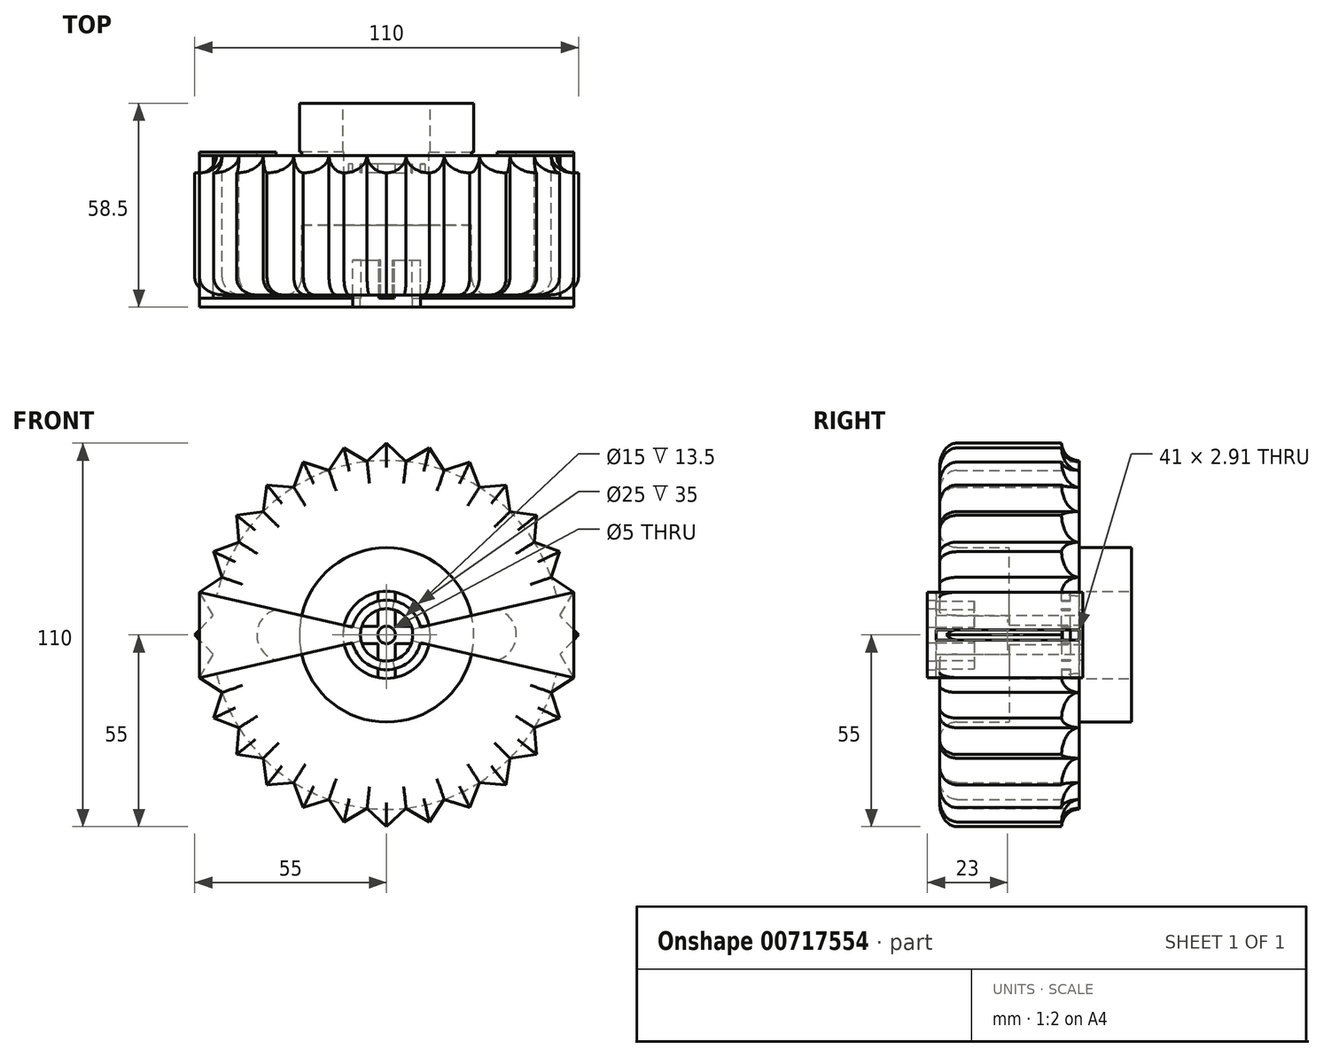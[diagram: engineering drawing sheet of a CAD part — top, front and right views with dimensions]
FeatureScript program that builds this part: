
annotation { "Feature Type Name" : "Feature", "Feature Type Description" : "" }
export const myFeature = defineFeature(function(context is Context, id is Id, definition is map)
    precondition{}
    {
        {
            var Q0;
            Q0=qCreatedBy(makeId("Front.planeOp"),FACE);
            var sketch = newSketch(context, id + "F0", { "sketchPlane" : qUnion([Q0])});
            skCircle(sketch, "E0", {"center": v(0, 0) * mm, "radius": 50 * mm});
            skLineSegment(sketch, "E1", {"start": v(-50, 0) * mm, "end": v(50, 0) * mm});
            skLineSegment(sketch, "E2", {"start": v(0, 50) * mm, "end": v(0, -50) * mm});
            skLineSegment(sketch, "E3", {"start": v(0, -50) * mm, "end": v(0, -55) * mm});
            skLineSegment(sketch, "E4.MirrorCS", {"start": v(50, 0) * mm, "end": v(-50, 0) * mm});
            skLineSegment(sketch, "E5.MirrorCS", {"start": v(0, 50) * mm, "end": v(0, 55) * mm});
            skLineSegment(sketch, "E6", {"start": v(50, 0) * mm, "end": v(55, 0) * mm});
            skLineSegment(sketch, "E7.MirrorCS", {"start": v(-50, 0) * mm, "end": v(-55, 0) * mm});
            skLineSegment(sketch, "E8", {"start": v(0, 0) * mm, "end": v(-53.62, -12.24) * mm});
            skLineSegment(sketch, "E9", {"start": v(0, 0) * mm, "end": v(-49.55, -23.86) * mm});
            skLineSegment(sketch, "E10", {"start": v(0, 0) * mm, "end": v(-43, -34.3) * mm});
            skLineSegment(sketch, "E11", {"start": v(0, 0) * mm, "end": v(-34.3, -43) * mm});
            skLineSegment(sketch, "E12", {"start": v(0, 0) * mm, "end": v(-23.86, -49.55) * mm});
            skLineSegment(sketch, "E13", {"start": v(0, 0) * mm, "end": v(-12.24, -53.62) * mm});
            skPoint(sketch, "E14", {"position": v(-48.75, -11.13) * mm});
            skPoint(sketch, "E15", {"position": v(-45.05, -21.7) * mm});
            skPoint(sketch, "E16", {"position": v(-39.1, -31.17) * mm});
            skPoint(sketch, "E17", {"position": v(-31.17, -39.1) * mm});
            skPoint(sketch, "E18", {"position": v(-21.7, -45.05) * mm});
            skPoint(sketch, "E19", {"position": v(-11.13, -48.75) * mm});
            skLineSegment(sketch, "E20", {"start": v(0, 0) * mm, "end": v(-49.69, -5.6) * mm});
            skLineSegment(sketch, "E21", {"start": v(0, 0) * mm, "end": v(-47.2, -16.51) * mm});
            skLineSegment(sketch, "E22", {"start": v(0, 0) * mm, "end": v(-42.34, -26.6) * mm});
            skLineSegment(sketch, "E23", {"start": v(0, 0) * mm, "end": v(-35.36, -35.36) * mm});
            skLineSegment(sketch, "E24", {"start": v(0, 0) * mm, "end": v(-26.6, -42.34) * mm});
            skLineSegment(sketch, "E25", {"start": v(0, 0) * mm, "end": v(-16.51, -47.2) * mm});
            skLineSegment(sketch, "E26", {"start": v(0, 0) * mm, "end": v(-5.6, -49.69) * mm});
            skLineSegment(sketch, "E27.MirrorCS", {"start": v(0, 0) * mm, "end": v(5.6, -49.69) * mm});
            skLineSegment(sketch, "E28.MirrorCS", {"start": v(0, 0) * mm, "end": v(12.24, -53.62) * mm});
            skLineSegment(sketch, "E29.MirrorCS", {"start": v(0, 0) * mm, "end": v(16.51, -47.2) * mm});
            skLineSegment(sketch, "E30.MirrorCS", {"start": v(0, 0) * mm, "end": v(23.86, -49.55) * mm});
            skLineSegment(sketch, "E31.MirrorCS", {"start": v(0, 0) * mm, "end": v(26.6, -42.34) * mm});
            skLineSegment(sketch, "E32.MirrorCS", {"start": v(0, 0) * mm, "end": v(34.3, -43) * mm});
            skLineSegment(sketch, "E33.MirrorCS", {"start": v(0, 0) * mm, "end": v(35.36, -35.36) * mm});
            skLineSegment(sketch, "E34.MirrorCS", {"start": v(0, 0) * mm, "end": v(43, -34.3) * mm});
            skLineSegment(sketch, "E35.MirrorCS", {"start": v(0, 0) * mm, "end": v(42.34, -26.6) * mm});
            skLineSegment(sketch, "E36.MirrorCS", {"start": v(0, 0) * mm, "end": v(49.69, -5.6) * mm});
            skLineSegment(sketch, "E37.MirrorCS", {"start": v(0, 0) * mm, "end": v(53.62, -12.24) * mm});
            skLineSegment(sketch, "E38.MirrorCS", {"start": v(0, 0) * mm, "end": v(47.2, -16.51) * mm});
            skLineSegment(sketch, "E39.MirrorCS", {"start": v(0, 0) * mm, "end": v(49.55, -23.86) * mm});
            skPoint(sketch, "E40.MirrorP", {"position": v(-31.17, 39.1) * mm});
            skPoint(sketch, "E41.MirrorP", {"position": v(-48.75, 11.13) * mm});
            skPoint(sketch, "E42.MirrorP", {"position": v(-45.05, 21.7) * mm});
            skPoint(sketch, "E43.MirrorP", {"position": v(-39.1, 31.17) * mm});
            skLineSegment(sketch, "E44.MirrorCS", {"start": v(0, 0) * mm, "end": v(42.34, 26.6) * mm});
            skLineSegment(sketch, "E45.MirrorCS", {"start": v(0, 0) * mm, "end": v(43, 34.3) * mm});
            skLineSegment(sketch, "E46.MirrorCS", {"start": v(0, 0) * mm, "end": v(49.55, 23.86) * mm});
            skLineSegment(sketch, "E47.MirrorCS", {"start": v(0, 0) * mm, "end": v(34.3, 43) * mm});
            skLineSegment(sketch, "E48.MirrorCS", {"start": v(0, 0) * mm, "end": v(-49.69, 5.6) * mm});
            skLineSegment(sketch, "E49.MirrorCS", {"start": v(0, 0) * mm, "end": v(-26.6, 42.34) * mm});
            skLineSegment(sketch, "E50.MirrorCS", {"start": v(0, 0) * mm, "end": v(5.6, 49.69) * mm});
            skLineSegment(sketch, "E51.MirrorCS", {"start": v(0, -50) * mm, "end": v(0, 50) * mm});
            skLineSegment(sketch, "E52.MirrorCS", {"start": v(0, 0) * mm, "end": v(23.86, 49.55) * mm});
            skLineSegment(sketch, "E53.MirrorCS", {"start": v(0, 0) * mm, "end": v(-43, 34.3) * mm});
            skLineSegment(sketch, "E54.MirrorCS", {"start": v(0, 0) * mm, "end": v(26.6, 42.34) * mm});
            skLineSegment(sketch, "E55.MirrorCS", {"start": v(0, 0) * mm, "end": v(-49.55, 23.86) * mm});
            skLineSegment(sketch, "E56.MirrorCS", {"start": v(0, 0) * mm, "end": v(-53.62, 12.24) * mm});
            skLineSegment(sketch, "E57.MirrorCS", {"start": v(0, 0) * mm, "end": v(-16.51, 47.2) * mm});
            skLineSegment(sketch, "E58.MirrorCS", {"start": v(0, 0) * mm, "end": v(35.36, 35.36) * mm});
            skLineSegment(sketch, "E59.MirrorCS", {"start": v(0, 0) * mm, "end": v(-47.2, 16.51) * mm});
            skLineSegment(sketch, "E60.MirrorCS", {"start": v(0, 0) * mm, "end": v(49.69, 5.6) * mm});
            skLineSegment(sketch, "E61.MirrorCS", {"start": v(0, 0) * mm, "end": v(-12.24, 53.62) * mm});
            skLineSegment(sketch, "E62.MirrorCS", {"start": v(0, 0) * mm, "end": v(-23.86, 49.55) * mm});
            skLineSegment(sketch, "E63.MirrorCS", {"start": v(0, 0) * mm, "end": v(-34.3, 43) * mm});
            skLineSegment(sketch, "E64.MirrorCS", {"start": v(0, 0) * mm, "end": v(47.2, 16.51) * mm});
            skLineSegment(sketch, "E65.MirrorCS", {"start": v(0, 0) * mm, "end": v(53.62, 12.24) * mm});
            skLineSegment(sketch, "E66.MirrorCS", {"start": v(0, 0) * mm, "end": v(-35.36, 35.36) * mm});
            skLineSegment(sketch, "E67.MirrorCS", {"start": v(0, 0) * mm, "end": v(12.24, 53.62) * mm});
            skLineSegment(sketch, "E68.MirrorCS", {"start": v(0, 0) * mm, "end": v(-5.6, 49.69) * mm});
            skLineSegment(sketch, "E69.MirrorCS", {"start": v(0, 0) * mm, "end": v(16.51, 47.2) * mm});
            skLineSegment(sketch, "E70.MirrorCS", {"start": v(0, 0) * mm, "end": v(-42.34, 26.6) * mm});
            skSolve(sketch);
        }
        {
            var Q0;
            Q0=qCreatedBy(makeId("Front.planeOp"),FACE);
            var sketch = newSketch(context, id + "F1", { "sketchPlane" : qUnion([Q0])});
            skPoint(sketch, "E71.0", {"position": v(12.24, 53.62) * mm});
            skPoint(sketch, "E72.0", {"position": v(16.51, 47.2) * mm});
            skPoint(sketch, "E73.0", {"position": v(23.86, 49.55) * mm});
            skPoint(sketch, "E74.0", {"position": v(5.6, 49.69) * mm});
            skPoint(sketch, "E75.0", {"position": v(0, 55) * mm});
            skPoint(sketch, "E76.0", {"position": v(26.6, 42.34) * mm});
            skPoint(sketch, "E77.0", {"position": v(34.3, 43) * mm});
            skPoint(sketch, "E78.0", {"position": v(35.36, 35.36) * mm});
            skPoint(sketch, "E79.0", {"position": v(43, 34.3) * mm});
            skPoint(sketch, "E80.0", {"position": v(42.34, 26.6) * mm});
            skPoint(sketch, "E81.0", {"position": v(49.55, 23.86) * mm});
            skPoint(sketch, "E82.0", {"position": v(47.2, 16.51) * mm});
            skPoint(sketch, "E83.0", {"position": v(53.62, 12.24) * mm});
            skPoint(sketch, "E84.0", {"position": v(49.69, 5.6) * mm});
            skPoint(sketch, "E85.0", {"position": v(55, 0) * mm});
            skLineSegment(sketch, "E86", {"start": v(0, 55) * mm, "end": v(5.6, 49.69) * mm});
            skLineSegment(sketch, "E87", {"start": v(5.6, 49.69) * mm, "end": v(12.24, 53.62) * mm});
            skLineSegment(sketch, "E88", {"start": v(12.24, 53.62) * mm, "end": v(16.51, 47.2) * mm});
            skLineSegment(sketch, "E89", {"start": v(16.51, 47.2) * mm, "end": v(23.86, 49.55) * mm});
            skLineSegment(sketch, "E90", {"start": v(23.86, 49.55) * mm, "end": v(26.6, 42.34) * mm});
            skLineSegment(sketch, "E91", {"start": v(26.6, 42.34) * mm, "end": v(34.3, 43) * mm});
            skLineSegment(sketch, "E92", {"start": v(34.3, 43) * mm, "end": v(35.36, 35.36) * mm});
            skLineSegment(sketch, "E93", {"start": v(35.36, 35.36) * mm, "end": v(43, 34.3) * mm});
            skLineSegment(sketch, "E94", {"start": v(43, 34.3) * mm, "end": v(42.34, 26.6) * mm});
            skLineSegment(sketch, "E95", {"start": v(42.34, 26.6) * mm, "end": v(49.55, 23.86) * mm});
            skLineSegment(sketch, "E96", {"start": v(49.55, 23.86) * mm, "end": v(47.2, 16.51) * mm});
            skLineSegment(sketch, "E97", {"start": v(47.2, 16.51) * mm, "end": v(53.62, 12.24) * mm});
            skLineSegment(sketch, "E98", {"start": v(53.62, 12.24) * mm, "end": v(49.69, 5.6) * mm});
            skLineSegment(sketch, "E99", {"start": v(49.69, 5.6) * mm, "end": v(55, 0) * mm});
            skLineSegment(sketch, "E100.MirrorCS", {"start": v(-5.6, 49.69) * mm, "end": v(-12.24, 53.62) * mm});
            skLineSegment(sketch, "E101.MirrorCS", {"start": v(-34.3, 43) * mm, "end": v(-35.36, 35.36) * mm});
            skLineSegment(sketch, "E102.MirrorCS", {"start": v(-12.24, 53.62) * mm, "end": v(-16.51, 47.2) * mm});
            skLineSegment(sketch, "E103.MirrorCS", {"start": v(-53.62, 12.24) * mm, "end": v(-49.69, 5.6) * mm});
            skLineSegment(sketch, "E104.MirrorCS", {"start": v(-42.34, 26.6) * mm, "end": v(-49.55, 23.86) * mm});
            skLineSegment(sketch, "E105.MirrorCS", {"start": v(-16.51, 47.2) * mm, "end": v(-23.86, 49.55) * mm});
            skLineSegment(sketch, "E106.MirrorCS", {"start": v(-23.86, 49.55) * mm, "end": v(-26.6, 42.34) * mm});
            skLineSegment(sketch, "E107.MirrorCS", {"start": v(-47.2, 16.51) * mm, "end": v(-53.62, 12.24) * mm});
            skLineSegment(sketch, "E108.MirrorCS", {"start": v(0, 55) * mm, "end": v(-5.6, 49.69) * mm});
            skLineSegment(sketch, "E109.MirrorCS", {"start": v(-49.69, 5.6) * mm, "end": v(-55, 0) * mm});
            skLineSegment(sketch, "E110.MirrorCS", {"start": v(-43, 34.3) * mm, "end": v(-42.34, 26.6) * mm});
            skLineSegment(sketch, "E111.MirrorCS", {"start": v(-35.36, 35.36) * mm, "end": v(-43, 34.3) * mm});
            skLineSegment(sketch, "E112.MirrorCS", {"start": v(-26.6, 42.34) * mm, "end": v(-34.3, 43) * mm});
            skLineSegment(sketch, "E113.MirrorCS", {"start": v(-49.55, 23.86) * mm, "end": v(-47.2, 16.51) * mm});
            skPoint(sketch, "E114.MirrorP", {"position": v(-49.55, 23.86) * mm});
            skPoint(sketch, "E115.MirrorP", {"position": v(-5.6, 49.69) * mm});
            skPoint(sketch, "E116.MirrorP", {"position": v(-47.2, 16.51) * mm});
            skPoint(sketch, "E117.MirrorP", {"position": v(-23.86, 49.55) * mm});
            skPoint(sketch, "E118.MirrorP", {"position": v(-42.34, 26.6) * mm});
            skPoint(sketch, "E119.MirrorP", {"position": v(-12.24, 53.62) * mm});
            skPoint(sketch, "E120.MirrorP", {"position": v(-49.69, 5.6) * mm});
            skPoint(sketch, "E121.MirrorP", {"position": v(-35.36, 35.36) * mm});
            skPoint(sketch, "E122.MirrorP", {"position": v(-55, 0) * mm});
            skPoint(sketch, "E123.MirrorP", {"position": v(-43, 34.3) * mm});
            skPoint(sketch, "E124.MirrorP", {"position": v(-34.3, 43) * mm});
            skPoint(sketch, "E125.MirrorP", {"position": v(-53.62, 12.24) * mm});
            skPoint(sketch, "E126.MirrorP", {"position": v(-16.51, 47.2) * mm});
            skPoint(sketch, "E127.MirrorP", {"position": v(-26.6, 42.34) * mm});
            skLineSegment(sketch, "E128.MirrorCS", {"start": v(53.62, -12.24) * mm, "end": v(49.69, -5.6) * mm});
            skLineSegment(sketch, "E129.MirrorCS", {"start": v(-53.62, -12.24) * mm, "end": v(-49.69, -5.6) * mm});
            skLineSegment(sketch, "E130.MirrorCS", {"start": v(47.2, -16.51) * mm, "end": v(53.62, -12.24) * mm});
            skLineSegment(sketch, "E131.MirrorCS", {"start": v(49.55, -23.86) * mm, "end": v(47.2, -16.51) * mm});
            skLineSegment(sketch, "E132.MirrorCS", {"start": v(-16.51, -47.2) * mm, "end": v(-23.86, -49.55) * mm});
            skLineSegment(sketch, "E133.MirrorCS", {"start": v(42.34, -26.6) * mm, "end": v(49.55, -23.86) * mm});
            skLineSegment(sketch, "E134.MirrorCS", {"start": v(43, -34.3) * mm, "end": v(42.34, -26.6) * mm});
            skLineSegment(sketch, "E135.MirrorCS", {"start": v(-47.2, -16.51) * mm, "end": v(-53.62, -12.24) * mm});
            skLineSegment(sketch, "E136.MirrorCS", {"start": v(26.6, -42.34) * mm, "end": v(34.3, -43) * mm});
            skLineSegment(sketch, "E137.MirrorCS", {"start": v(-43, -34.3) * mm, "end": v(-42.34, -26.6) * mm});
            skLineSegment(sketch, "E138.MirrorCS", {"start": v(16.51, -47.2) * mm, "end": v(23.86, -49.55) * mm});
            skLineSegment(sketch, "E139.MirrorCS", {"start": v(12.24, -53.62) * mm, "end": v(16.51, -47.2) * mm});
            skLineSegment(sketch, "E140.MirrorCS", {"start": v(5.6, -49.69) * mm, "end": v(12.24, -53.62) * mm});
            skLineSegment(sketch, "E141.MirrorCS", {"start": v(0, -55) * mm, "end": v(5.6, -49.69) * mm});
            skLineSegment(sketch, "E142.MirrorCS", {"start": v(-5.6, -49.69) * mm, "end": v(-12.24, -53.62) * mm});
            skLineSegment(sketch, "E143.MirrorCS", {"start": v(-35.36, -35.36) * mm, "end": v(-43, -34.3) * mm});
            skLineSegment(sketch, "E144.MirrorCS", {"start": v(-49.55, -23.86) * mm, "end": v(-47.2, -16.51) * mm});
            skLineSegment(sketch, "E145.MirrorCS", {"start": v(-42.34, -26.6) * mm, "end": v(-49.55, -23.86) * mm});
            skLineSegment(sketch, "E146.MirrorCS", {"start": v(0, -55) * mm, "end": v(-5.6, -49.69) * mm});
            skLineSegment(sketch, "E147.MirrorCS", {"start": v(-12.24, -53.62) * mm, "end": v(-16.51, -47.2) * mm});
            skLineSegment(sketch, "E148.MirrorCS", {"start": v(49.69, -5.6) * mm, "end": v(55, 0) * mm});
            skLineSegment(sketch, "E149.MirrorCS", {"start": v(-49.69, -5.6) * mm, "end": v(-55, 0) * mm});
            skLineSegment(sketch, "E150.MirrorCS", {"start": v(35.36, -35.36) * mm, "end": v(43, -34.3) * mm});
            skLineSegment(sketch, "E151.MirrorCS", {"start": v(34.3, -43) * mm, "end": v(35.36, -35.36) * mm});
            skLineSegment(sketch, "E152.MirrorCS", {"start": v(23.86, -49.55) * mm, "end": v(26.6, -42.34) * mm});
            skLineSegment(sketch, "E153.MirrorCS", {"start": v(-26.6, -42.34) * mm, "end": v(-34.3, -43) * mm});
            skLineSegment(sketch, "E154.MirrorCS", {"start": v(-34.3, -43) * mm, "end": v(-35.36, -35.36) * mm});
            skPoint(sketch, "E155.MirrorP", {"position": v(0, -55) * mm});
            skLineSegment(sketch, "E156.MirrorCS", {"start": v(-23.86, -49.55) * mm, "end": v(-26.6, -42.34) * mm});
            skPoint(sketch, "E157.MirrorP", {"position": v(12.24, -53.62) * mm});
            skPoint(sketch, "E158.MirrorP", {"position": v(-5.6, -49.69) * mm});
            skPoint(sketch, "E159.MirrorP", {"position": v(23.86, -49.55) * mm});
            skPoint(sketch, "E160.MirrorP", {"position": v(-23.86, -49.55) * mm});
            skPoint(sketch, "E161.MirrorP", {"position": v(-12.24, -53.62) * mm});
            skPoint(sketch, "E162.MirrorP", {"position": v(42.34, -26.6) * mm});
            skPoint(sketch, "E163.MirrorP", {"position": v(-43, -34.3) * mm});
            skPoint(sketch, "E164.MirrorP", {"position": v(47.2, -16.51) * mm});
            skPoint(sketch, "E165.MirrorP", {"position": v(53.62, -12.24) * mm});
            skPoint(sketch, "E166.MirrorP", {"position": v(43, -34.3) * mm});
            skPoint(sketch, "E167.MirrorP", {"position": v(-49.55, -23.86) * mm});
            skPoint(sketch, "E168.MirrorP", {"position": v(-16.51, -47.2) * mm});
            skPoint(sketch, "E169.MirrorP", {"position": v(-35.36, -35.36) * mm});
            skPoint(sketch, "E170.MirrorP", {"position": v(26.6, -42.34) * mm});
            skPoint(sketch, "E171.MirrorP", {"position": v(-42.34, -26.6) * mm});
            skPoint(sketch, "E172.MirrorP", {"position": v(5.6, -49.69) * mm});
            skPoint(sketch, "E173.MirrorP", {"position": v(-34.3, -43) * mm});
            skPoint(sketch, "E174.MirrorP", {"position": v(-53.62, -12.24) * mm});
            skPoint(sketch, "E175.MirrorP", {"position": v(49.55, -23.86) * mm});
            skPoint(sketch, "E176.MirrorP", {"position": v(-47.2, -16.51) * mm});
            skPoint(sketch, "E177.MirrorP", {"position": v(35.36, -35.36) * mm});
            skPoint(sketch, "E178.MirrorP", {"position": v(-26.6, -42.34) * mm});
            skPoint(sketch, "E179.MirrorP", {"position": v(34.3, -43) * mm});
            skPoint(sketch, "E180.MirrorP", {"position": v(16.51, -47.2) * mm});
            skPoint(sketch, "E181.MirrorP", {"position": v(-49.69, -5.6) * mm});
            skPoint(sketch, "E182.MirrorP", {"position": v(49.69, -5.6) * mm});
            skSolve(sketch);
        }
        {
            var Q0;
            Q0=qSketchRegion(id+"F1",true);
            extrude(context, id + "F2", {"entities" : qUnion([Q0]), "depth" : 10 * mm, "offsetDistance" : 25 * mm});
        }
        {
            var Q0;
            {var subQ0=sQuery(id+"F0.wireOp",EDGE,"E24");Q0=makeQuery(id+"F0.imprint","IMPRINT",FACE,{"disambiguationData":[TD([[makeQuery(id+"F0.imprint","IMPRINT",EDGE,{"derivedFrom":subQ0}),-1.0]])]});}
            var Q1;
            {var subQ0=sQuery(id+"F0.wireOp",EDGE,"E23");Q1=makeQuery(id+"F0.imprint","IMPRINT",FACE,{"disambiguationData":[TD([[makeQuery(id+"F0.imprint","IMPRINT",EDGE,{"derivedFrom":subQ0}),1.0]])]});}
            var Q2;
            {var subQ0=sQuery(id+"F0.wireOp",EDGE,"E23");Q2=makeQuery(id+"F0.imprint","IMPRINT",FACE,{"disambiguationData":[TD([[makeQuery(id+"F0.imprint","IMPRINT",EDGE,{"derivedFrom":subQ0}),-1.0]])]});}
            var Q3;
            {var subQ0=sQuery(id+"F0.wireOp",EDGE,"E22");Q3=makeQuery(id+"F0.imprint","IMPRINT",FACE,{"disambiguationData":[TD([[makeQuery(id+"F0.imprint","IMPRINT",EDGE,{"derivedFrom":subQ0}),1.0]])]});}
            var Q4;
            {var subQ0=sQuery(id+"F0.wireOp",EDGE,"E22");Q4=makeQuery(id+"F0.imprint","IMPRINT",FACE,{"disambiguationData":[TD([[makeQuery(id+"F0.imprint","IMPRINT",EDGE,{"derivedFrom":subQ0}),-1.0]])]});}
            var Q5;
            {var subQ0=sQuery(id+"F0.wireOp",EDGE,"E21");Q5=makeQuery(id+"F0.imprint","IMPRINT",FACE,{"disambiguationData":[TD([[makeQuery(id+"F0.imprint","IMPRINT",EDGE,{"derivedFrom":subQ0}),1.0]])]});}
            var Q6;
            {var subQ0=sQuery(id+"F0.wireOp",EDGE,"E21");Q6=makeQuery(id+"F0.imprint","IMPRINT",FACE,{"disambiguationData":[TD([[makeQuery(id+"F0.imprint","IMPRINT",EDGE,{"derivedFrom":subQ0}),-1.0]])]});}
            var Q7;
            {var subQ0=sQuery(id+"F0.wireOp",EDGE,"E20");Q7=makeQuery(id+"F0.imprint","IMPRINT",FACE,{"disambiguationData":[TD([[makeQuery(id+"F0.imprint","IMPRINT",EDGE,{"derivedFrom":subQ0}),1.0]])]});}
            var Q8;
            {var subQ3=sQuery(id+"F0.wireOp",EDGE,"E20");Q8=makeQuery(id+"F0.imprint","IMPRINT",FACE,{"disambiguationData":[TD([[makeQuery(id+"F0.imprint","IMPRINT",EDGE,{"derivedFrom":subQ3}),-1.0]])]});}
            var Q9;
            {var subQ3=sQuery(id+"F0.wireOp",EDGE,"E48.MirrorCS");Q9=makeQuery(id+"F0.imprint","IMPRINT",FACE,{"disambiguationData":[TD([[makeQuery(id+"F0.imprint","IMPRINT",EDGE,{"derivedFrom":subQ3}),1.0]])]});}
            var Q10;
            {var subQ0=sQuery(id+"F0.wireOp",EDGE,"E48.MirrorCS");Q10=makeQuery(id+"F0.imprint","IMPRINT",FACE,{"disambiguationData":[TD([[makeQuery(id+"F0.imprint","IMPRINT",EDGE,{"derivedFrom":subQ0}),-1.0]])]});}
            var Q11;
            {var subQ0=sQuery(id+"F0.wireOp",EDGE,"E59.MirrorCS");Q11=makeQuery(id+"F0.imprint","IMPRINT",FACE,{"disambiguationData":[TD([[makeQuery(id+"F0.imprint","IMPRINT",EDGE,{"derivedFrom":subQ0}),1.0]])]});}
            var Q12;
            {var subQ0=sQuery(id+"F0.wireOp",EDGE,"E59.MirrorCS");Q12=makeQuery(id+"F0.imprint","IMPRINT",FACE,{"disambiguationData":[TD([[makeQuery(id+"F0.imprint","IMPRINT",EDGE,{"derivedFrom":subQ0}),-1.0]])]});}
            var Q13;
            {var subQ0=sQuery(id+"F0.wireOp",EDGE,"E70.MirrorCS");Q13=makeQuery(id+"F0.imprint","IMPRINT",FACE,{"disambiguationData":[TD([[makeQuery(id+"F0.imprint","IMPRINT",EDGE,{"derivedFrom":subQ0}),1.0]])]});}
            var Q14;
            {var subQ0=sQuery(id+"F0.wireOp",EDGE,"E70.MirrorCS");Q14=makeQuery(id+"F0.imprint","IMPRINT",FACE,{"disambiguationData":[TD([[makeQuery(id+"F0.imprint","IMPRINT",EDGE,{"derivedFrom":subQ0}),-1.0]])]});}
            var Q15;
            {var subQ0=sQuery(id+"F0.wireOp",EDGE,"E66.MirrorCS");Q15=makeQuery(id+"F0.imprint","IMPRINT",FACE,{"disambiguationData":[TD([[makeQuery(id+"F0.imprint","IMPRINT",EDGE,{"derivedFrom":subQ0}),1.0]])]});}
            var Q16;
            {var subQ0=sQuery(id+"F0.wireOp",EDGE,"E66.MirrorCS");Q16=makeQuery(id+"F0.imprint","IMPRINT",FACE,{"disambiguationData":[TD([[makeQuery(id+"F0.imprint","IMPRINT",EDGE,{"derivedFrom":subQ0}),-1.0]])]});}
            var Q17;
            {var subQ0=sQuery(id+"F0.wireOp",EDGE,"E49.MirrorCS");Q17=makeQuery(id+"F0.imprint","IMPRINT",FACE,{"disambiguationData":[TD([[makeQuery(id+"F0.imprint","IMPRINT",EDGE,{"derivedFrom":subQ0}),1.0]])]});}
            var Q18;
            {var subQ0=sQuery(id+"F0.wireOp",EDGE,"E49.MirrorCS");Q18=makeQuery(id+"F0.imprint","IMPRINT",FACE,{"disambiguationData":[TD([[makeQuery(id+"F0.imprint","IMPRINT",EDGE,{"derivedFrom":subQ0}),-1.0]])]});}
            var Q19;
            {var subQ0=sQuery(id+"F0.wireOp",EDGE,"E57.MirrorCS");Q19=makeQuery(id+"F0.imprint","IMPRINT",FACE,{"disambiguationData":[TD([[makeQuery(id+"F0.imprint","IMPRINT",EDGE,{"derivedFrom":subQ0}),1.0]])]});}
            var Q20;
            {var subQ0=sQuery(id+"F0.wireOp",EDGE,"E57.MirrorCS");Q20=makeQuery(id+"F0.imprint","IMPRINT",FACE,{"disambiguationData":[TD([[makeQuery(id+"F0.imprint","IMPRINT",EDGE,{"derivedFrom":subQ0}),-1.0]])]});}
            var Q21;
            {var subQ0=sQuery(id+"F0.wireOp",EDGE,"E68.MirrorCS");Q21=makeQuery(id+"F0.imprint","IMPRINT",FACE,{"disambiguationData":[TD([[makeQuery(id+"F0.imprint","IMPRINT",EDGE,{"derivedFrom":subQ0}),1.0]])]});}
            var Q22;
            {var subQ3=sQuery(id+"F0.wireOp",EDGE,"E68.MirrorCS");Q22=makeQuery(id+"F0.imprint","IMPRINT",FACE,{"disambiguationData":[TD([[makeQuery(id+"F0.imprint","IMPRINT",EDGE,{"derivedFrom":subQ3}),-1.0]])]});}
            var Q23;
            {var subQ0=sQuery(id+"F0.wireOp",EDGE,"E50.MirrorCS");Q23=makeQuery(id+"F0.imprint","IMPRINT",FACE,{"disambiguationData":[TD([[makeQuery(id+"F0.imprint","IMPRINT",EDGE,{"derivedFrom":subQ0}),1.0]])]});}
            var Q24;
            {var subQ0=sQuery(id+"F0.wireOp",EDGE,"E50.MirrorCS");Q24=makeQuery(id+"F0.imprint","IMPRINT",FACE,{"disambiguationData":[TD([[makeQuery(id+"F0.imprint","IMPRINT",EDGE,{"derivedFrom":subQ0}),-1.0]])]});}
            var Q25;
            {var subQ0=sQuery(id+"F0.wireOp",EDGE,"E69.MirrorCS");Q25=makeQuery(id+"F0.imprint","IMPRINT",FACE,{"disambiguationData":[TD([[makeQuery(id+"F0.imprint","IMPRINT",EDGE,{"derivedFrom":subQ0}),1.0]])]});}
            var Q26;
            {var subQ0=sQuery(id+"F0.wireOp",EDGE,"E69.MirrorCS");Q26=makeQuery(id+"F0.imprint","IMPRINT",FACE,{"disambiguationData":[TD([[makeQuery(id+"F0.imprint","IMPRINT",EDGE,{"derivedFrom":subQ0}),-1.0]])]});}
            var Q27;
            {var subQ0=sQuery(id+"F0.wireOp",EDGE,"E54.MirrorCS");Q27=makeQuery(id+"F0.imprint","IMPRINT",FACE,{"disambiguationData":[TD([[makeQuery(id+"F0.imprint","IMPRINT",EDGE,{"derivedFrom":subQ0}),1.0]])]});}
            var Q28;
            {var subQ0=sQuery(id+"F0.wireOp",EDGE,"E54.MirrorCS");Q28=makeQuery(id+"F0.imprint","IMPRINT",FACE,{"disambiguationData":[TD([[makeQuery(id+"F0.imprint","IMPRINT",EDGE,{"derivedFrom":subQ0}),-1.0]])]});}
            var Q29;
            {var subQ0=sQuery(id+"F0.wireOp",EDGE,"E58.MirrorCS");Q29=makeQuery(id+"F0.imprint","IMPRINT",FACE,{"disambiguationData":[TD([[makeQuery(id+"F0.imprint","IMPRINT",EDGE,{"derivedFrom":subQ0}),1.0]])]});}
            var Q30;
            {var subQ0=sQuery(id+"F0.wireOp",EDGE,"E58.MirrorCS");Q30=makeQuery(id+"F0.imprint","IMPRINT",FACE,{"disambiguationData":[TD([[makeQuery(id+"F0.imprint","IMPRINT",EDGE,{"derivedFrom":subQ0}),-1.0]])]});}
            var Q31;
            {var subQ0=sQuery(id+"F0.wireOp",EDGE,"E44.MirrorCS");Q31=makeQuery(id+"F0.imprint","IMPRINT",FACE,{"disambiguationData":[TD([[makeQuery(id+"F0.imprint","IMPRINT",EDGE,{"derivedFrom":subQ0}),1.0]])]});}
            var Q32;
            {var subQ0=sQuery(id+"F0.wireOp",EDGE,"E44.MirrorCS");Q32=makeQuery(id+"F0.imprint","IMPRINT",FACE,{"disambiguationData":[TD([[makeQuery(id+"F0.imprint","IMPRINT",EDGE,{"derivedFrom":subQ0}),-1.0]])]});}
            var Q33;
            {var subQ0=sQuery(id+"F0.wireOp",EDGE,"E64.MirrorCS");Q33=makeQuery(id+"F0.imprint","IMPRINT",FACE,{"disambiguationData":[TD([[makeQuery(id+"F0.imprint","IMPRINT",EDGE,{"derivedFrom":subQ0}),1.0]])]});}
            var Q34;
            {var subQ0=sQuery(id+"F0.wireOp",EDGE,"E64.MirrorCS");Q34=makeQuery(id+"F0.imprint","IMPRINT",FACE,{"disambiguationData":[TD([[makeQuery(id+"F0.imprint","IMPRINT",EDGE,{"derivedFrom":subQ0}),-1.0]])]});}
            var Q35;
            {var subQ0=sQuery(id+"F0.wireOp",EDGE,"E60.MirrorCS");Q35=makeQuery(id+"F0.imprint","IMPRINT",FACE,{"disambiguationData":[TD([[makeQuery(id+"F0.imprint","IMPRINT",EDGE,{"derivedFrom":subQ0}),1.0]])]});}
            var Q36;
            {var subQ3=sQuery(id+"F0.wireOp",EDGE,"E60.MirrorCS");Q36=makeQuery(id+"F0.imprint","IMPRINT",FACE,{"disambiguationData":[TD([[makeQuery(id+"F0.imprint","IMPRINT",EDGE,{"derivedFrom":subQ3}),-1.0]])]});}
            var Q37;
            {var subQ3=sQuery(id+"F0.wireOp",EDGE,"E36.MirrorCS");Q37=makeQuery(id+"F0.imprint","IMPRINT",FACE,{"disambiguationData":[TD([[makeQuery(id+"F0.imprint","IMPRINT",EDGE,{"derivedFrom":subQ3}),1.0]])]});}
            var Q38;
            {var subQ0=sQuery(id+"F0.wireOp",EDGE,"E36.MirrorCS");Q38=makeQuery(id+"F0.imprint","IMPRINT",FACE,{"disambiguationData":[TD([[makeQuery(id+"F0.imprint","IMPRINT",EDGE,{"derivedFrom":subQ0}),-1.0]])]});}
            var Q39;
            {var subQ0=sQuery(id+"F0.wireOp",EDGE,"E38.MirrorCS");Q39=makeQuery(id+"F0.imprint","IMPRINT",FACE,{"disambiguationData":[TD([[makeQuery(id+"F0.imprint","IMPRINT",EDGE,{"derivedFrom":subQ0}),1.0]])]});}
            var Q40;
            {var subQ0=sQuery(id+"F0.wireOp",EDGE,"E38.MirrorCS");Q40=makeQuery(id+"F0.imprint","IMPRINT",FACE,{"disambiguationData":[TD([[makeQuery(id+"F0.imprint","IMPRINT",EDGE,{"derivedFrom":subQ0}),-1.0]])]});}
            var Q41;
            {var subQ0=sQuery(id+"F0.wireOp",EDGE,"E35.MirrorCS");Q41=makeQuery(id+"F0.imprint","IMPRINT",FACE,{"disambiguationData":[TD([[makeQuery(id+"F0.imprint","IMPRINT",EDGE,{"derivedFrom":subQ0}),1.0]])]});}
            var Q42;
            {var subQ0=sQuery(id+"F0.wireOp",EDGE,"E35.MirrorCS");Q42=makeQuery(id+"F0.imprint","IMPRINT",FACE,{"disambiguationData":[TD([[makeQuery(id+"F0.imprint","IMPRINT",EDGE,{"derivedFrom":subQ0}),-1.0]])]});}
            var Q43;
            {var subQ0=sQuery(id+"F0.wireOp",EDGE,"E33.MirrorCS");Q43=makeQuery(id+"F0.imprint","IMPRINT",FACE,{"disambiguationData":[TD([[makeQuery(id+"F0.imprint","IMPRINT",EDGE,{"derivedFrom":subQ0}),1.0]])]});}
            var Q44;
            {var subQ0=sQuery(id+"F0.wireOp",EDGE,"E33.MirrorCS");Q44=makeQuery(id+"F0.imprint","IMPRINT",FACE,{"disambiguationData":[TD([[makeQuery(id+"F0.imprint","IMPRINT",EDGE,{"derivedFrom":subQ0}),-1.0]])]});}
            var Q45;
            {var subQ0=sQuery(id+"F0.wireOp",EDGE,"E31.MirrorCS");Q45=makeQuery(id+"F0.imprint","IMPRINT",FACE,{"disambiguationData":[TD([[makeQuery(id+"F0.imprint","IMPRINT",EDGE,{"derivedFrom":subQ0}),1.0]])]});}
            var Q46;
            {var subQ0=sQuery(id+"F0.wireOp",EDGE,"E31.MirrorCS");Q46=makeQuery(id+"F0.imprint","IMPRINT",FACE,{"disambiguationData":[TD([[makeQuery(id+"F0.imprint","IMPRINT",EDGE,{"derivedFrom":subQ0}),-1.0]])]});}
            var Q47;
            {var subQ0=sQuery(id+"F0.wireOp",EDGE,"E29.MirrorCS");Q47=makeQuery(id+"F0.imprint","IMPRINT",FACE,{"disambiguationData":[TD([[makeQuery(id+"F0.imprint","IMPRINT",EDGE,{"derivedFrom":subQ0}),1.0]])]});}
            var Q48;
            {var subQ0=sQuery(id+"F0.wireOp",EDGE,"E29.MirrorCS");Q48=makeQuery(id+"F0.imprint","IMPRINT",FACE,{"disambiguationData":[TD([[makeQuery(id+"F0.imprint","IMPRINT",EDGE,{"derivedFrom":subQ0}),-1.0]])]});}
            var Q49;
            {var subQ0=sQuery(id+"F0.wireOp",EDGE,"E27.MirrorCS");Q49=makeQuery(id+"F0.imprint","IMPRINT",FACE,{"disambiguationData":[TD([[makeQuery(id+"F0.imprint","IMPRINT",EDGE,{"derivedFrom":subQ0}),1.0]])]});}
            var Q50;
            {var subQ0=sQuery(id+"F0.wireOp",EDGE,"E27.MirrorCS");Q50=makeQuery(id+"F0.imprint","IMPRINT",FACE,{"disambiguationData":[TD([[makeQuery(id+"F0.imprint","IMPRINT",EDGE,{"derivedFrom":subQ0}),-1.0]])]});}
            var Q51;
            {var subQ0=sQuery(id+"F0.wireOp",EDGE,"E26");Q51=makeQuery(id+"F0.imprint","IMPRINT",FACE,{"disambiguationData":[TD([[makeQuery(id+"F0.imprint","IMPRINT",EDGE,{"derivedFrom":subQ0}),1.0]])]});}
            var Q52;
            {var subQ0=sQuery(id+"F0.wireOp",EDGE,"E26");Q52=makeQuery(id+"F0.imprint","IMPRINT",FACE,{"disambiguationData":[TD([[makeQuery(id+"F0.imprint","IMPRINT",EDGE,{"derivedFrom":subQ0}),-1.0]])]});}
            var Q53;
            {var subQ0=sQuery(id+"F0.wireOp",EDGE,"E25");Q53=makeQuery(id+"F0.imprint","IMPRINT",FACE,{"disambiguationData":[TD([[makeQuery(id+"F0.imprint","IMPRINT",EDGE,{"derivedFrom":subQ0}),1.0]])]});}
            var Q54;
            {var subQ0=sQuery(id+"F0.wireOp",EDGE,"E25");Q54=makeQuery(id+"F0.imprint","IMPRINT",FACE,{"disambiguationData":[TD([[makeQuery(id+"F0.imprint","IMPRINT",EDGE,{"derivedFrom":subQ0}),-1.0]])]});}
            var Q55;
            {var subQ0=sQuery(id+"F0.wireOp",EDGE,"E24");Q55=makeQuery(id+"F0.imprint","IMPRINT",FACE,{"disambiguationData":[TD([[makeQuery(id+"F0.imprint","IMPRINT",EDGE,{"derivedFrom":subQ0}),1.0]])]});}
            extrude(context, id + "F3", {"entities" : qUnion([Q0, Q1, Q2, Q3, Q4, Q5, Q6, Q7, Q8, Q9, Q10, Q11, Q12, Q13, Q14, Q15, Q16, Q17, Q18, Q19, Q20, Q21, Q22, Q23, Q24, Q25, Q26, Q27, Q28, Q29, Q30, Q31, Q32, Q33, Q34, Q35, Q36, Q37, Q38, Q39, Q40, Q41, Q42, Q43, Q44, Q45, Q46, Q47, Q48, Q49, Q50, Q51, Q52, Q53, Q54, Q55]), "operationType" : NewBodyOperationType.ADD, "oppositeDirection" : true, "depth" : 5 * mm, "offsetDistance" : 25 * mm});
        }
        {
            var Q0;
            Q0=makeQuery(id+"F3.opExtrude","CAP_FACE",FACE,{"disambiguationData":[OSD([sQuery(id+"F0.wireOp",EDGE,"E0")])],"isStart":false});
            var sketch = newSketch(context, id + "F4", { "sketchPlane" : qUnion([Q0])});
            skCircle(sketch, "E183", {"center": v(0, 0) * mm, "radius": 25 * mm});
            skSolve(sketch);
        }
        {
            var Q0;
            Q0=qSketchRegion(id+"F4",true);
            extrude(context, id + "F5", {"entities" : qUnion([Q0]), "operationType" : NewBodyOperationType.ADD, "depth" : 15 * mm, "offsetDistance" : 25 * mm});
        }
        {
            var Q0;
            Q0=makeQuery(id+"F2.opExtrude","CAP_FACE",FACE,{"disambiguationData":[OSD([sQuery(id+"F1.wireOp",EDGE,"E86"),sQuery(id+"F1.wireOp",EDGE,"E87"),sQuery(id+"F1.wireOp",EDGE,"E88"),sQuery(id+"F1.wireOp",EDGE,"E89"),sQuery(id+"F1.wireOp",EDGE,"E90"),sQuery(id+"F1.wireOp",EDGE,"E91"),sQuery(id+"F1.wireOp",EDGE,"E92"),sQuery(id+"F1.wireOp",EDGE,"E93"),sQuery(id+"F1.wireOp",EDGE,"E94"),sQuery(id+"F1.wireOp",EDGE,"E95"),sQuery(id+"F1.wireOp",EDGE,"E96"),sQuery(id+"F1.wireOp",EDGE,"E97"),sQuery(id+"F1.wireOp",EDGE,"E98"),sQuery(id+"F1.wireOp",EDGE,"E99"),sQuery(id+"F1.wireOp",EDGE,"E100.MirrorCS"),sQuery(id+"F1.wireOp",EDGE,"E101.MirrorCS"),sQuery(id+"F1.wireOp",EDGE,"E102.MirrorCS"),sQuery(id+"F1.wireOp",EDGE,"E103.MirrorCS"),sQuery(id+"F1.wireOp",EDGE,"E104.MirrorCS"),sQuery(id+"F1.wireOp",EDGE,"E105.MirrorCS"),sQuery(id+"F1.wireOp",EDGE,"E106.MirrorCS"),sQuery(id+"F1.wireOp",EDGE,"E107.MirrorCS"),sQuery(id+"F1.wireOp",EDGE,"E108.MirrorCS"),sQuery(id+"F1.wireOp",EDGE,"E109.MirrorCS"),sQuery(id+"F1.wireOp",EDGE,"E110.MirrorCS"),sQuery(id+"F1.wireOp",EDGE,"E111.MirrorCS"),sQuery(id+"F1.wireOp",EDGE,"E112.MirrorCS"),sQuery(id+"F1.wireOp",EDGE,"E113.MirrorCS"),sQuery(id+"F1.wireOp",EDGE,"E128.MirrorCS"),sQuery(id+"F1.wireOp",EDGE,"E129.MirrorCS"),sQuery(id+"F1.wireOp",EDGE,"E130.MirrorCS"),sQuery(id+"F1.wireOp",EDGE,"E131.MirrorCS"),sQuery(id+"F1.wireOp",EDGE,"E132.MirrorCS"),sQuery(id+"F1.wireOp",EDGE,"E133.MirrorCS"),sQuery(id+"F1.wireOp",EDGE,"E134.MirrorCS"),sQuery(id+"F1.wireOp",EDGE,"E135.MirrorCS"),sQuery(id+"F1.wireOp",EDGE,"E136.MirrorCS"),sQuery(id+"F1.wireOp",EDGE,"E137.MirrorCS"),sQuery(id+"F1.wireOp",EDGE,"E138.MirrorCS"),sQuery(id+"F1.wireOp",EDGE,"E139.MirrorCS"),sQuery(id+"F1.wireOp",EDGE,"E140.MirrorCS"),sQuery(id+"F1.wireOp",EDGE,"E141.MirrorCS"),sQuery(id+"F1.wireOp",EDGE,"E142.MirrorCS"),sQuery(id+"F1.wireOp",EDGE,"E143.MirrorCS"),sQuery(id+"F1.wireOp",EDGE,"E144.MirrorCS"),sQuery(id+"F1.wireOp",EDGE,"E145.MirrorCS"),sQuery(id+"F1.wireOp",EDGE,"E146.MirrorCS"),sQuery(id+"F1.wireOp",EDGE,"E147.MirrorCS"),sQuery(id+"F1.wireOp",EDGE,"E148.MirrorCS"),sQuery(id+"F1.wireOp",EDGE,"E149.MirrorCS"),sQuery(id+"F1.wireOp",EDGE,"E150.MirrorCS"),sQuery(id+"F1.wireOp",EDGE,"E151.MirrorCS"),sQuery(id+"F1.wireOp",EDGE,"E152.MirrorCS"),sQuery(id+"F1.wireOp",EDGE,"E153.MirrorCS"),sQuery(id+"F1.wireOp",EDGE,"E154.MirrorCS"),sQuery(id+"F1.wireOp",EDGE,"E156.MirrorCS")])],"isStart":false});
            var sketch = newSketch(context, id + "F6", { "sketchPlane" : qUnion([Q0])});
            skCircle(sketch, "E184", {"center": v(0, 0) * mm, "radius": 25 * mm});
            skSolve(sketch);
        }
        {
            var Q0;
            Q0=qSketchRegion(id+"F6",true);
            extrude(context, id + "F7", {"entities" : qUnion([Q0]), "operationType" : NewBodyOperationType.ADD, "depth" : 5 * mm, "offsetDistance" : 25 * mm});
        }
        {
            var Q0;
            Q0=makeQuery(id+"F5.opExtrude","CAP_FACE",FACE,{"disambiguationData":[OSD([sQuery(id+"F4.wireOp",EDGE,"E183")])],"isStart":false});
            var sketch = newSketch(context, id + "F8", { "sketchPlane" : qUnion([Q0])});
            skCircle(sketch, "E185", {"center": v(0, 0) * mm, "radius": 12.5 * mm});
            skSolve(sketch);
        }
        {
            var Q0;
            Q0=qSketchRegion(id+"F8",true);
            extrude(context, id + "F9", {"entities" : qUnion([Q0]), "operationType" : NewBodyOperationType.REMOVE, "oppositeDirection" : true, "depth" : 106.9 * mm, "offsetDistance" : 25 * mm});
        }
        {
            var Q0;
            Q0=qCreatedBy(makeId("Front.planeOp"),FACE);
            var sketch = newSketch(context, id + "F10", { "sketchPlane" : qUnion([Q0])});
            skCircle(sketch, "E186", {"center": v(0, 0) * mm, "radius": 12.5 * mm});
            skLineSegment(sketch, "E187", {"start": v(0, 0) * mm, "end": v(0, 12.5) * mm});
            skLineSegment(sketch, "E188", {"start": v(0, 0) * mm, "end": v(0, -12.5) * mm});
            skLineSegment(sketch, "E189", {"start": v(0, 0) * mm, "end": v(12.5, 0) * mm});
            skLineSegment(sketch, "E190", {"start": v(0, 0) * mm, "end": v(-12.5, 0) * mm});
            skPoint(sketch, "E191", {"position": v(0, 2.5) * mm});
            skPoint(sketch, "E192", {"position": v(0, -2.5) * mm});
            skPoint(sketch, "E193", {"position": v(2.5, 0) * mm});
            skPoint(sketch, "E194", {"position": v(-2.5, 0) * mm});
            skLineSegment(sketch, "E195", {"start": v(0, 2.5) * mm, "end": v(-12.25, 2.5) * mm});
            skLineSegment(sketch, "E196", {"start": v(-12.25, 2.5) * mm, "end": v(12.25, 2.5) * mm});
            skLineSegment(sketch, "E197", {"start": v(0, -2.5) * mm, "end": v(12.25, -2.5) * mm});
            skLineSegment(sketch, "E198", {"start": v(12.25, -2.5) * mm, "end": v(-12.25, -2.5) * mm});
            skLineSegment(sketch, "E199", {"start": v(-2.5, 0) * mm, "end": v(-2.5, 12.25) * mm});
            skLineSegment(sketch, "E200", {"start": v(-2.5, 12.25) * mm, "end": v(-2.5, -12.25) * mm});
            skLineSegment(sketch, "E201", {"start": v(2.5, 0) * mm, "end": v(2.5, 12.25) * mm});
            skLineSegment(sketch, "E202", {"start": v(2.5, 12.25) * mm, "end": v(2.5, -12.25) * mm});
            skSolve(sketch);
        }
        {
            var Q0;
            {var subQ0=sQuery(id+"F10.wireOp",EDGE,"E187");var subQ1=sQuery(id+"F10.wireOp",EDGE,"E186");var subQ2=makeQuery(id+"F10.imprint","INTERSECT",VERTEX,{"derivedFrom":[subQ1,subQ0]});Q0=makeQuery(id+"F10.imprint","IMPRINT",FACE,{"disambiguationData":[TD([[makeQuery(id+"F10.imprint","IMPRINT",EDGE,{"disambiguationData":[TD([[subQ2,-1.0]])],"derivedFrom":subQ1}),1.0]])]});}
            var Q1;
            {var subQ0=sQuery(id+"F10.wireOp",EDGE,"E201");var subQ1=sQuery(id+"F10.wireOp",EDGE,"E186");var subQ2=makeQuery(id+"F10.imprint","INTERSECT",VERTEX,{"derivedFrom":[subQ1,subQ0]});Q1=makeQuery(id+"F10.imprint","IMPRINT",FACE,{"disambiguationData":[TD([[makeQuery(id+"F10.imprint","IMPRINT",EDGE,{"disambiguationData":[TD([[subQ2,-1.0]])],"derivedFrom":subQ1}),1.0]])]});}
            var Q2;
            {var subQ0=sQuery(id+"F10.wireOp",EDGE,"E196");var subQ5=sQuery(id+"F10.wireOp",EDGE,"E201");var subQ6=makeQuery(id+"F10.imprint","INTERSECT",VERTEX,{"derivedFrom":[subQ0,subQ5]});Q2=makeQuery(id+"F10.imprint","IMPRINT",FACE,{"disambiguationData":[TD([[makeQuery(id+"F10.imprint","IMPRINT",EDGE,{"disambiguationData":[TD([[subQ6,1.0]])],"derivedFrom":subQ0}),-1.0]])]});}
            var Q3;
            {var subQ0=sQuery(id+"F10.wireOp",EDGE,"E189");var subQ1=sQuery(id+"F10.wireOp",EDGE,"E186");var subQ2=makeQuery(id+"F10.imprint","INTERSECT",VERTEX,{"derivedFrom":[subQ1,subQ0]});Q3=makeQuery(id+"F10.imprint","IMPRINT",FACE,{"disambiguationData":[TD([[makeQuery(id+"F10.imprint","IMPRINT",EDGE,{"disambiguationData":[TD([[subQ2,-1.0]])],"derivedFrom":subQ1}),1.0]])]});}
            var Q4;
            {var subQ0=sQuery(id+"F10.wireOp",EDGE,"E197");var subQ1=sQuery(id+"F10.wireOp",EDGE,"E186");var subQ2=makeQuery(id+"F10.imprint","INTERSECT",VERTEX,{"derivedFrom":[subQ1,subQ0]});Q4=makeQuery(id+"F10.imprint","IMPRINT",FACE,{"disambiguationData":[TD([[makeQuery(id+"F10.imprint","IMPRINT",EDGE,{"disambiguationData":[TD([[subQ2,-1.0]])],"derivedFrom":subQ1}),1.0]])]});}
            var Q5;
            {var subQ0=sQuery(id+"F10.wireOp",EDGE,"E197");var subQ5=sQuery(id+"F10.wireOp",EDGE,"E202");var subQ6=makeQuery(id+"F10.imprint","INTERSECT",VERTEX,{"derivedFrom":[subQ0,subQ5]});Q5=makeQuery(id+"F10.imprint","IMPRINT",FACE,{"disambiguationData":[TD([[makeQuery(id+"F10.imprint","IMPRINT",EDGE,{"disambiguationData":[TD([[subQ6,1.0]])],"derivedFrom":subQ0}),1.0]])]});}
            var Q6;
            {var subQ0=sQuery(id+"F10.wireOp",EDGE,"E198");var subQ5=sQuery(id+"F10.wireOp",EDGE,"E200");var subQ7=makeQuery(id+"F10.imprint","INTERSECT",VERTEX,{"derivedFrom":[subQ0,subQ5]});Q6=makeQuery(id+"F10.imprint","IMPRINT",FACE,{"disambiguationData":[TD([[makeQuery(id+"F10.imprint","IMPRINT",EDGE,{"disambiguationData":[TD([[subQ7,1.0]])],"derivedFrom":subQ0}),-1.0]])]});}
            var Q7;
            {var subQ0=sQuery(id+"F10.wireOp",EDGE,"E195");var subQ5=sQuery(id+"F10.wireOp",EDGE,"E199");var subQ7=makeQuery(id+"F10.imprint","INTERSECT",VERTEX,{"derivedFrom":[subQ0,subQ5]});Q7=makeQuery(id+"F10.imprint","IMPRINT",FACE,{"disambiguationData":[TD([[makeQuery(id+"F10.imprint","IMPRINT",EDGE,{"disambiguationData":[TD([[subQ7,1.0]])],"derivedFrom":subQ0}),1.0]])]});}
            var Q8;
            {var subQ0=sQuery(id+"F10.wireOp",EDGE,"E195");var subQ1=sQuery(id+"F10.wireOp",EDGE,"E186");var subQ2=makeQuery(id+"F10.imprint","INTERSECT",VERTEX,{"derivedFrom":[subQ1,subQ0]});Q8=makeQuery(id+"F10.imprint","IMPRINT",FACE,{"disambiguationData":[TD([[makeQuery(id+"F10.imprint","IMPRINT",EDGE,{"disambiguationData":[TD([[subQ2,-1.0]])],"derivedFrom":subQ1}),1.0]])]});}
            var Q9;
            {var subQ0=sQuery(id+"F10.wireOp",EDGE,"E190");var subQ1=sQuery(id+"F10.wireOp",EDGE,"E186");var subQ2=makeQuery(id+"F10.imprint","INTERSECT",VERTEX,{"derivedFrom":[subQ1,subQ0]});Q9=makeQuery(id+"F10.imprint","IMPRINT",FACE,{"disambiguationData":[TD([[makeQuery(id+"F10.imprint","IMPRINT",EDGE,{"disambiguationData":[TD([[subQ2,-1.0]])],"derivedFrom":subQ1}),1.0]])]});}
            var Q10;
            {var subQ0=sQuery(id+"F10.wireOp",EDGE,"E188");var subQ1=sQuery(id+"F10.wireOp",EDGE,"E186");var subQ2=makeQuery(id+"F10.imprint","INTERSECT",VERTEX,{"derivedFrom":[subQ1,subQ0]});Q10=makeQuery(id+"F10.imprint","IMPRINT",FACE,{"disambiguationData":[TD([[makeQuery(id+"F10.imprint","IMPRINT",EDGE,{"disambiguationData":[TD([[subQ2,1.0]])],"derivedFrom":subQ1}),1.0]])]});}
            var Q11;
            {var subQ0=sQuery(id+"F10.wireOp",EDGE,"E202");var subQ1=sQuery(id+"F10.wireOp",EDGE,"E186");var subQ2=makeQuery(id+"F10.imprint","INTERSECT",VERTEX,{"derivedFrom":[subQ1,subQ0]});Q11=makeQuery(id+"F10.imprint","IMPRINT",FACE,{"disambiguationData":[TD([[makeQuery(id+"F10.imprint","IMPRINT",EDGE,{"disambiguationData":[TD([[subQ2,1.0]])],"derivedFrom":subQ1}),1.0]])]});}
            extrude(context, id + "F11", {"entities" : qUnion([Q0, Q1, Q2, Q3, Q4, Q5, Q6, Q7, Q8, Q9, Q10, Q11]), "operationType" : NewBodyOperationType.ADD, "oppositeDirection" : true, "depth" : 2.5 * mm, "offsetDistance" : 25 * mm});
        }
        {
            var Q0;
            Q0=makeQuery(id+"F7.opExtrude","CAP_FACE",FACE,{"disambiguationData":[OSD([sQuery(id+"F6.wireOp",EDGE,"E184")])],"isStart":false});
            var sketch = newSketch(context, id + "F12", { "sketchPlane" : qUnion([Q0])});
            skLineSegment(sketch, "E203", {"start": v(0, 0) * mm, "end": v(15, 0) * mm});
            skLineSegment(sketch, "E204", {"start": v(0, 0) * mm, "end": v(0, 15) * mm});
            skLineSegment(sketch, "E205", {"start": v(0, 0) * mm, "end": v(0, -15) * mm});
            skLineSegment(sketch, "E206", {"start": v(0, 0) * mm, "end": v(-15, 0) * mm});
            skCircle(sketch, "E207", {"center": v(0, 0) * mm, "radius": 15 * mm});
            skPoint(sketch, "E208", {"position": v(0, 2.5) * mm});
            skPoint(sketch, "E209", {"position": v(0, -2.5) * mm});
            skPoint(sketch, "E210", {"position": v(-2.5, 0) * mm});
            skPoint(sketch, "E211", {"position": v(2.5, 0) * mm});
            skLineSegment(sketch, "E212", {"start": v(-2.5, 0) * mm, "end": v(-2.5, -14.8) * mm});
            skLineSegment(sketch, "E213", {"start": v(-2.5, -14.8) * mm, "end": v(-2.5, 14.8) * mm});
            skLineSegment(sketch, "E214", {"start": v(2.5, 0) * mm, "end": v(2.5, -14.8) * mm});
            skLineSegment(sketch, "E215", {"start": v(2.5, 0) * mm, "end": v(2.5, 14.8) * mm});
            skLineSegment(sketch, "E216", {"start": v(0, 2.5) * mm, "end": v(-14.8, 2.5) * mm});
            skLineSegment(sketch, "E217", {"start": v(-14.8, 2.5) * mm, "end": v(14.8, 2.5) * mm});
            skLineSegment(sketch, "E218", {"start": v(0, -2.5) * mm, "end": v(-14.8, -2.5) * mm});
            skLineSegment(sketch, "E219", {"start": v(-14.8, -2.5) * mm, "end": v(14.8, -2.5) * mm});
            skCircle(sketch, "E220", {"center": v(0, 0) * mm, "radius": 12.5 * mm});
            skCircle(sketch, "E221", {"center": v(0, 0) * mm, "radius": 2.5 * mm});
            skSolve(sketch);
        }
        {
            var Q0;
            Q0=makeQuery(id+"F2.opExtrude","CAP_FACE",FACE,{"disambiguationData":[OSD([sQuery(id+"F1.wireOp",EDGE,"E86"),sQuery(id+"F1.wireOp",EDGE,"E87"),sQuery(id+"F1.wireOp",EDGE,"E88"),sQuery(id+"F1.wireOp",EDGE,"E89"),sQuery(id+"F1.wireOp",EDGE,"E90"),sQuery(id+"F1.wireOp",EDGE,"E91"),sQuery(id+"F1.wireOp",EDGE,"E92"),sQuery(id+"F1.wireOp",EDGE,"E93"),sQuery(id+"F1.wireOp",EDGE,"E94"),sQuery(id+"F1.wireOp",EDGE,"E95"),sQuery(id+"F1.wireOp",EDGE,"E96"),sQuery(id+"F1.wireOp",EDGE,"E97"),sQuery(id+"F1.wireOp",EDGE,"E98"),sQuery(id+"F1.wireOp",EDGE,"E99"),sQuery(id+"F1.wireOp",EDGE,"E100.MirrorCS"),sQuery(id+"F1.wireOp",EDGE,"E101.MirrorCS"),sQuery(id+"F1.wireOp",EDGE,"E102.MirrorCS"),sQuery(id+"F1.wireOp",EDGE,"E103.MirrorCS"),sQuery(id+"F1.wireOp",EDGE,"E104.MirrorCS"),sQuery(id+"F1.wireOp",EDGE,"E105.MirrorCS"),sQuery(id+"F1.wireOp",EDGE,"E106.MirrorCS"),sQuery(id+"F1.wireOp",EDGE,"E107.MirrorCS"),sQuery(id+"F1.wireOp",EDGE,"E108.MirrorCS"),sQuery(id+"F1.wireOp",EDGE,"E109.MirrorCS"),sQuery(id+"F1.wireOp",EDGE,"E110.MirrorCS"),sQuery(id+"F1.wireOp",EDGE,"E111.MirrorCS"),sQuery(id+"F1.wireOp",EDGE,"E112.MirrorCS"),sQuery(id+"F1.wireOp",EDGE,"E113.MirrorCS"),sQuery(id+"F1.wireOp",EDGE,"E128.MirrorCS"),sQuery(id+"F1.wireOp",EDGE,"E129.MirrorCS"),sQuery(id+"F1.wireOp",EDGE,"E130.MirrorCS"),sQuery(id+"F1.wireOp",EDGE,"E131.MirrorCS"),sQuery(id+"F1.wireOp",EDGE,"E132.MirrorCS"),sQuery(id+"F1.wireOp",EDGE,"E133.MirrorCS"),sQuery(id+"F1.wireOp",EDGE,"E134.MirrorCS"),sQuery(id+"F1.wireOp",EDGE,"E135.MirrorCS"),sQuery(id+"F1.wireOp",EDGE,"E136.MirrorCS"),sQuery(id+"F1.wireOp",EDGE,"E137.MirrorCS"),sQuery(id+"F1.wireOp",EDGE,"E138.MirrorCS"),sQuery(id+"F1.wireOp",EDGE,"E139.MirrorCS"),sQuery(id+"F1.wireOp",EDGE,"E140.MirrorCS"),sQuery(id+"F1.wireOp",EDGE,"E141.MirrorCS"),sQuery(id+"F1.wireOp",EDGE,"E142.MirrorCS"),sQuery(id+"F1.wireOp",EDGE,"E143.MirrorCS"),sQuery(id+"F1.wireOp",EDGE,"E144.MirrorCS"),sQuery(id+"F1.wireOp",EDGE,"E145.MirrorCS"),sQuery(id+"F1.wireOp",EDGE,"E146.MirrorCS"),sQuery(id+"F1.wireOp",EDGE,"E147.MirrorCS"),sQuery(id+"F1.wireOp",EDGE,"E148.MirrorCS"),sQuery(id+"F1.wireOp",EDGE,"E149.MirrorCS"),sQuery(id+"F1.wireOp",EDGE,"E150.MirrorCS"),sQuery(id+"F1.wireOp",EDGE,"E151.MirrorCS"),sQuery(id+"F1.wireOp",EDGE,"E152.MirrorCS"),sQuery(id+"F1.wireOp",EDGE,"E153.MirrorCS"),sQuery(id+"F1.wireOp",EDGE,"E154.MirrorCS"),sQuery(id+"F1.wireOp",EDGE,"E156.MirrorCS")])],"isStart":false});
            var sketch = newSketch(context, id + "F13", { "sketchPlane" : qUnion([Q0])});
            skLineSegment(sketch, "E222", {"start": v(-35.26, 12.47) * mm, "end": v(-35.26, -20.77) * mm});
            skLineSegment(sketch, "E223", {"start": v(-34.02, -20.97) * mm, "end": v(0, -36.71) * mm});
            skLineSegment(sketch, "E224", {"start": v(1.03, -36.9) * mm, "end": v(33.89, 0) * mm});
            skLineSegment(sketch, "E225", {"start": v(34.02, -0.16) * mm, "end": v(18.63, 35.8) * mm});
            skLineSegment(sketch, "E226", {"start": v(17.94, 36) * mm, "end": v(-32.92, 23.36) * mm});
            skLineSegment(sketch, "E227", {"start": v(-32.92, 23.36) * mm, "end": v(-35.26, 12.47) * mm});
            skSolve(sketch);
        }
        {
            var Q0;
            Q0=makeQuery(id+"F13.imprint","IMPRINT",FACE,{"disambiguationData":[TD([[makeQuery(id+"F13.imprint","IMPRINT",EDGE,{"derivedFrom":makeQuery(id+"F2.opExtrude","CAP_EDGE",EDGE,{"disambiguationData":[OSD([sQuery(id+"F1.wireOp",EDGE,"E86")])],"isStart":false})}),-1.0]])]});
            extrude(context, id + "F14", {"entities" : qUnion([Q0]), "operationType" : NewBodyOperationType.ADD, "depth" : 25 * mm, "offsetDistance" : 25 * mm});
        }
        {
            var Q0;
            {var subQ0=sQuery(id+"F1.wireOp",EDGE,"E104.MirrorCS");var subQ1=sQuery(id+"F1.wireOp",EDGE,"E101.MirrorCS");var subQ2=sQuery(id+"F1.wireOp",EDGE,"E110.MirrorCS");var subQ3=sQuery(id+"F0.wireOp",EDGE,"E0");var subQ4=sQuery(id+"F1.wireOp",EDGE,"E111.MirrorCS");Q0=makeQuery(id+"F3.boolean.opBoolean","SPLIT",EDGE,{"disambiguationData":[TD([makeQuery(id+"F2.opExtrude","CAP_FACE",FACE,{"disambiguationData":[OSD([sQuery(id+"F1.wireOp",EDGE,"E86"),sQuery(id+"F1.wireOp",EDGE,"E87"),sQuery(id+"F1.wireOp",EDGE,"E88"),sQuery(id+"F1.wireOp",EDGE,"E89"),sQuery(id+"F1.wireOp",EDGE,"E90"),sQuery(id+"F1.wireOp",EDGE,"E91"),sQuery(id+"F1.wireOp",EDGE,"E92"),sQuery(id+"F1.wireOp",EDGE,"E93"),sQuery(id+"F1.wireOp",EDGE,"E94"),sQuery(id+"F1.wireOp",EDGE,"E95"),sQuery(id+"F1.wireOp",EDGE,"E96"),sQuery(id+"F1.wireOp",EDGE,"E97"),sQuery(id+"F1.wireOp",EDGE,"E98"),sQuery(id+"F1.wireOp",EDGE,"E99"),sQuery(id+"F1.wireOp",EDGE,"E100.MirrorCS"),subQ1,sQuery(id+"F1.wireOp",EDGE,"E102.MirrorCS"),sQuery(id+"F1.wireOp",EDGE,"E103.MirrorCS"),subQ0,sQuery(id+"F1.wireOp",EDGE,"E105.MirrorCS"),sQuery(id+"F1.wireOp",EDGE,"E106.MirrorCS"),sQuery(id+"F1.wireOp",EDGE,"E107.MirrorCS"),sQuery(id+"F1.wireOp",EDGE,"E108.MirrorCS"),sQuery(id+"F1.wireOp",EDGE,"E109.MirrorCS"),subQ2,subQ4,sQuery(id+"F1.wireOp",EDGE,"E112.MirrorCS"),sQuery(id+"F1.wireOp",EDGE,"E113.MirrorCS"),sQuery(id+"F1.wireOp",EDGE,"E128.MirrorCS"),sQuery(id+"F1.wireOp",EDGE,"E129.MirrorCS"),sQuery(id+"F1.wireOp",EDGE,"E130.MirrorCS"),sQuery(id+"F1.wireOp",EDGE,"E131.MirrorCS"),sQuery(id+"F1.wireOp",EDGE,"E132.MirrorCS"),sQuery(id+"F1.wireOp",EDGE,"E133.MirrorCS"),sQuery(id+"F1.wireOp",EDGE,"E134.MirrorCS"),sQuery(id+"F1.wireOp",EDGE,"E135.MirrorCS"),sQuery(id+"F1.wireOp",EDGE,"E136.MirrorCS"),sQuery(id+"F1.wireOp",EDGE,"E137.MirrorCS"),sQuery(id+"F1.wireOp",EDGE,"E138.MirrorCS"),sQuery(id+"F1.wireOp",EDGE,"E139.MirrorCS"),sQuery(id+"F1.wireOp",EDGE,"E140.MirrorCS"),sQuery(id+"F1.wireOp",EDGE,"E141.MirrorCS"),sQuery(id+"F1.wireOp",EDGE,"E142.MirrorCS"),sQuery(id+"F1.wireOp",EDGE,"E143.MirrorCS"),sQuery(id+"F1.wireOp",EDGE,"E144.MirrorCS"),sQuery(id+"F1.wireOp",EDGE,"E145.MirrorCS"),sQuery(id+"F1.wireOp",EDGE,"E146.MirrorCS"),sQuery(id+"F1.wireOp",EDGE,"E147.MirrorCS"),sQuery(id+"F1.wireOp",EDGE,"E148.MirrorCS"),sQuery(id+"F1.wireOp",EDGE,"E149.MirrorCS"),sQuery(id+"F1.wireOp",EDGE,"E150.MirrorCS"),sQuery(id+"F1.wireOp",EDGE,"E151.MirrorCS"),sQuery(id+"F1.wireOp",EDGE,"E152.MirrorCS"),sQuery(id+"F1.wireOp",EDGE,"E153.MirrorCS"),sQuery(id+"F1.wireOp",EDGE,"E154.MirrorCS"),sQuery(id+"F1.wireOp",EDGE,"E156.MirrorCS")])],"isStart":true}),makeQuery(id+"F2.opExtrude","SWEPT_FACE",FACE,{"disambiguationData":[OSD([subQ1])]}),makeQuery(id+"F2.opExtrude","SWEPT_FACE",FACE,{"disambiguationData":[OSD([subQ0])]}),makeQuery(id+"F2.opExtrude","SWEPT_FACE",FACE,{"disambiguationData":[OSD([subQ2])]}),makeQuery(id+"F2.opExtrude","SWEPT_FACE",FACE,{"disambiguationData":[OSD([subQ4])]}),makeQuery(id+"F3.opExtrude","SWEPT_FACE",FACE,{"disambiguationData":[OSD([subQ3])]})])],"derivedFrom":makeQuery(id+"F3.opExtrude","CAP_EDGE",EDGE,{"disambiguationData":[OSD([subQ3])],"isStart":true})});}
            var Q1;
            {var subQ0=sQuery(id+"F1.wireOp",EDGE,"E111.MirrorCS");var subQ1=sQuery(id+"F1.wireOp",EDGE,"E106.MirrorCS");var subQ2=sQuery(id+"F1.wireOp",EDGE,"E101.MirrorCS");var subQ3=sQuery(id+"F1.wireOp",EDGE,"E112.MirrorCS");var subQ4=sQuery(id+"F0.wireOp",EDGE,"E0");Q1=makeQuery(id+"F3.boolean.opBoolean","SPLIT",EDGE,{"disambiguationData":[TD([makeQuery(id+"F2.opExtrude","CAP_FACE",FACE,{"disambiguationData":[OSD([sQuery(id+"F1.wireOp",EDGE,"E86"),sQuery(id+"F1.wireOp",EDGE,"E87"),sQuery(id+"F1.wireOp",EDGE,"E88"),sQuery(id+"F1.wireOp",EDGE,"E89"),sQuery(id+"F1.wireOp",EDGE,"E90"),sQuery(id+"F1.wireOp",EDGE,"E91"),sQuery(id+"F1.wireOp",EDGE,"E92"),sQuery(id+"F1.wireOp",EDGE,"E93"),sQuery(id+"F1.wireOp",EDGE,"E94"),sQuery(id+"F1.wireOp",EDGE,"E95"),sQuery(id+"F1.wireOp",EDGE,"E96"),sQuery(id+"F1.wireOp",EDGE,"E97"),sQuery(id+"F1.wireOp",EDGE,"E98"),sQuery(id+"F1.wireOp",EDGE,"E99"),sQuery(id+"F1.wireOp",EDGE,"E100.MirrorCS"),subQ2,sQuery(id+"F1.wireOp",EDGE,"E102.MirrorCS"),sQuery(id+"F1.wireOp",EDGE,"E103.MirrorCS"),sQuery(id+"F1.wireOp",EDGE,"E104.MirrorCS"),sQuery(id+"F1.wireOp",EDGE,"E105.MirrorCS"),subQ1,sQuery(id+"F1.wireOp",EDGE,"E107.MirrorCS"),sQuery(id+"F1.wireOp",EDGE,"E108.MirrorCS"),sQuery(id+"F1.wireOp",EDGE,"E109.MirrorCS"),sQuery(id+"F1.wireOp",EDGE,"E110.MirrorCS"),subQ0,subQ3,sQuery(id+"F1.wireOp",EDGE,"E113.MirrorCS"),sQuery(id+"F1.wireOp",EDGE,"E128.MirrorCS"),sQuery(id+"F1.wireOp",EDGE,"E129.MirrorCS"),sQuery(id+"F1.wireOp",EDGE,"E130.MirrorCS"),sQuery(id+"F1.wireOp",EDGE,"E131.MirrorCS"),sQuery(id+"F1.wireOp",EDGE,"E132.MirrorCS"),sQuery(id+"F1.wireOp",EDGE,"E133.MirrorCS"),sQuery(id+"F1.wireOp",EDGE,"E134.MirrorCS"),sQuery(id+"F1.wireOp",EDGE,"E135.MirrorCS"),sQuery(id+"F1.wireOp",EDGE,"E136.MirrorCS"),sQuery(id+"F1.wireOp",EDGE,"E137.MirrorCS"),sQuery(id+"F1.wireOp",EDGE,"E138.MirrorCS"),sQuery(id+"F1.wireOp",EDGE,"E139.MirrorCS"),sQuery(id+"F1.wireOp",EDGE,"E140.MirrorCS"),sQuery(id+"F1.wireOp",EDGE,"E141.MirrorCS"),sQuery(id+"F1.wireOp",EDGE,"E142.MirrorCS"),sQuery(id+"F1.wireOp",EDGE,"E143.MirrorCS"),sQuery(id+"F1.wireOp",EDGE,"E144.MirrorCS"),sQuery(id+"F1.wireOp",EDGE,"E145.MirrorCS"),sQuery(id+"F1.wireOp",EDGE,"E146.MirrorCS"),sQuery(id+"F1.wireOp",EDGE,"E147.MirrorCS"),sQuery(id+"F1.wireOp",EDGE,"E148.MirrorCS"),sQuery(id+"F1.wireOp",EDGE,"E149.MirrorCS"),sQuery(id+"F1.wireOp",EDGE,"E150.MirrorCS"),sQuery(id+"F1.wireOp",EDGE,"E151.MirrorCS"),sQuery(id+"F1.wireOp",EDGE,"E152.MirrorCS"),sQuery(id+"F1.wireOp",EDGE,"E153.MirrorCS"),sQuery(id+"F1.wireOp",EDGE,"E154.MirrorCS"),sQuery(id+"F1.wireOp",EDGE,"E156.MirrorCS")])],"isStart":true}),makeQuery(id+"F2.opExtrude","SWEPT_FACE",FACE,{"disambiguationData":[OSD([subQ2])]}),makeQuery(id+"F2.opExtrude","SWEPT_FACE",FACE,{"disambiguationData":[OSD([subQ1])]}),makeQuery(id+"F2.opExtrude","SWEPT_FACE",FACE,{"disambiguationData":[OSD([subQ0])]}),makeQuery(id+"F2.opExtrude","SWEPT_FACE",FACE,{"disambiguationData":[OSD([subQ3])]}),makeQuery(id+"F3.opExtrude","SWEPT_FACE",FACE,{"disambiguationData":[OSD([subQ4])]})])],"derivedFrom":makeQuery(id+"F3.opExtrude","CAP_EDGE",EDGE,{"disambiguationData":[OSD([subQ4])],"isStart":true})});}
            var Q2;
            {var subQ0=sQuery(id+"F1.wireOp",EDGE,"E106.MirrorCS");var subQ1=sQuery(id+"F1.wireOp",EDGE,"E102.MirrorCS");var subQ2=sQuery(id+"F1.wireOp",EDGE,"E105.MirrorCS");var subQ3=sQuery(id+"F1.wireOp",EDGE,"E112.MirrorCS");var subQ4=sQuery(id+"F0.wireOp",EDGE,"E0");Q2=makeQuery(id+"F3.boolean.opBoolean","SPLIT",EDGE,{"disambiguationData":[TD([makeQuery(id+"F2.opExtrude","CAP_FACE",FACE,{"disambiguationData":[OSD([sQuery(id+"F1.wireOp",EDGE,"E86"),sQuery(id+"F1.wireOp",EDGE,"E87"),sQuery(id+"F1.wireOp",EDGE,"E88"),sQuery(id+"F1.wireOp",EDGE,"E89"),sQuery(id+"F1.wireOp",EDGE,"E90"),sQuery(id+"F1.wireOp",EDGE,"E91"),sQuery(id+"F1.wireOp",EDGE,"E92"),sQuery(id+"F1.wireOp",EDGE,"E93"),sQuery(id+"F1.wireOp",EDGE,"E94"),sQuery(id+"F1.wireOp",EDGE,"E95"),sQuery(id+"F1.wireOp",EDGE,"E96"),sQuery(id+"F1.wireOp",EDGE,"E97"),sQuery(id+"F1.wireOp",EDGE,"E98"),sQuery(id+"F1.wireOp",EDGE,"E99"),sQuery(id+"F1.wireOp",EDGE,"E100.MirrorCS"),sQuery(id+"F1.wireOp",EDGE,"E101.MirrorCS"),subQ1,sQuery(id+"F1.wireOp",EDGE,"E103.MirrorCS"),sQuery(id+"F1.wireOp",EDGE,"E104.MirrorCS"),subQ2,subQ0,sQuery(id+"F1.wireOp",EDGE,"E107.MirrorCS"),sQuery(id+"F1.wireOp",EDGE,"E108.MirrorCS"),sQuery(id+"F1.wireOp",EDGE,"E109.MirrorCS"),sQuery(id+"F1.wireOp",EDGE,"E110.MirrorCS"),sQuery(id+"F1.wireOp",EDGE,"E111.MirrorCS"),subQ3,sQuery(id+"F1.wireOp",EDGE,"E113.MirrorCS"),sQuery(id+"F1.wireOp",EDGE,"E128.MirrorCS"),sQuery(id+"F1.wireOp",EDGE,"E129.MirrorCS"),sQuery(id+"F1.wireOp",EDGE,"E130.MirrorCS"),sQuery(id+"F1.wireOp",EDGE,"E131.MirrorCS"),sQuery(id+"F1.wireOp",EDGE,"E132.MirrorCS"),sQuery(id+"F1.wireOp",EDGE,"E133.MirrorCS"),sQuery(id+"F1.wireOp",EDGE,"E134.MirrorCS"),sQuery(id+"F1.wireOp",EDGE,"E135.MirrorCS"),sQuery(id+"F1.wireOp",EDGE,"E136.MirrorCS"),sQuery(id+"F1.wireOp",EDGE,"E137.MirrorCS"),sQuery(id+"F1.wireOp",EDGE,"E138.MirrorCS"),sQuery(id+"F1.wireOp",EDGE,"E139.MirrorCS"),sQuery(id+"F1.wireOp",EDGE,"E140.MirrorCS"),sQuery(id+"F1.wireOp",EDGE,"E141.MirrorCS"),sQuery(id+"F1.wireOp",EDGE,"E142.MirrorCS"),sQuery(id+"F1.wireOp",EDGE,"E143.MirrorCS"),sQuery(id+"F1.wireOp",EDGE,"E144.MirrorCS"),sQuery(id+"F1.wireOp",EDGE,"E145.MirrorCS"),sQuery(id+"F1.wireOp",EDGE,"E146.MirrorCS"),sQuery(id+"F1.wireOp",EDGE,"E147.MirrorCS"),sQuery(id+"F1.wireOp",EDGE,"E148.MirrorCS"),sQuery(id+"F1.wireOp",EDGE,"E149.MirrorCS"),sQuery(id+"F1.wireOp",EDGE,"E150.MirrorCS"),sQuery(id+"F1.wireOp",EDGE,"E151.MirrorCS"),sQuery(id+"F1.wireOp",EDGE,"E152.MirrorCS"),sQuery(id+"F1.wireOp",EDGE,"E153.MirrorCS"),sQuery(id+"F1.wireOp",EDGE,"E154.MirrorCS"),sQuery(id+"F1.wireOp",EDGE,"E156.MirrorCS")])],"isStart":true}),makeQuery(id+"F2.opExtrude","SWEPT_FACE",FACE,{"disambiguationData":[OSD([subQ1])]}),makeQuery(id+"F2.opExtrude","SWEPT_FACE",FACE,{"disambiguationData":[OSD([subQ2])]}),makeQuery(id+"F2.opExtrude","SWEPT_FACE",FACE,{"disambiguationData":[OSD([subQ0])]}),makeQuery(id+"F2.opExtrude","SWEPT_FACE",FACE,{"disambiguationData":[OSD([subQ3])]}),makeQuery(id+"F3.opExtrude","SWEPT_FACE",FACE,{"disambiguationData":[OSD([subQ4])]})])],"derivedFrom":makeQuery(id+"F3.opExtrude","CAP_EDGE",EDGE,{"disambiguationData":[OSD([subQ4])],"isStart":true})});}
            var Q3;
            {var subQ0=sQuery(id+"F1.wireOp",EDGE,"E102.MirrorCS");var subQ1=sQuery(id+"F1.wireOp",EDGE,"E105.MirrorCS");var subQ2=sQuery(id+"F1.wireOp",EDGE,"E100.MirrorCS");var subQ3=sQuery(id+"F1.wireOp",EDGE,"E108.MirrorCS");var subQ4=sQuery(id+"F0.wireOp",EDGE,"E0");Q3=makeQuery(id+"F3.boolean.opBoolean","SPLIT",EDGE,{"disambiguationData":[TD([makeQuery(id+"F2.opExtrude","CAP_FACE",FACE,{"disambiguationData":[OSD([sQuery(id+"F1.wireOp",EDGE,"E86"),sQuery(id+"F1.wireOp",EDGE,"E87"),sQuery(id+"F1.wireOp",EDGE,"E88"),sQuery(id+"F1.wireOp",EDGE,"E89"),sQuery(id+"F1.wireOp",EDGE,"E90"),sQuery(id+"F1.wireOp",EDGE,"E91"),sQuery(id+"F1.wireOp",EDGE,"E92"),sQuery(id+"F1.wireOp",EDGE,"E93"),sQuery(id+"F1.wireOp",EDGE,"E94"),sQuery(id+"F1.wireOp",EDGE,"E95"),sQuery(id+"F1.wireOp",EDGE,"E96"),sQuery(id+"F1.wireOp",EDGE,"E97"),sQuery(id+"F1.wireOp",EDGE,"E98"),sQuery(id+"F1.wireOp",EDGE,"E99"),subQ2,sQuery(id+"F1.wireOp",EDGE,"E101.MirrorCS"),subQ0,sQuery(id+"F1.wireOp",EDGE,"E103.MirrorCS"),sQuery(id+"F1.wireOp",EDGE,"E104.MirrorCS"),subQ1,sQuery(id+"F1.wireOp",EDGE,"E106.MirrorCS"),sQuery(id+"F1.wireOp",EDGE,"E107.MirrorCS"),subQ3,sQuery(id+"F1.wireOp",EDGE,"E109.MirrorCS"),sQuery(id+"F1.wireOp",EDGE,"E110.MirrorCS"),sQuery(id+"F1.wireOp",EDGE,"E111.MirrorCS"),sQuery(id+"F1.wireOp",EDGE,"E112.MirrorCS"),sQuery(id+"F1.wireOp",EDGE,"E113.MirrorCS"),sQuery(id+"F1.wireOp",EDGE,"E128.MirrorCS"),sQuery(id+"F1.wireOp",EDGE,"E129.MirrorCS"),sQuery(id+"F1.wireOp",EDGE,"E130.MirrorCS"),sQuery(id+"F1.wireOp",EDGE,"E131.MirrorCS"),sQuery(id+"F1.wireOp",EDGE,"E132.MirrorCS"),sQuery(id+"F1.wireOp",EDGE,"E133.MirrorCS"),sQuery(id+"F1.wireOp",EDGE,"E134.MirrorCS"),sQuery(id+"F1.wireOp",EDGE,"E135.MirrorCS"),sQuery(id+"F1.wireOp",EDGE,"E136.MirrorCS"),sQuery(id+"F1.wireOp",EDGE,"E137.MirrorCS"),sQuery(id+"F1.wireOp",EDGE,"E138.MirrorCS"),sQuery(id+"F1.wireOp",EDGE,"E139.MirrorCS"),sQuery(id+"F1.wireOp",EDGE,"E140.MirrorCS"),sQuery(id+"F1.wireOp",EDGE,"E141.MirrorCS"),sQuery(id+"F1.wireOp",EDGE,"E142.MirrorCS"),sQuery(id+"F1.wireOp",EDGE,"E143.MirrorCS"),sQuery(id+"F1.wireOp",EDGE,"E144.MirrorCS"),sQuery(id+"F1.wireOp",EDGE,"E145.MirrorCS"),sQuery(id+"F1.wireOp",EDGE,"E146.MirrorCS"),sQuery(id+"F1.wireOp",EDGE,"E147.MirrorCS"),sQuery(id+"F1.wireOp",EDGE,"E148.MirrorCS"),sQuery(id+"F1.wireOp",EDGE,"E149.MirrorCS"),sQuery(id+"F1.wireOp",EDGE,"E150.MirrorCS"),sQuery(id+"F1.wireOp",EDGE,"E151.MirrorCS"),sQuery(id+"F1.wireOp",EDGE,"E152.MirrorCS"),sQuery(id+"F1.wireOp",EDGE,"E153.MirrorCS"),sQuery(id+"F1.wireOp",EDGE,"E154.MirrorCS"),sQuery(id+"F1.wireOp",EDGE,"E156.MirrorCS")])],"isStart":true}),makeQuery(id+"F2.opExtrude","SWEPT_FACE",FACE,{"disambiguationData":[OSD([subQ2])]}),makeQuery(id+"F2.opExtrude","SWEPT_FACE",FACE,{"disambiguationData":[OSD([subQ0])]}),makeQuery(id+"F2.opExtrude","SWEPT_FACE",FACE,{"disambiguationData":[OSD([subQ1])]}),makeQuery(id+"F2.opExtrude","SWEPT_FACE",FACE,{"disambiguationData":[OSD([subQ3])]}),makeQuery(id+"F3.opExtrude","SWEPT_FACE",FACE,{"disambiguationData":[OSD([subQ4])]})])],"derivedFrom":makeQuery(id+"F3.opExtrude","CAP_EDGE",EDGE,{"disambiguationData":[OSD([subQ4])],"isStart":true})});}
            var Q4;
            {var subQ0=sQuery(id+"F1.wireOp",EDGE,"E107.MirrorCS");var subQ1=sQuery(id+"F1.wireOp",EDGE,"E113.MirrorCS");var subQ2=sQuery(id+"F1.wireOp",EDGE,"E110.MirrorCS");var subQ3=sQuery(id+"F1.wireOp",EDGE,"E104.MirrorCS");var subQ4=sQuery(id+"F0.wireOp",EDGE,"E0");Q4=makeQuery(id+"F3.boolean.opBoolean","SPLIT",EDGE,{"disambiguationData":[TD([makeQuery(id+"F2.opExtrude","CAP_FACE",FACE,{"disambiguationData":[OSD([sQuery(id+"F1.wireOp",EDGE,"E86"),sQuery(id+"F1.wireOp",EDGE,"E87"),sQuery(id+"F1.wireOp",EDGE,"E88"),sQuery(id+"F1.wireOp",EDGE,"E89"),sQuery(id+"F1.wireOp",EDGE,"E90"),sQuery(id+"F1.wireOp",EDGE,"E91"),sQuery(id+"F1.wireOp",EDGE,"E92"),sQuery(id+"F1.wireOp",EDGE,"E93"),sQuery(id+"F1.wireOp",EDGE,"E94"),sQuery(id+"F1.wireOp",EDGE,"E95"),sQuery(id+"F1.wireOp",EDGE,"E96"),sQuery(id+"F1.wireOp",EDGE,"E97"),sQuery(id+"F1.wireOp",EDGE,"E98"),sQuery(id+"F1.wireOp",EDGE,"E99"),sQuery(id+"F1.wireOp",EDGE,"E100.MirrorCS"),sQuery(id+"F1.wireOp",EDGE,"E101.MirrorCS"),sQuery(id+"F1.wireOp",EDGE,"E102.MirrorCS"),sQuery(id+"F1.wireOp",EDGE,"E103.MirrorCS"),subQ3,sQuery(id+"F1.wireOp",EDGE,"E105.MirrorCS"),sQuery(id+"F1.wireOp",EDGE,"E106.MirrorCS"),subQ0,sQuery(id+"F1.wireOp",EDGE,"E108.MirrorCS"),sQuery(id+"F1.wireOp",EDGE,"E109.MirrorCS"),subQ2,sQuery(id+"F1.wireOp",EDGE,"E111.MirrorCS"),sQuery(id+"F1.wireOp",EDGE,"E112.MirrorCS"),subQ1,sQuery(id+"F1.wireOp",EDGE,"E128.MirrorCS"),sQuery(id+"F1.wireOp",EDGE,"E129.MirrorCS"),sQuery(id+"F1.wireOp",EDGE,"E130.MirrorCS"),sQuery(id+"F1.wireOp",EDGE,"E131.MirrorCS"),sQuery(id+"F1.wireOp",EDGE,"E132.MirrorCS"),sQuery(id+"F1.wireOp",EDGE,"E133.MirrorCS"),sQuery(id+"F1.wireOp",EDGE,"E134.MirrorCS"),sQuery(id+"F1.wireOp",EDGE,"E135.MirrorCS"),sQuery(id+"F1.wireOp",EDGE,"E136.MirrorCS"),sQuery(id+"F1.wireOp",EDGE,"E137.MirrorCS"),sQuery(id+"F1.wireOp",EDGE,"E138.MirrorCS"),sQuery(id+"F1.wireOp",EDGE,"E139.MirrorCS"),sQuery(id+"F1.wireOp",EDGE,"E140.MirrorCS"),sQuery(id+"F1.wireOp",EDGE,"E141.MirrorCS"),sQuery(id+"F1.wireOp",EDGE,"E142.MirrorCS"),sQuery(id+"F1.wireOp",EDGE,"E143.MirrorCS"),sQuery(id+"F1.wireOp",EDGE,"E144.MirrorCS"),sQuery(id+"F1.wireOp",EDGE,"E145.MirrorCS"),sQuery(id+"F1.wireOp",EDGE,"E146.MirrorCS"),sQuery(id+"F1.wireOp",EDGE,"E147.MirrorCS"),sQuery(id+"F1.wireOp",EDGE,"E148.MirrorCS"),sQuery(id+"F1.wireOp",EDGE,"E149.MirrorCS"),sQuery(id+"F1.wireOp",EDGE,"E150.MirrorCS"),sQuery(id+"F1.wireOp",EDGE,"E151.MirrorCS"),sQuery(id+"F1.wireOp",EDGE,"E152.MirrorCS"),sQuery(id+"F1.wireOp",EDGE,"E153.MirrorCS"),sQuery(id+"F1.wireOp",EDGE,"E154.MirrorCS"),sQuery(id+"F1.wireOp",EDGE,"E156.MirrorCS")])],"isStart":true}),makeQuery(id+"F2.opExtrude","SWEPT_FACE",FACE,{"disambiguationData":[OSD([subQ3])]}),makeQuery(id+"F2.opExtrude","SWEPT_FACE",FACE,{"disambiguationData":[OSD([subQ0])]}),makeQuery(id+"F2.opExtrude","SWEPT_FACE",FACE,{"disambiguationData":[OSD([subQ2])]}),makeQuery(id+"F2.opExtrude","SWEPT_FACE",FACE,{"disambiguationData":[OSD([subQ1])]}),makeQuery(id+"F3.opExtrude","SWEPT_FACE",FACE,{"disambiguationData":[OSD([subQ4])]})])],"derivedFrom":makeQuery(id+"F3.opExtrude","CAP_EDGE",EDGE,{"disambiguationData":[OSD([subQ4])],"isStart":true})});}
            var Q5;
            {var subQ0=sQuery(id+"F1.wireOp",EDGE,"E109.MirrorCS");var subQ1=sQuery(id+"F1.wireOp",EDGE,"E107.MirrorCS");var subQ2=sQuery(id+"F1.wireOp",EDGE,"E113.MirrorCS");var subQ3=sQuery(id+"F1.wireOp",EDGE,"E103.MirrorCS");var subQ4=sQuery(id+"F0.wireOp",EDGE,"E0");Q5=makeQuery(id+"F3.boolean.opBoolean","SPLIT",EDGE,{"disambiguationData":[TD([makeQuery(id+"F2.opExtrude","CAP_FACE",FACE,{"disambiguationData":[OSD([sQuery(id+"F1.wireOp",EDGE,"E86"),sQuery(id+"F1.wireOp",EDGE,"E87"),sQuery(id+"F1.wireOp",EDGE,"E88"),sQuery(id+"F1.wireOp",EDGE,"E89"),sQuery(id+"F1.wireOp",EDGE,"E90"),sQuery(id+"F1.wireOp",EDGE,"E91"),sQuery(id+"F1.wireOp",EDGE,"E92"),sQuery(id+"F1.wireOp",EDGE,"E93"),sQuery(id+"F1.wireOp",EDGE,"E94"),sQuery(id+"F1.wireOp",EDGE,"E95"),sQuery(id+"F1.wireOp",EDGE,"E96"),sQuery(id+"F1.wireOp",EDGE,"E97"),sQuery(id+"F1.wireOp",EDGE,"E98"),sQuery(id+"F1.wireOp",EDGE,"E99"),sQuery(id+"F1.wireOp",EDGE,"E100.MirrorCS"),sQuery(id+"F1.wireOp",EDGE,"E101.MirrorCS"),sQuery(id+"F1.wireOp",EDGE,"E102.MirrorCS"),subQ3,sQuery(id+"F1.wireOp",EDGE,"E104.MirrorCS"),sQuery(id+"F1.wireOp",EDGE,"E105.MirrorCS"),sQuery(id+"F1.wireOp",EDGE,"E106.MirrorCS"),subQ1,sQuery(id+"F1.wireOp",EDGE,"E108.MirrorCS"),subQ0,sQuery(id+"F1.wireOp",EDGE,"E110.MirrorCS"),sQuery(id+"F1.wireOp",EDGE,"E111.MirrorCS"),sQuery(id+"F1.wireOp",EDGE,"E112.MirrorCS"),subQ2,sQuery(id+"F1.wireOp",EDGE,"E128.MirrorCS"),sQuery(id+"F1.wireOp",EDGE,"E129.MirrorCS"),sQuery(id+"F1.wireOp",EDGE,"E130.MirrorCS"),sQuery(id+"F1.wireOp",EDGE,"E131.MirrorCS"),sQuery(id+"F1.wireOp",EDGE,"E132.MirrorCS"),sQuery(id+"F1.wireOp",EDGE,"E133.MirrorCS"),sQuery(id+"F1.wireOp",EDGE,"E134.MirrorCS"),sQuery(id+"F1.wireOp",EDGE,"E135.MirrorCS"),sQuery(id+"F1.wireOp",EDGE,"E136.MirrorCS"),sQuery(id+"F1.wireOp",EDGE,"E137.MirrorCS"),sQuery(id+"F1.wireOp",EDGE,"E138.MirrorCS"),sQuery(id+"F1.wireOp",EDGE,"E139.MirrorCS"),sQuery(id+"F1.wireOp",EDGE,"E140.MirrorCS"),sQuery(id+"F1.wireOp",EDGE,"E141.MirrorCS"),sQuery(id+"F1.wireOp",EDGE,"E142.MirrorCS"),sQuery(id+"F1.wireOp",EDGE,"E143.MirrorCS"),sQuery(id+"F1.wireOp",EDGE,"E144.MirrorCS"),sQuery(id+"F1.wireOp",EDGE,"E145.MirrorCS"),sQuery(id+"F1.wireOp",EDGE,"E146.MirrorCS"),sQuery(id+"F1.wireOp",EDGE,"E147.MirrorCS"),sQuery(id+"F1.wireOp",EDGE,"E148.MirrorCS"),sQuery(id+"F1.wireOp",EDGE,"E149.MirrorCS"),sQuery(id+"F1.wireOp",EDGE,"E150.MirrorCS"),sQuery(id+"F1.wireOp",EDGE,"E151.MirrorCS"),sQuery(id+"F1.wireOp",EDGE,"E152.MirrorCS"),sQuery(id+"F1.wireOp",EDGE,"E153.MirrorCS"),sQuery(id+"F1.wireOp",EDGE,"E154.MirrorCS"),sQuery(id+"F1.wireOp",EDGE,"E156.MirrorCS")])],"isStart":true}),makeQuery(id+"F2.opExtrude","SWEPT_FACE",FACE,{"disambiguationData":[OSD([subQ3])]}),makeQuery(id+"F2.opExtrude","SWEPT_FACE",FACE,{"disambiguationData":[OSD([subQ1])]}),makeQuery(id+"F2.opExtrude","SWEPT_FACE",FACE,{"disambiguationData":[OSD([subQ0])]}),makeQuery(id+"F2.opExtrude","SWEPT_FACE",FACE,{"disambiguationData":[OSD([subQ2])]}),makeQuery(id+"F3.opExtrude","SWEPT_FACE",FACE,{"disambiguationData":[OSD([subQ4])]})])],"derivedFrom":makeQuery(id+"F3.opExtrude","CAP_EDGE",EDGE,{"disambiguationData":[OSD([subQ4])],"isStart":true})});}
            var Q6;
            {var subQ0=sQuery(id+"F1.wireOp",EDGE,"E109.MirrorCS");var subQ1=sQuery(id+"F1.wireOp",EDGE,"E103.MirrorCS");var subQ2=sQuery(id+"F1.wireOp",EDGE,"E129.MirrorCS");var subQ3=sQuery(id+"F1.wireOp",EDGE,"E149.MirrorCS");var subQ4=sQuery(id+"F0.wireOp",EDGE,"E0");Q6=makeQuery(id+"F3.boolean.opBoolean","SPLIT",EDGE,{"disambiguationData":[TD([makeQuery(id+"F2.opExtrude","CAP_FACE",FACE,{"disambiguationData":[OSD([sQuery(id+"F1.wireOp",EDGE,"E86"),sQuery(id+"F1.wireOp",EDGE,"E87"),sQuery(id+"F1.wireOp",EDGE,"E88"),sQuery(id+"F1.wireOp",EDGE,"E89"),sQuery(id+"F1.wireOp",EDGE,"E90"),sQuery(id+"F1.wireOp",EDGE,"E91"),sQuery(id+"F1.wireOp",EDGE,"E92"),sQuery(id+"F1.wireOp",EDGE,"E93"),sQuery(id+"F1.wireOp",EDGE,"E94"),sQuery(id+"F1.wireOp",EDGE,"E95"),sQuery(id+"F1.wireOp",EDGE,"E96"),sQuery(id+"F1.wireOp",EDGE,"E97"),sQuery(id+"F1.wireOp",EDGE,"E98"),sQuery(id+"F1.wireOp",EDGE,"E99"),sQuery(id+"F1.wireOp",EDGE,"E100.MirrorCS"),sQuery(id+"F1.wireOp",EDGE,"E101.MirrorCS"),sQuery(id+"F1.wireOp",EDGE,"E102.MirrorCS"),subQ1,sQuery(id+"F1.wireOp",EDGE,"E104.MirrorCS"),sQuery(id+"F1.wireOp",EDGE,"E105.MirrorCS"),sQuery(id+"F1.wireOp",EDGE,"E106.MirrorCS"),sQuery(id+"F1.wireOp",EDGE,"E107.MirrorCS"),sQuery(id+"F1.wireOp",EDGE,"E108.MirrorCS"),subQ0,sQuery(id+"F1.wireOp",EDGE,"E110.MirrorCS"),sQuery(id+"F1.wireOp",EDGE,"E111.MirrorCS"),sQuery(id+"F1.wireOp",EDGE,"E112.MirrorCS"),sQuery(id+"F1.wireOp",EDGE,"E113.MirrorCS"),sQuery(id+"F1.wireOp",EDGE,"E128.MirrorCS"),subQ2,sQuery(id+"F1.wireOp",EDGE,"E130.MirrorCS"),sQuery(id+"F1.wireOp",EDGE,"E131.MirrorCS"),sQuery(id+"F1.wireOp",EDGE,"E132.MirrorCS"),sQuery(id+"F1.wireOp",EDGE,"E133.MirrorCS"),sQuery(id+"F1.wireOp",EDGE,"E134.MirrorCS"),sQuery(id+"F1.wireOp",EDGE,"E135.MirrorCS"),sQuery(id+"F1.wireOp",EDGE,"E136.MirrorCS"),sQuery(id+"F1.wireOp",EDGE,"E137.MirrorCS"),sQuery(id+"F1.wireOp",EDGE,"E138.MirrorCS"),sQuery(id+"F1.wireOp",EDGE,"E139.MirrorCS"),sQuery(id+"F1.wireOp",EDGE,"E140.MirrorCS"),sQuery(id+"F1.wireOp",EDGE,"E141.MirrorCS"),sQuery(id+"F1.wireOp",EDGE,"E142.MirrorCS"),sQuery(id+"F1.wireOp",EDGE,"E143.MirrorCS"),sQuery(id+"F1.wireOp",EDGE,"E144.MirrorCS"),sQuery(id+"F1.wireOp",EDGE,"E145.MirrorCS"),sQuery(id+"F1.wireOp",EDGE,"E146.MirrorCS"),sQuery(id+"F1.wireOp",EDGE,"E147.MirrorCS"),sQuery(id+"F1.wireOp",EDGE,"E148.MirrorCS"),subQ3,sQuery(id+"F1.wireOp",EDGE,"E150.MirrorCS"),sQuery(id+"F1.wireOp",EDGE,"E151.MirrorCS"),sQuery(id+"F1.wireOp",EDGE,"E152.MirrorCS"),sQuery(id+"F1.wireOp",EDGE,"E153.MirrorCS"),sQuery(id+"F1.wireOp",EDGE,"E154.MirrorCS"),sQuery(id+"F1.wireOp",EDGE,"E156.MirrorCS")])],"isStart":true}),makeQuery(id+"F2.opExtrude","SWEPT_FACE",FACE,{"disambiguationData":[OSD([subQ1])]}),makeQuery(id+"F2.opExtrude","SWEPT_FACE",FACE,{"disambiguationData":[OSD([subQ0])]}),makeQuery(id+"F2.opExtrude","SWEPT_FACE",FACE,{"disambiguationData":[OSD([subQ2])]}),makeQuery(id+"F2.opExtrude","SWEPT_FACE",FACE,{"disambiguationData":[OSD([subQ3])]}),makeQuery(id+"F3.opExtrude","SWEPT_FACE",FACE,{"disambiguationData":[OSD([subQ4])]})])],"derivedFrom":makeQuery(id+"F3.opExtrude","CAP_EDGE",EDGE,{"disambiguationData":[OSD([subQ4])],"isStart":true})});}
            var Q7;
            {var subQ0=sQuery(id+"F1.wireOp",EDGE,"E135.MirrorCS");var subQ1=sQuery(id+"F0.wireOp",EDGE,"E0");var subQ2=sQuery(id+"F1.wireOp",EDGE,"E144.MirrorCS");var subQ3=sQuery(id+"F1.wireOp",EDGE,"E129.MirrorCS");var subQ4=sQuery(id+"F1.wireOp",EDGE,"E149.MirrorCS");Q7=makeQuery(id+"F3.boolean.opBoolean","SPLIT",EDGE,{"disambiguationData":[TD([makeQuery(id+"F2.opExtrude","CAP_FACE",FACE,{"disambiguationData":[OSD([sQuery(id+"F1.wireOp",EDGE,"E86"),sQuery(id+"F1.wireOp",EDGE,"E87"),sQuery(id+"F1.wireOp",EDGE,"E88"),sQuery(id+"F1.wireOp",EDGE,"E89"),sQuery(id+"F1.wireOp",EDGE,"E90"),sQuery(id+"F1.wireOp",EDGE,"E91"),sQuery(id+"F1.wireOp",EDGE,"E92"),sQuery(id+"F1.wireOp",EDGE,"E93"),sQuery(id+"F1.wireOp",EDGE,"E94"),sQuery(id+"F1.wireOp",EDGE,"E95"),sQuery(id+"F1.wireOp",EDGE,"E96"),sQuery(id+"F1.wireOp",EDGE,"E97"),sQuery(id+"F1.wireOp",EDGE,"E98"),sQuery(id+"F1.wireOp",EDGE,"E99"),sQuery(id+"F1.wireOp",EDGE,"E100.MirrorCS"),sQuery(id+"F1.wireOp",EDGE,"E101.MirrorCS"),sQuery(id+"F1.wireOp",EDGE,"E102.MirrorCS"),sQuery(id+"F1.wireOp",EDGE,"E103.MirrorCS"),sQuery(id+"F1.wireOp",EDGE,"E104.MirrorCS"),sQuery(id+"F1.wireOp",EDGE,"E105.MirrorCS"),sQuery(id+"F1.wireOp",EDGE,"E106.MirrorCS"),sQuery(id+"F1.wireOp",EDGE,"E107.MirrorCS"),sQuery(id+"F1.wireOp",EDGE,"E108.MirrorCS"),sQuery(id+"F1.wireOp",EDGE,"E109.MirrorCS"),sQuery(id+"F1.wireOp",EDGE,"E110.MirrorCS"),sQuery(id+"F1.wireOp",EDGE,"E111.MirrorCS"),sQuery(id+"F1.wireOp",EDGE,"E112.MirrorCS"),sQuery(id+"F1.wireOp",EDGE,"E113.MirrorCS"),sQuery(id+"F1.wireOp",EDGE,"E128.MirrorCS"),subQ3,sQuery(id+"F1.wireOp",EDGE,"E130.MirrorCS"),sQuery(id+"F1.wireOp",EDGE,"E131.MirrorCS"),sQuery(id+"F1.wireOp",EDGE,"E132.MirrorCS"),sQuery(id+"F1.wireOp",EDGE,"E133.MirrorCS"),sQuery(id+"F1.wireOp",EDGE,"E134.MirrorCS"),subQ0,sQuery(id+"F1.wireOp",EDGE,"E136.MirrorCS"),sQuery(id+"F1.wireOp",EDGE,"E137.MirrorCS"),sQuery(id+"F1.wireOp",EDGE,"E138.MirrorCS"),sQuery(id+"F1.wireOp",EDGE,"E139.MirrorCS"),sQuery(id+"F1.wireOp",EDGE,"E140.MirrorCS"),sQuery(id+"F1.wireOp",EDGE,"E141.MirrorCS"),sQuery(id+"F1.wireOp",EDGE,"E142.MirrorCS"),sQuery(id+"F1.wireOp",EDGE,"E143.MirrorCS"),subQ2,sQuery(id+"F1.wireOp",EDGE,"E145.MirrorCS"),sQuery(id+"F1.wireOp",EDGE,"E146.MirrorCS"),sQuery(id+"F1.wireOp",EDGE,"E147.MirrorCS"),sQuery(id+"F1.wireOp",EDGE,"E148.MirrorCS"),subQ4,sQuery(id+"F1.wireOp",EDGE,"E150.MirrorCS"),sQuery(id+"F1.wireOp",EDGE,"E151.MirrorCS"),sQuery(id+"F1.wireOp",EDGE,"E152.MirrorCS"),sQuery(id+"F1.wireOp",EDGE,"E153.MirrorCS"),sQuery(id+"F1.wireOp",EDGE,"E154.MirrorCS"),sQuery(id+"F1.wireOp",EDGE,"E156.MirrorCS")])],"isStart":true}),makeQuery(id+"F2.opExtrude","SWEPT_FACE",FACE,{"disambiguationData":[OSD([subQ3])]}),makeQuery(id+"F2.opExtrude","SWEPT_FACE",FACE,{"disambiguationData":[OSD([subQ0])]}),makeQuery(id+"F2.opExtrude","SWEPT_FACE",FACE,{"disambiguationData":[OSD([subQ2])]}),makeQuery(id+"F2.opExtrude","SWEPT_FACE",FACE,{"disambiguationData":[OSD([subQ4])]}),makeQuery(id+"F3.opExtrude","SWEPT_FACE",FACE,{"disambiguationData":[OSD([subQ1])]})])],"derivedFrom":makeQuery(id+"F3.opExtrude","CAP_EDGE",EDGE,{"disambiguationData":[OSD([subQ1])],"isStart":true})});}
            var Q8;
            {var subQ0=sQuery(id+"F1.wireOp",EDGE,"E137.MirrorCS");var subQ1=sQuery(id+"F1.wireOp",EDGE,"E135.MirrorCS");var subQ2=sQuery(id+"F0.wireOp",EDGE,"E0");var subQ3=sQuery(id+"F1.wireOp",EDGE,"E144.MirrorCS");var subQ4=sQuery(id+"F1.wireOp",EDGE,"E145.MirrorCS");Q8=makeQuery(id+"F3.boolean.opBoolean","SPLIT",EDGE,{"disambiguationData":[TD([makeQuery(id+"F2.opExtrude","CAP_FACE",FACE,{"disambiguationData":[OSD([sQuery(id+"F1.wireOp",EDGE,"E86"),sQuery(id+"F1.wireOp",EDGE,"E87"),sQuery(id+"F1.wireOp",EDGE,"E88"),sQuery(id+"F1.wireOp",EDGE,"E89"),sQuery(id+"F1.wireOp",EDGE,"E90"),sQuery(id+"F1.wireOp",EDGE,"E91"),sQuery(id+"F1.wireOp",EDGE,"E92"),sQuery(id+"F1.wireOp",EDGE,"E93"),sQuery(id+"F1.wireOp",EDGE,"E94"),sQuery(id+"F1.wireOp",EDGE,"E95"),sQuery(id+"F1.wireOp",EDGE,"E96"),sQuery(id+"F1.wireOp",EDGE,"E97"),sQuery(id+"F1.wireOp",EDGE,"E98"),sQuery(id+"F1.wireOp",EDGE,"E99"),sQuery(id+"F1.wireOp",EDGE,"E100.MirrorCS"),sQuery(id+"F1.wireOp",EDGE,"E101.MirrorCS"),sQuery(id+"F1.wireOp",EDGE,"E102.MirrorCS"),sQuery(id+"F1.wireOp",EDGE,"E103.MirrorCS"),sQuery(id+"F1.wireOp",EDGE,"E104.MirrorCS"),sQuery(id+"F1.wireOp",EDGE,"E105.MirrorCS"),sQuery(id+"F1.wireOp",EDGE,"E106.MirrorCS"),sQuery(id+"F1.wireOp",EDGE,"E107.MirrorCS"),sQuery(id+"F1.wireOp",EDGE,"E108.MirrorCS"),sQuery(id+"F1.wireOp",EDGE,"E109.MirrorCS"),sQuery(id+"F1.wireOp",EDGE,"E110.MirrorCS"),sQuery(id+"F1.wireOp",EDGE,"E111.MirrorCS"),sQuery(id+"F1.wireOp",EDGE,"E112.MirrorCS"),sQuery(id+"F1.wireOp",EDGE,"E113.MirrorCS"),sQuery(id+"F1.wireOp",EDGE,"E128.MirrorCS"),sQuery(id+"F1.wireOp",EDGE,"E129.MirrorCS"),sQuery(id+"F1.wireOp",EDGE,"E130.MirrorCS"),sQuery(id+"F1.wireOp",EDGE,"E131.MirrorCS"),sQuery(id+"F1.wireOp",EDGE,"E132.MirrorCS"),sQuery(id+"F1.wireOp",EDGE,"E133.MirrorCS"),sQuery(id+"F1.wireOp",EDGE,"E134.MirrorCS"),subQ1,sQuery(id+"F1.wireOp",EDGE,"E136.MirrorCS"),subQ0,sQuery(id+"F1.wireOp",EDGE,"E138.MirrorCS"),sQuery(id+"F1.wireOp",EDGE,"E139.MirrorCS"),sQuery(id+"F1.wireOp",EDGE,"E140.MirrorCS"),sQuery(id+"F1.wireOp",EDGE,"E141.MirrorCS"),sQuery(id+"F1.wireOp",EDGE,"E142.MirrorCS"),sQuery(id+"F1.wireOp",EDGE,"E143.MirrorCS"),subQ3,subQ4,sQuery(id+"F1.wireOp",EDGE,"E146.MirrorCS"),sQuery(id+"F1.wireOp",EDGE,"E147.MirrorCS"),sQuery(id+"F1.wireOp",EDGE,"E148.MirrorCS"),sQuery(id+"F1.wireOp",EDGE,"E149.MirrorCS"),sQuery(id+"F1.wireOp",EDGE,"E150.MirrorCS"),sQuery(id+"F1.wireOp",EDGE,"E151.MirrorCS"),sQuery(id+"F1.wireOp",EDGE,"E152.MirrorCS"),sQuery(id+"F1.wireOp",EDGE,"E153.MirrorCS"),sQuery(id+"F1.wireOp",EDGE,"E154.MirrorCS"),sQuery(id+"F1.wireOp",EDGE,"E156.MirrorCS")])],"isStart":true}),makeQuery(id+"F2.opExtrude","SWEPT_FACE",FACE,{"disambiguationData":[OSD([subQ1])]}),makeQuery(id+"F2.opExtrude","SWEPT_FACE",FACE,{"disambiguationData":[OSD([subQ0])]}),makeQuery(id+"F2.opExtrude","SWEPT_FACE",FACE,{"disambiguationData":[OSD([subQ3])]}),makeQuery(id+"F2.opExtrude","SWEPT_FACE",FACE,{"disambiguationData":[OSD([subQ4])]}),makeQuery(id+"F3.opExtrude","SWEPT_FACE",FACE,{"disambiguationData":[OSD([subQ2])]})])],"derivedFrom":makeQuery(id+"F3.opExtrude","CAP_EDGE",EDGE,{"disambiguationData":[OSD([subQ2])],"isStart":true})});}
            var Q9;
            {var subQ0=sQuery(id+"F1.wireOp",EDGE,"E145.MirrorCS");var subQ1=sQuery(id+"F1.wireOp",EDGE,"E143.MirrorCS");var subQ2=sQuery(id+"F1.wireOp",EDGE,"E154.MirrorCS");var subQ3=sQuery(id+"F1.wireOp",EDGE,"E137.MirrorCS");var subQ4=sQuery(id+"F0.wireOp",EDGE,"E0");Q9=makeQuery(id+"F3.boolean.opBoolean","SPLIT",EDGE,{"disambiguationData":[TD([makeQuery(id+"F2.opExtrude","CAP_FACE",FACE,{"disambiguationData":[OSD([sQuery(id+"F1.wireOp",EDGE,"E86"),sQuery(id+"F1.wireOp",EDGE,"E87"),sQuery(id+"F1.wireOp",EDGE,"E88"),sQuery(id+"F1.wireOp",EDGE,"E89"),sQuery(id+"F1.wireOp",EDGE,"E90"),sQuery(id+"F1.wireOp",EDGE,"E91"),sQuery(id+"F1.wireOp",EDGE,"E92"),sQuery(id+"F1.wireOp",EDGE,"E93"),sQuery(id+"F1.wireOp",EDGE,"E94"),sQuery(id+"F1.wireOp",EDGE,"E95"),sQuery(id+"F1.wireOp",EDGE,"E96"),sQuery(id+"F1.wireOp",EDGE,"E97"),sQuery(id+"F1.wireOp",EDGE,"E98"),sQuery(id+"F1.wireOp",EDGE,"E99"),sQuery(id+"F1.wireOp",EDGE,"E100.MirrorCS"),sQuery(id+"F1.wireOp",EDGE,"E101.MirrorCS"),sQuery(id+"F1.wireOp",EDGE,"E102.MirrorCS"),sQuery(id+"F1.wireOp",EDGE,"E103.MirrorCS"),sQuery(id+"F1.wireOp",EDGE,"E104.MirrorCS"),sQuery(id+"F1.wireOp",EDGE,"E105.MirrorCS"),sQuery(id+"F1.wireOp",EDGE,"E106.MirrorCS"),sQuery(id+"F1.wireOp",EDGE,"E107.MirrorCS"),sQuery(id+"F1.wireOp",EDGE,"E108.MirrorCS"),sQuery(id+"F1.wireOp",EDGE,"E109.MirrorCS"),sQuery(id+"F1.wireOp",EDGE,"E110.MirrorCS"),sQuery(id+"F1.wireOp",EDGE,"E111.MirrorCS"),sQuery(id+"F1.wireOp",EDGE,"E112.MirrorCS"),sQuery(id+"F1.wireOp",EDGE,"E113.MirrorCS"),sQuery(id+"F1.wireOp",EDGE,"E128.MirrorCS"),sQuery(id+"F1.wireOp",EDGE,"E129.MirrorCS"),sQuery(id+"F1.wireOp",EDGE,"E130.MirrorCS"),sQuery(id+"F1.wireOp",EDGE,"E131.MirrorCS"),sQuery(id+"F1.wireOp",EDGE,"E132.MirrorCS"),sQuery(id+"F1.wireOp",EDGE,"E133.MirrorCS"),sQuery(id+"F1.wireOp",EDGE,"E134.MirrorCS"),sQuery(id+"F1.wireOp",EDGE,"E135.MirrorCS"),sQuery(id+"F1.wireOp",EDGE,"E136.MirrorCS"),subQ3,sQuery(id+"F1.wireOp",EDGE,"E138.MirrorCS"),sQuery(id+"F1.wireOp",EDGE,"E139.MirrorCS"),sQuery(id+"F1.wireOp",EDGE,"E140.MirrorCS"),sQuery(id+"F1.wireOp",EDGE,"E141.MirrorCS"),sQuery(id+"F1.wireOp",EDGE,"E142.MirrorCS"),subQ1,sQuery(id+"F1.wireOp",EDGE,"E144.MirrorCS"),subQ0,sQuery(id+"F1.wireOp",EDGE,"E146.MirrorCS"),sQuery(id+"F1.wireOp",EDGE,"E147.MirrorCS"),sQuery(id+"F1.wireOp",EDGE,"E148.MirrorCS"),sQuery(id+"F1.wireOp",EDGE,"E149.MirrorCS"),sQuery(id+"F1.wireOp",EDGE,"E150.MirrorCS"),sQuery(id+"F1.wireOp",EDGE,"E151.MirrorCS"),sQuery(id+"F1.wireOp",EDGE,"E152.MirrorCS"),sQuery(id+"F1.wireOp",EDGE,"E153.MirrorCS"),subQ2,sQuery(id+"F1.wireOp",EDGE,"E156.MirrorCS")])],"isStart":true}),makeQuery(id+"F2.opExtrude","SWEPT_FACE",FACE,{"disambiguationData":[OSD([subQ3])]}),makeQuery(id+"F2.opExtrude","SWEPT_FACE",FACE,{"disambiguationData":[OSD([subQ1])]}),makeQuery(id+"F2.opExtrude","SWEPT_FACE",FACE,{"disambiguationData":[OSD([subQ0])]}),makeQuery(id+"F2.opExtrude","SWEPT_FACE",FACE,{"disambiguationData":[OSD([subQ2])]}),makeQuery(id+"F3.opExtrude","SWEPT_FACE",FACE,{"disambiguationData":[OSD([subQ4])]})])],"derivedFrom":makeQuery(id+"F3.opExtrude","CAP_EDGE",EDGE,{"disambiguationData":[OSD([subQ4])],"isStart":true})});}
            var Q10;
            {var subQ0=sQuery(id+"F1.wireOp",EDGE,"E87");var subQ1=sQuery(id+"F1.wireOp",EDGE,"E100.MirrorCS");var subQ2=sQuery(id+"F1.wireOp",EDGE,"E108.MirrorCS");var subQ3=sQuery(id+"F1.wireOp",EDGE,"E86");var subQ4=sQuery(id+"F0.wireOp",EDGE,"E0");Q10=makeQuery(id+"F3.boolean.opBoolean","SPLIT",EDGE,{"disambiguationData":[TD([makeQuery(id+"F2.opExtrude","SWEPT_FACE",FACE,{"disambiguationData":[OSD([subQ3])]}),makeQuery(id+"F2.opExtrude","CAP_FACE",FACE,{"disambiguationData":[OSD([subQ3,subQ0,sQuery(id+"F1.wireOp",EDGE,"E88"),sQuery(id+"F1.wireOp",EDGE,"E89"),sQuery(id+"F1.wireOp",EDGE,"E90"),sQuery(id+"F1.wireOp",EDGE,"E91"),sQuery(id+"F1.wireOp",EDGE,"E92"),sQuery(id+"F1.wireOp",EDGE,"E93"),sQuery(id+"F1.wireOp",EDGE,"E94"),sQuery(id+"F1.wireOp",EDGE,"E95"),sQuery(id+"F1.wireOp",EDGE,"E96"),sQuery(id+"F1.wireOp",EDGE,"E97"),sQuery(id+"F1.wireOp",EDGE,"E98"),sQuery(id+"F1.wireOp",EDGE,"E99"),subQ1,sQuery(id+"F1.wireOp",EDGE,"E101.MirrorCS"),sQuery(id+"F1.wireOp",EDGE,"E102.MirrorCS"),sQuery(id+"F1.wireOp",EDGE,"E103.MirrorCS"),sQuery(id+"F1.wireOp",EDGE,"E104.MirrorCS"),sQuery(id+"F1.wireOp",EDGE,"E105.MirrorCS"),sQuery(id+"F1.wireOp",EDGE,"E106.MirrorCS"),sQuery(id+"F1.wireOp",EDGE,"E107.MirrorCS"),subQ2,sQuery(id+"F1.wireOp",EDGE,"E109.MirrorCS"),sQuery(id+"F1.wireOp",EDGE,"E110.MirrorCS"),sQuery(id+"F1.wireOp",EDGE,"E111.MirrorCS"),sQuery(id+"F1.wireOp",EDGE,"E112.MirrorCS"),sQuery(id+"F1.wireOp",EDGE,"E113.MirrorCS"),sQuery(id+"F1.wireOp",EDGE,"E128.MirrorCS"),sQuery(id+"F1.wireOp",EDGE,"E129.MirrorCS"),sQuery(id+"F1.wireOp",EDGE,"E130.MirrorCS"),sQuery(id+"F1.wireOp",EDGE,"E131.MirrorCS"),sQuery(id+"F1.wireOp",EDGE,"E132.MirrorCS"),sQuery(id+"F1.wireOp",EDGE,"E133.MirrorCS"),sQuery(id+"F1.wireOp",EDGE,"E134.MirrorCS"),sQuery(id+"F1.wireOp",EDGE,"E135.MirrorCS"),sQuery(id+"F1.wireOp",EDGE,"E136.MirrorCS"),sQuery(id+"F1.wireOp",EDGE,"E137.MirrorCS"),sQuery(id+"F1.wireOp",EDGE,"E138.MirrorCS"),sQuery(id+"F1.wireOp",EDGE,"E139.MirrorCS"),sQuery(id+"F1.wireOp",EDGE,"E140.MirrorCS"),sQuery(id+"F1.wireOp",EDGE,"E141.MirrorCS"),sQuery(id+"F1.wireOp",EDGE,"E142.MirrorCS"),sQuery(id+"F1.wireOp",EDGE,"E143.MirrorCS"),sQuery(id+"F1.wireOp",EDGE,"E144.MirrorCS"),sQuery(id+"F1.wireOp",EDGE,"E145.MirrorCS"),sQuery(id+"F1.wireOp",EDGE,"E146.MirrorCS"),sQuery(id+"F1.wireOp",EDGE,"E147.MirrorCS"),sQuery(id+"F1.wireOp",EDGE,"E148.MirrorCS"),sQuery(id+"F1.wireOp",EDGE,"E149.MirrorCS"),sQuery(id+"F1.wireOp",EDGE,"E150.MirrorCS"),sQuery(id+"F1.wireOp",EDGE,"E151.MirrorCS"),sQuery(id+"F1.wireOp",EDGE,"E152.MirrorCS"),sQuery(id+"F1.wireOp",EDGE,"E153.MirrorCS"),sQuery(id+"F1.wireOp",EDGE,"E154.MirrorCS"),sQuery(id+"F1.wireOp",EDGE,"E156.MirrorCS")])],"isStart":true}),makeQuery(id+"F2.opExtrude","SWEPT_FACE",FACE,{"disambiguationData":[OSD([subQ0])]}),makeQuery(id+"F2.opExtrude","SWEPT_FACE",FACE,{"disambiguationData":[OSD([subQ1])]}),makeQuery(id+"F2.opExtrude","SWEPT_FACE",FACE,{"disambiguationData":[OSD([subQ2])]}),makeQuery(id+"F3.opExtrude","SWEPT_FACE",FACE,{"disambiguationData":[OSD([subQ4])]})])],"derivedFrom":makeQuery(id+"F3.opExtrude","CAP_EDGE",EDGE,{"disambiguationData":[OSD([subQ4])],"isStart":true})});}
            var Q11;
            {var subQ0=sQuery(id+"F1.wireOp",EDGE,"E88");var subQ1=sQuery(id+"F0.wireOp",EDGE,"E0");var subQ2=sQuery(id+"F1.wireOp",EDGE,"E87");var subQ3=sQuery(id+"F1.wireOp",EDGE,"E89");var subQ4=sQuery(id+"F1.wireOp",EDGE,"E86");Q11=makeQuery(id+"F3.boolean.opBoolean","SPLIT",EDGE,{"disambiguationData":[TD([makeQuery(id+"F2.opExtrude","SWEPT_FACE",FACE,{"disambiguationData":[OSD([subQ4])]}),makeQuery(id+"F2.opExtrude","CAP_FACE",FACE,{"disambiguationData":[OSD([subQ4,subQ2,subQ0,subQ3,sQuery(id+"F1.wireOp",EDGE,"E90"),sQuery(id+"F1.wireOp",EDGE,"E91"),sQuery(id+"F1.wireOp",EDGE,"E92"),sQuery(id+"F1.wireOp",EDGE,"E93"),sQuery(id+"F1.wireOp",EDGE,"E94"),sQuery(id+"F1.wireOp",EDGE,"E95"),sQuery(id+"F1.wireOp",EDGE,"E96"),sQuery(id+"F1.wireOp",EDGE,"E97"),sQuery(id+"F1.wireOp",EDGE,"E98"),sQuery(id+"F1.wireOp",EDGE,"E99"),sQuery(id+"F1.wireOp",EDGE,"E100.MirrorCS"),sQuery(id+"F1.wireOp",EDGE,"E101.MirrorCS"),sQuery(id+"F1.wireOp",EDGE,"E102.MirrorCS"),sQuery(id+"F1.wireOp",EDGE,"E103.MirrorCS"),sQuery(id+"F1.wireOp",EDGE,"E104.MirrorCS"),sQuery(id+"F1.wireOp",EDGE,"E105.MirrorCS"),sQuery(id+"F1.wireOp",EDGE,"E106.MirrorCS"),sQuery(id+"F1.wireOp",EDGE,"E107.MirrorCS"),sQuery(id+"F1.wireOp",EDGE,"E108.MirrorCS"),sQuery(id+"F1.wireOp",EDGE,"E109.MirrorCS"),sQuery(id+"F1.wireOp",EDGE,"E110.MirrorCS"),sQuery(id+"F1.wireOp",EDGE,"E111.MirrorCS"),sQuery(id+"F1.wireOp",EDGE,"E112.MirrorCS"),sQuery(id+"F1.wireOp",EDGE,"E113.MirrorCS"),sQuery(id+"F1.wireOp",EDGE,"E128.MirrorCS"),sQuery(id+"F1.wireOp",EDGE,"E129.MirrorCS"),sQuery(id+"F1.wireOp",EDGE,"E130.MirrorCS"),sQuery(id+"F1.wireOp",EDGE,"E131.MirrorCS"),sQuery(id+"F1.wireOp",EDGE,"E132.MirrorCS"),sQuery(id+"F1.wireOp",EDGE,"E133.MirrorCS"),sQuery(id+"F1.wireOp",EDGE,"E134.MirrorCS"),sQuery(id+"F1.wireOp",EDGE,"E135.MirrorCS"),sQuery(id+"F1.wireOp",EDGE,"E136.MirrorCS"),sQuery(id+"F1.wireOp",EDGE,"E137.MirrorCS"),sQuery(id+"F1.wireOp",EDGE,"E138.MirrorCS"),sQuery(id+"F1.wireOp",EDGE,"E139.MirrorCS"),sQuery(id+"F1.wireOp",EDGE,"E140.MirrorCS"),sQuery(id+"F1.wireOp",EDGE,"E141.MirrorCS"),sQuery(id+"F1.wireOp",EDGE,"E142.MirrorCS"),sQuery(id+"F1.wireOp",EDGE,"E143.MirrorCS"),sQuery(id+"F1.wireOp",EDGE,"E144.MirrorCS"),sQuery(id+"F1.wireOp",EDGE,"E145.MirrorCS"),sQuery(id+"F1.wireOp",EDGE,"E146.MirrorCS"),sQuery(id+"F1.wireOp",EDGE,"E147.MirrorCS"),sQuery(id+"F1.wireOp",EDGE,"E148.MirrorCS"),sQuery(id+"F1.wireOp",EDGE,"E149.MirrorCS"),sQuery(id+"F1.wireOp",EDGE,"E150.MirrorCS"),sQuery(id+"F1.wireOp",EDGE,"E151.MirrorCS"),sQuery(id+"F1.wireOp",EDGE,"E152.MirrorCS"),sQuery(id+"F1.wireOp",EDGE,"E153.MirrorCS"),sQuery(id+"F1.wireOp",EDGE,"E154.MirrorCS"),sQuery(id+"F1.wireOp",EDGE,"E156.MirrorCS")])],"isStart":true}),makeQuery(id+"F2.opExtrude","SWEPT_FACE",FACE,{"disambiguationData":[OSD([subQ2])]}),makeQuery(id+"F2.opExtrude","SWEPT_FACE",FACE,{"disambiguationData":[OSD([subQ0])]}),makeQuery(id+"F2.opExtrude","SWEPT_FACE",FACE,{"disambiguationData":[OSD([subQ3])]}),makeQuery(id+"F3.opExtrude","SWEPT_FACE",FACE,{"disambiguationData":[OSD([subQ1])]})])],"derivedFrom":makeQuery(id+"F3.opExtrude","CAP_EDGE",EDGE,{"disambiguationData":[OSD([subQ1])],"isStart":true})});}
            var Q12;
            {var subQ0=sQuery(id+"F1.wireOp",EDGE,"E89");var subQ1=sQuery(id+"F1.wireOp",EDGE,"E88");var subQ2=sQuery(id+"F0.wireOp",EDGE,"E0");var subQ3=sQuery(id+"F1.wireOp",EDGE,"E90");var subQ4=sQuery(id+"F1.wireOp",EDGE,"E91");Q12=makeQuery(id+"F3.boolean.opBoolean","SPLIT",EDGE,{"disambiguationData":[TD([makeQuery(id+"F2.opExtrude","CAP_FACE",FACE,{"disambiguationData":[OSD([sQuery(id+"F1.wireOp",EDGE,"E86"),sQuery(id+"F1.wireOp",EDGE,"E87"),subQ1,subQ0,subQ3,subQ4,sQuery(id+"F1.wireOp",EDGE,"E92"),sQuery(id+"F1.wireOp",EDGE,"E93"),sQuery(id+"F1.wireOp",EDGE,"E94"),sQuery(id+"F1.wireOp",EDGE,"E95"),sQuery(id+"F1.wireOp",EDGE,"E96"),sQuery(id+"F1.wireOp",EDGE,"E97"),sQuery(id+"F1.wireOp",EDGE,"E98"),sQuery(id+"F1.wireOp",EDGE,"E99"),sQuery(id+"F1.wireOp",EDGE,"E100.MirrorCS"),sQuery(id+"F1.wireOp",EDGE,"E101.MirrorCS"),sQuery(id+"F1.wireOp",EDGE,"E102.MirrorCS"),sQuery(id+"F1.wireOp",EDGE,"E103.MirrorCS"),sQuery(id+"F1.wireOp",EDGE,"E104.MirrorCS"),sQuery(id+"F1.wireOp",EDGE,"E105.MirrorCS"),sQuery(id+"F1.wireOp",EDGE,"E106.MirrorCS"),sQuery(id+"F1.wireOp",EDGE,"E107.MirrorCS"),sQuery(id+"F1.wireOp",EDGE,"E108.MirrorCS"),sQuery(id+"F1.wireOp",EDGE,"E109.MirrorCS"),sQuery(id+"F1.wireOp",EDGE,"E110.MirrorCS"),sQuery(id+"F1.wireOp",EDGE,"E111.MirrorCS"),sQuery(id+"F1.wireOp",EDGE,"E112.MirrorCS"),sQuery(id+"F1.wireOp",EDGE,"E113.MirrorCS"),sQuery(id+"F1.wireOp",EDGE,"E128.MirrorCS"),sQuery(id+"F1.wireOp",EDGE,"E129.MirrorCS"),sQuery(id+"F1.wireOp",EDGE,"E130.MirrorCS"),sQuery(id+"F1.wireOp",EDGE,"E131.MirrorCS"),sQuery(id+"F1.wireOp",EDGE,"E132.MirrorCS"),sQuery(id+"F1.wireOp",EDGE,"E133.MirrorCS"),sQuery(id+"F1.wireOp",EDGE,"E134.MirrorCS"),sQuery(id+"F1.wireOp",EDGE,"E135.MirrorCS"),sQuery(id+"F1.wireOp",EDGE,"E136.MirrorCS"),sQuery(id+"F1.wireOp",EDGE,"E137.MirrorCS"),sQuery(id+"F1.wireOp",EDGE,"E138.MirrorCS"),sQuery(id+"F1.wireOp",EDGE,"E139.MirrorCS"),sQuery(id+"F1.wireOp",EDGE,"E140.MirrorCS"),sQuery(id+"F1.wireOp",EDGE,"E141.MirrorCS"),sQuery(id+"F1.wireOp",EDGE,"E142.MirrorCS"),sQuery(id+"F1.wireOp",EDGE,"E143.MirrorCS"),sQuery(id+"F1.wireOp",EDGE,"E144.MirrorCS"),sQuery(id+"F1.wireOp",EDGE,"E145.MirrorCS"),sQuery(id+"F1.wireOp",EDGE,"E146.MirrorCS"),sQuery(id+"F1.wireOp",EDGE,"E147.MirrorCS"),sQuery(id+"F1.wireOp",EDGE,"E148.MirrorCS"),sQuery(id+"F1.wireOp",EDGE,"E149.MirrorCS"),sQuery(id+"F1.wireOp",EDGE,"E150.MirrorCS"),sQuery(id+"F1.wireOp",EDGE,"E151.MirrorCS"),sQuery(id+"F1.wireOp",EDGE,"E152.MirrorCS"),sQuery(id+"F1.wireOp",EDGE,"E153.MirrorCS"),sQuery(id+"F1.wireOp",EDGE,"E154.MirrorCS"),sQuery(id+"F1.wireOp",EDGE,"E156.MirrorCS")])],"isStart":true}),makeQuery(id+"F2.opExtrude","SWEPT_FACE",FACE,{"disambiguationData":[OSD([subQ1])]}),makeQuery(id+"F2.opExtrude","SWEPT_FACE",FACE,{"disambiguationData":[OSD([subQ0])]}),makeQuery(id+"F2.opExtrude","SWEPT_FACE",FACE,{"disambiguationData":[OSD([subQ3])]}),makeQuery(id+"F2.opExtrude","SWEPT_FACE",FACE,{"disambiguationData":[OSD([subQ4])]}),makeQuery(id+"F3.opExtrude","SWEPT_FACE",FACE,{"disambiguationData":[OSD([subQ2])]})])],"derivedFrom":makeQuery(id+"F3.opExtrude","CAP_EDGE",EDGE,{"disambiguationData":[OSD([subQ2])],"isStart":true})});}
            var Q13;
            {var subQ0=sQuery(id+"F1.wireOp",EDGE,"E92");var subQ1=sQuery(id+"F1.wireOp",EDGE,"E91");var subQ2=sQuery(id+"F1.wireOp",EDGE,"E90");var subQ3=sQuery(id+"F1.wireOp",EDGE,"E93");var subQ4=sQuery(id+"F0.wireOp",EDGE,"E0");Q13=makeQuery(id+"F3.boolean.opBoolean","SPLIT",EDGE,{"disambiguationData":[TD([makeQuery(id+"F2.opExtrude","CAP_FACE",FACE,{"disambiguationData":[OSD([sQuery(id+"F1.wireOp",EDGE,"E86"),sQuery(id+"F1.wireOp",EDGE,"E87"),sQuery(id+"F1.wireOp",EDGE,"E88"),sQuery(id+"F1.wireOp",EDGE,"E89"),subQ2,subQ1,subQ0,subQ3,sQuery(id+"F1.wireOp",EDGE,"E94"),sQuery(id+"F1.wireOp",EDGE,"E95"),sQuery(id+"F1.wireOp",EDGE,"E96"),sQuery(id+"F1.wireOp",EDGE,"E97"),sQuery(id+"F1.wireOp",EDGE,"E98"),sQuery(id+"F1.wireOp",EDGE,"E99"),sQuery(id+"F1.wireOp",EDGE,"E100.MirrorCS"),sQuery(id+"F1.wireOp",EDGE,"E101.MirrorCS"),sQuery(id+"F1.wireOp",EDGE,"E102.MirrorCS"),sQuery(id+"F1.wireOp",EDGE,"E103.MirrorCS"),sQuery(id+"F1.wireOp",EDGE,"E104.MirrorCS"),sQuery(id+"F1.wireOp",EDGE,"E105.MirrorCS"),sQuery(id+"F1.wireOp",EDGE,"E106.MirrorCS"),sQuery(id+"F1.wireOp",EDGE,"E107.MirrorCS"),sQuery(id+"F1.wireOp",EDGE,"E108.MirrorCS"),sQuery(id+"F1.wireOp",EDGE,"E109.MirrorCS"),sQuery(id+"F1.wireOp",EDGE,"E110.MirrorCS"),sQuery(id+"F1.wireOp",EDGE,"E111.MirrorCS"),sQuery(id+"F1.wireOp",EDGE,"E112.MirrorCS"),sQuery(id+"F1.wireOp",EDGE,"E113.MirrorCS"),sQuery(id+"F1.wireOp",EDGE,"E128.MirrorCS"),sQuery(id+"F1.wireOp",EDGE,"E129.MirrorCS"),sQuery(id+"F1.wireOp",EDGE,"E130.MirrorCS"),sQuery(id+"F1.wireOp",EDGE,"E131.MirrorCS"),sQuery(id+"F1.wireOp",EDGE,"E132.MirrorCS"),sQuery(id+"F1.wireOp",EDGE,"E133.MirrorCS"),sQuery(id+"F1.wireOp",EDGE,"E134.MirrorCS"),sQuery(id+"F1.wireOp",EDGE,"E135.MirrorCS"),sQuery(id+"F1.wireOp",EDGE,"E136.MirrorCS"),sQuery(id+"F1.wireOp",EDGE,"E137.MirrorCS"),sQuery(id+"F1.wireOp",EDGE,"E138.MirrorCS"),sQuery(id+"F1.wireOp",EDGE,"E139.MirrorCS"),sQuery(id+"F1.wireOp",EDGE,"E140.MirrorCS"),sQuery(id+"F1.wireOp",EDGE,"E141.MirrorCS"),sQuery(id+"F1.wireOp",EDGE,"E142.MirrorCS"),sQuery(id+"F1.wireOp",EDGE,"E143.MirrorCS"),sQuery(id+"F1.wireOp",EDGE,"E144.MirrorCS"),sQuery(id+"F1.wireOp",EDGE,"E145.MirrorCS"),sQuery(id+"F1.wireOp",EDGE,"E146.MirrorCS"),sQuery(id+"F1.wireOp",EDGE,"E147.MirrorCS"),sQuery(id+"F1.wireOp",EDGE,"E148.MirrorCS"),sQuery(id+"F1.wireOp",EDGE,"E149.MirrorCS"),sQuery(id+"F1.wireOp",EDGE,"E150.MirrorCS"),sQuery(id+"F1.wireOp",EDGE,"E151.MirrorCS"),sQuery(id+"F1.wireOp",EDGE,"E152.MirrorCS"),sQuery(id+"F1.wireOp",EDGE,"E153.MirrorCS"),sQuery(id+"F1.wireOp",EDGE,"E154.MirrorCS"),sQuery(id+"F1.wireOp",EDGE,"E156.MirrorCS")])],"isStart":true}),makeQuery(id+"F2.opExtrude","SWEPT_FACE",FACE,{"disambiguationData":[OSD([subQ2])]}),makeQuery(id+"F2.opExtrude","SWEPT_FACE",FACE,{"disambiguationData":[OSD([subQ1])]}),makeQuery(id+"F2.opExtrude","SWEPT_FACE",FACE,{"disambiguationData":[OSD([subQ0])]}),makeQuery(id+"F2.opExtrude","SWEPT_FACE",FACE,{"disambiguationData":[OSD([subQ3])]}),makeQuery(id+"F3.opExtrude","SWEPT_FACE",FACE,{"disambiguationData":[OSD([subQ4])]})])],"derivedFrom":makeQuery(id+"F3.opExtrude","CAP_EDGE",EDGE,{"disambiguationData":[OSD([subQ4])],"isStart":true})});}
            var Q14;
            {var subQ0=sQuery(id+"F1.wireOp",EDGE,"E94");var subQ1=sQuery(id+"F1.wireOp",EDGE,"E93");var subQ2=sQuery(id+"F1.wireOp",EDGE,"E92");var subQ3=sQuery(id+"F1.wireOp",EDGE,"E95");var subQ4=sQuery(id+"F0.wireOp",EDGE,"E0");Q14=makeQuery(id+"F3.boolean.opBoolean","SPLIT",EDGE,{"disambiguationData":[TD([makeQuery(id+"F2.opExtrude","CAP_FACE",FACE,{"disambiguationData":[OSD([sQuery(id+"F1.wireOp",EDGE,"E86"),sQuery(id+"F1.wireOp",EDGE,"E87"),sQuery(id+"F1.wireOp",EDGE,"E88"),sQuery(id+"F1.wireOp",EDGE,"E89"),sQuery(id+"F1.wireOp",EDGE,"E90"),sQuery(id+"F1.wireOp",EDGE,"E91"),subQ2,subQ1,subQ0,subQ3,sQuery(id+"F1.wireOp",EDGE,"E96"),sQuery(id+"F1.wireOp",EDGE,"E97"),sQuery(id+"F1.wireOp",EDGE,"E98"),sQuery(id+"F1.wireOp",EDGE,"E99"),sQuery(id+"F1.wireOp",EDGE,"E100.MirrorCS"),sQuery(id+"F1.wireOp",EDGE,"E101.MirrorCS"),sQuery(id+"F1.wireOp",EDGE,"E102.MirrorCS"),sQuery(id+"F1.wireOp",EDGE,"E103.MirrorCS"),sQuery(id+"F1.wireOp",EDGE,"E104.MirrorCS"),sQuery(id+"F1.wireOp",EDGE,"E105.MirrorCS"),sQuery(id+"F1.wireOp",EDGE,"E106.MirrorCS"),sQuery(id+"F1.wireOp",EDGE,"E107.MirrorCS"),sQuery(id+"F1.wireOp",EDGE,"E108.MirrorCS"),sQuery(id+"F1.wireOp",EDGE,"E109.MirrorCS"),sQuery(id+"F1.wireOp",EDGE,"E110.MirrorCS"),sQuery(id+"F1.wireOp",EDGE,"E111.MirrorCS"),sQuery(id+"F1.wireOp",EDGE,"E112.MirrorCS"),sQuery(id+"F1.wireOp",EDGE,"E113.MirrorCS"),sQuery(id+"F1.wireOp",EDGE,"E128.MirrorCS"),sQuery(id+"F1.wireOp",EDGE,"E129.MirrorCS"),sQuery(id+"F1.wireOp",EDGE,"E130.MirrorCS"),sQuery(id+"F1.wireOp",EDGE,"E131.MirrorCS"),sQuery(id+"F1.wireOp",EDGE,"E132.MirrorCS"),sQuery(id+"F1.wireOp",EDGE,"E133.MirrorCS"),sQuery(id+"F1.wireOp",EDGE,"E134.MirrorCS"),sQuery(id+"F1.wireOp",EDGE,"E135.MirrorCS"),sQuery(id+"F1.wireOp",EDGE,"E136.MirrorCS"),sQuery(id+"F1.wireOp",EDGE,"E137.MirrorCS"),sQuery(id+"F1.wireOp",EDGE,"E138.MirrorCS"),sQuery(id+"F1.wireOp",EDGE,"E139.MirrorCS"),sQuery(id+"F1.wireOp",EDGE,"E140.MirrorCS"),sQuery(id+"F1.wireOp",EDGE,"E141.MirrorCS"),sQuery(id+"F1.wireOp",EDGE,"E142.MirrorCS"),sQuery(id+"F1.wireOp",EDGE,"E143.MirrorCS"),sQuery(id+"F1.wireOp",EDGE,"E144.MirrorCS"),sQuery(id+"F1.wireOp",EDGE,"E145.MirrorCS"),sQuery(id+"F1.wireOp",EDGE,"E146.MirrorCS"),sQuery(id+"F1.wireOp",EDGE,"E147.MirrorCS"),sQuery(id+"F1.wireOp",EDGE,"E148.MirrorCS"),sQuery(id+"F1.wireOp",EDGE,"E149.MirrorCS"),sQuery(id+"F1.wireOp",EDGE,"E150.MirrorCS"),sQuery(id+"F1.wireOp",EDGE,"E151.MirrorCS"),sQuery(id+"F1.wireOp",EDGE,"E152.MirrorCS"),sQuery(id+"F1.wireOp",EDGE,"E153.MirrorCS"),sQuery(id+"F1.wireOp",EDGE,"E154.MirrorCS"),sQuery(id+"F1.wireOp",EDGE,"E156.MirrorCS")])],"isStart":true}),makeQuery(id+"F2.opExtrude","SWEPT_FACE",FACE,{"disambiguationData":[OSD([subQ2])]}),makeQuery(id+"F2.opExtrude","SWEPT_FACE",FACE,{"disambiguationData":[OSD([subQ1])]}),makeQuery(id+"F2.opExtrude","SWEPT_FACE",FACE,{"disambiguationData":[OSD([subQ0])]}),makeQuery(id+"F2.opExtrude","SWEPT_FACE",FACE,{"disambiguationData":[OSD([subQ3])]}),makeQuery(id+"F3.opExtrude","SWEPT_FACE",FACE,{"disambiguationData":[OSD([subQ4])]})])],"derivedFrom":makeQuery(id+"F3.opExtrude","CAP_EDGE",EDGE,{"disambiguationData":[OSD([subQ4])],"isStart":true})});}
            var Q15;
            {var subQ0=sQuery(id+"F1.wireOp",EDGE,"E96");var subQ1=sQuery(id+"F1.wireOp",EDGE,"E97");var subQ2=sQuery(id+"F1.wireOp",EDGE,"E95");var subQ3=sQuery(id+"F1.wireOp",EDGE,"E94");var subQ4=sQuery(id+"F0.wireOp",EDGE,"E0");Q15=makeQuery(id+"F3.boolean.opBoolean","SPLIT",EDGE,{"disambiguationData":[TD([makeQuery(id+"F2.opExtrude","CAP_FACE",FACE,{"disambiguationData":[OSD([sQuery(id+"F1.wireOp",EDGE,"E86"),sQuery(id+"F1.wireOp",EDGE,"E87"),sQuery(id+"F1.wireOp",EDGE,"E88"),sQuery(id+"F1.wireOp",EDGE,"E89"),sQuery(id+"F1.wireOp",EDGE,"E90"),sQuery(id+"F1.wireOp",EDGE,"E91"),sQuery(id+"F1.wireOp",EDGE,"E92"),sQuery(id+"F1.wireOp",EDGE,"E93"),subQ3,subQ2,subQ0,subQ1,sQuery(id+"F1.wireOp",EDGE,"E98"),sQuery(id+"F1.wireOp",EDGE,"E99"),sQuery(id+"F1.wireOp",EDGE,"E100.MirrorCS"),sQuery(id+"F1.wireOp",EDGE,"E101.MirrorCS"),sQuery(id+"F1.wireOp",EDGE,"E102.MirrorCS"),sQuery(id+"F1.wireOp",EDGE,"E103.MirrorCS"),sQuery(id+"F1.wireOp",EDGE,"E104.MirrorCS"),sQuery(id+"F1.wireOp",EDGE,"E105.MirrorCS"),sQuery(id+"F1.wireOp",EDGE,"E106.MirrorCS"),sQuery(id+"F1.wireOp",EDGE,"E107.MirrorCS"),sQuery(id+"F1.wireOp",EDGE,"E108.MirrorCS"),sQuery(id+"F1.wireOp",EDGE,"E109.MirrorCS"),sQuery(id+"F1.wireOp",EDGE,"E110.MirrorCS"),sQuery(id+"F1.wireOp",EDGE,"E111.MirrorCS"),sQuery(id+"F1.wireOp",EDGE,"E112.MirrorCS"),sQuery(id+"F1.wireOp",EDGE,"E113.MirrorCS"),sQuery(id+"F1.wireOp",EDGE,"E128.MirrorCS"),sQuery(id+"F1.wireOp",EDGE,"E129.MirrorCS"),sQuery(id+"F1.wireOp",EDGE,"E130.MirrorCS"),sQuery(id+"F1.wireOp",EDGE,"E131.MirrorCS"),sQuery(id+"F1.wireOp",EDGE,"E132.MirrorCS"),sQuery(id+"F1.wireOp",EDGE,"E133.MirrorCS"),sQuery(id+"F1.wireOp",EDGE,"E134.MirrorCS"),sQuery(id+"F1.wireOp",EDGE,"E135.MirrorCS"),sQuery(id+"F1.wireOp",EDGE,"E136.MirrorCS"),sQuery(id+"F1.wireOp",EDGE,"E137.MirrorCS"),sQuery(id+"F1.wireOp",EDGE,"E138.MirrorCS"),sQuery(id+"F1.wireOp",EDGE,"E139.MirrorCS"),sQuery(id+"F1.wireOp",EDGE,"E140.MirrorCS"),sQuery(id+"F1.wireOp",EDGE,"E141.MirrorCS"),sQuery(id+"F1.wireOp",EDGE,"E142.MirrorCS"),sQuery(id+"F1.wireOp",EDGE,"E143.MirrorCS"),sQuery(id+"F1.wireOp",EDGE,"E144.MirrorCS"),sQuery(id+"F1.wireOp",EDGE,"E145.MirrorCS"),sQuery(id+"F1.wireOp",EDGE,"E146.MirrorCS"),sQuery(id+"F1.wireOp",EDGE,"E147.MirrorCS"),sQuery(id+"F1.wireOp",EDGE,"E148.MirrorCS"),sQuery(id+"F1.wireOp",EDGE,"E149.MirrorCS"),sQuery(id+"F1.wireOp",EDGE,"E150.MirrorCS"),sQuery(id+"F1.wireOp",EDGE,"E151.MirrorCS"),sQuery(id+"F1.wireOp",EDGE,"E152.MirrorCS"),sQuery(id+"F1.wireOp",EDGE,"E153.MirrorCS"),sQuery(id+"F1.wireOp",EDGE,"E154.MirrorCS"),sQuery(id+"F1.wireOp",EDGE,"E156.MirrorCS")])],"isStart":true}),makeQuery(id+"F2.opExtrude","SWEPT_FACE",FACE,{"disambiguationData":[OSD([subQ3])]}),makeQuery(id+"F2.opExtrude","SWEPT_FACE",FACE,{"disambiguationData":[OSD([subQ2])]}),makeQuery(id+"F2.opExtrude","SWEPT_FACE",FACE,{"disambiguationData":[OSD([subQ0])]}),makeQuery(id+"F2.opExtrude","SWEPT_FACE",FACE,{"disambiguationData":[OSD([subQ1])]}),makeQuery(id+"F3.opExtrude","SWEPT_FACE",FACE,{"disambiguationData":[OSD([subQ4])]})])],"derivedFrom":makeQuery(id+"F3.opExtrude","CAP_EDGE",EDGE,{"disambiguationData":[OSD([subQ4])],"isStart":true})});}
            var Q16;
            {var subQ0=sQuery(id+"F1.wireOp",EDGE,"E153.MirrorCS");var subQ1=sQuery(id+"F1.wireOp",EDGE,"E143.MirrorCS");var subQ2=sQuery(id+"F1.wireOp",EDGE,"E154.MirrorCS");var subQ3=sQuery(id+"F1.wireOp",EDGE,"E156.MirrorCS");var subQ4=sQuery(id+"F0.wireOp",EDGE,"E0");Q16=makeQuery(id+"F3.boolean.opBoolean","SPLIT",EDGE,{"disambiguationData":[TD([makeQuery(id+"F2.opExtrude","CAP_FACE",FACE,{"disambiguationData":[OSD([sQuery(id+"F1.wireOp",EDGE,"E86"),sQuery(id+"F1.wireOp",EDGE,"E87"),sQuery(id+"F1.wireOp",EDGE,"E88"),sQuery(id+"F1.wireOp",EDGE,"E89"),sQuery(id+"F1.wireOp",EDGE,"E90"),sQuery(id+"F1.wireOp",EDGE,"E91"),sQuery(id+"F1.wireOp",EDGE,"E92"),sQuery(id+"F1.wireOp",EDGE,"E93"),sQuery(id+"F1.wireOp",EDGE,"E94"),sQuery(id+"F1.wireOp",EDGE,"E95"),sQuery(id+"F1.wireOp",EDGE,"E96"),sQuery(id+"F1.wireOp",EDGE,"E97"),sQuery(id+"F1.wireOp",EDGE,"E98"),sQuery(id+"F1.wireOp",EDGE,"E99"),sQuery(id+"F1.wireOp",EDGE,"E100.MirrorCS"),sQuery(id+"F1.wireOp",EDGE,"E101.MirrorCS"),sQuery(id+"F1.wireOp",EDGE,"E102.MirrorCS"),sQuery(id+"F1.wireOp",EDGE,"E103.MirrorCS"),sQuery(id+"F1.wireOp",EDGE,"E104.MirrorCS"),sQuery(id+"F1.wireOp",EDGE,"E105.MirrorCS"),sQuery(id+"F1.wireOp",EDGE,"E106.MirrorCS"),sQuery(id+"F1.wireOp",EDGE,"E107.MirrorCS"),sQuery(id+"F1.wireOp",EDGE,"E108.MirrorCS"),sQuery(id+"F1.wireOp",EDGE,"E109.MirrorCS"),sQuery(id+"F1.wireOp",EDGE,"E110.MirrorCS"),sQuery(id+"F1.wireOp",EDGE,"E111.MirrorCS"),sQuery(id+"F1.wireOp",EDGE,"E112.MirrorCS"),sQuery(id+"F1.wireOp",EDGE,"E113.MirrorCS"),sQuery(id+"F1.wireOp",EDGE,"E128.MirrorCS"),sQuery(id+"F1.wireOp",EDGE,"E129.MirrorCS"),sQuery(id+"F1.wireOp",EDGE,"E130.MirrorCS"),sQuery(id+"F1.wireOp",EDGE,"E131.MirrorCS"),sQuery(id+"F1.wireOp",EDGE,"E132.MirrorCS"),sQuery(id+"F1.wireOp",EDGE,"E133.MirrorCS"),sQuery(id+"F1.wireOp",EDGE,"E134.MirrorCS"),sQuery(id+"F1.wireOp",EDGE,"E135.MirrorCS"),sQuery(id+"F1.wireOp",EDGE,"E136.MirrorCS"),sQuery(id+"F1.wireOp",EDGE,"E137.MirrorCS"),sQuery(id+"F1.wireOp",EDGE,"E138.MirrorCS"),sQuery(id+"F1.wireOp",EDGE,"E139.MirrorCS"),sQuery(id+"F1.wireOp",EDGE,"E140.MirrorCS"),sQuery(id+"F1.wireOp",EDGE,"E141.MirrorCS"),sQuery(id+"F1.wireOp",EDGE,"E142.MirrorCS"),subQ1,sQuery(id+"F1.wireOp",EDGE,"E144.MirrorCS"),sQuery(id+"F1.wireOp",EDGE,"E145.MirrorCS"),sQuery(id+"F1.wireOp",EDGE,"E146.MirrorCS"),sQuery(id+"F1.wireOp",EDGE,"E147.MirrorCS"),sQuery(id+"F1.wireOp",EDGE,"E148.MirrorCS"),sQuery(id+"F1.wireOp",EDGE,"E149.MirrorCS"),sQuery(id+"F1.wireOp",EDGE,"E150.MirrorCS"),sQuery(id+"F1.wireOp",EDGE,"E151.MirrorCS"),sQuery(id+"F1.wireOp",EDGE,"E152.MirrorCS"),subQ0,subQ2,subQ3])],"isStart":true}),makeQuery(id+"F2.opExtrude","SWEPT_FACE",FACE,{"disambiguationData":[OSD([subQ1])]}),makeQuery(id+"F2.opExtrude","SWEPT_FACE",FACE,{"disambiguationData":[OSD([subQ0])]}),makeQuery(id+"F2.opExtrude","SWEPT_FACE",FACE,{"disambiguationData":[OSD([subQ2])]}),makeQuery(id+"F2.opExtrude","SWEPT_FACE",FACE,{"disambiguationData":[OSD([subQ3])]}),makeQuery(id+"F3.opExtrude","SWEPT_FACE",FACE,{"disambiguationData":[OSD([subQ4])]})])],"derivedFrom":makeQuery(id+"F3.opExtrude","CAP_EDGE",EDGE,{"disambiguationData":[OSD([subQ4])],"isStart":true})});}
            var Q17;
            {var subQ0=sQuery(id+"F1.wireOp",EDGE,"E153.MirrorCS");var subQ1=sQuery(id+"F1.wireOp",EDGE,"E147.MirrorCS");var subQ2=sQuery(id+"F1.wireOp",EDGE,"E132.MirrorCS");var subQ3=sQuery(id+"F1.wireOp",EDGE,"E156.MirrorCS");var subQ4=sQuery(id+"F0.wireOp",EDGE,"E0");Q17=makeQuery(id+"F3.boolean.opBoolean","SPLIT",EDGE,{"disambiguationData":[TD([makeQuery(id+"F2.opExtrude","CAP_FACE",FACE,{"disambiguationData":[OSD([sQuery(id+"F1.wireOp",EDGE,"E86"),sQuery(id+"F1.wireOp",EDGE,"E87"),sQuery(id+"F1.wireOp",EDGE,"E88"),sQuery(id+"F1.wireOp",EDGE,"E89"),sQuery(id+"F1.wireOp",EDGE,"E90"),sQuery(id+"F1.wireOp",EDGE,"E91"),sQuery(id+"F1.wireOp",EDGE,"E92"),sQuery(id+"F1.wireOp",EDGE,"E93"),sQuery(id+"F1.wireOp",EDGE,"E94"),sQuery(id+"F1.wireOp",EDGE,"E95"),sQuery(id+"F1.wireOp",EDGE,"E96"),sQuery(id+"F1.wireOp",EDGE,"E97"),sQuery(id+"F1.wireOp",EDGE,"E98"),sQuery(id+"F1.wireOp",EDGE,"E99"),sQuery(id+"F1.wireOp",EDGE,"E100.MirrorCS"),sQuery(id+"F1.wireOp",EDGE,"E101.MirrorCS"),sQuery(id+"F1.wireOp",EDGE,"E102.MirrorCS"),sQuery(id+"F1.wireOp",EDGE,"E103.MirrorCS"),sQuery(id+"F1.wireOp",EDGE,"E104.MirrorCS"),sQuery(id+"F1.wireOp",EDGE,"E105.MirrorCS"),sQuery(id+"F1.wireOp",EDGE,"E106.MirrorCS"),sQuery(id+"F1.wireOp",EDGE,"E107.MirrorCS"),sQuery(id+"F1.wireOp",EDGE,"E108.MirrorCS"),sQuery(id+"F1.wireOp",EDGE,"E109.MirrorCS"),sQuery(id+"F1.wireOp",EDGE,"E110.MirrorCS"),sQuery(id+"F1.wireOp",EDGE,"E111.MirrorCS"),sQuery(id+"F1.wireOp",EDGE,"E112.MirrorCS"),sQuery(id+"F1.wireOp",EDGE,"E113.MirrorCS"),sQuery(id+"F1.wireOp",EDGE,"E128.MirrorCS"),sQuery(id+"F1.wireOp",EDGE,"E129.MirrorCS"),sQuery(id+"F1.wireOp",EDGE,"E130.MirrorCS"),sQuery(id+"F1.wireOp",EDGE,"E131.MirrorCS"),subQ2,sQuery(id+"F1.wireOp",EDGE,"E133.MirrorCS"),sQuery(id+"F1.wireOp",EDGE,"E134.MirrorCS"),sQuery(id+"F1.wireOp",EDGE,"E135.MirrorCS"),sQuery(id+"F1.wireOp",EDGE,"E136.MirrorCS"),sQuery(id+"F1.wireOp",EDGE,"E137.MirrorCS"),sQuery(id+"F1.wireOp",EDGE,"E138.MirrorCS"),sQuery(id+"F1.wireOp",EDGE,"E139.MirrorCS"),sQuery(id+"F1.wireOp",EDGE,"E140.MirrorCS"),sQuery(id+"F1.wireOp",EDGE,"E141.MirrorCS"),sQuery(id+"F1.wireOp",EDGE,"E142.MirrorCS"),sQuery(id+"F1.wireOp",EDGE,"E143.MirrorCS"),sQuery(id+"F1.wireOp",EDGE,"E144.MirrorCS"),sQuery(id+"F1.wireOp",EDGE,"E145.MirrorCS"),sQuery(id+"F1.wireOp",EDGE,"E146.MirrorCS"),subQ1,sQuery(id+"F1.wireOp",EDGE,"E148.MirrorCS"),sQuery(id+"F1.wireOp",EDGE,"E149.MirrorCS"),sQuery(id+"F1.wireOp",EDGE,"E150.MirrorCS"),sQuery(id+"F1.wireOp",EDGE,"E151.MirrorCS"),sQuery(id+"F1.wireOp",EDGE,"E152.MirrorCS"),subQ0,sQuery(id+"F1.wireOp",EDGE,"E154.MirrorCS"),subQ3])],"isStart":true}),makeQuery(id+"F2.opExtrude","SWEPT_FACE",FACE,{"disambiguationData":[OSD([subQ2])]}),makeQuery(id+"F2.opExtrude","SWEPT_FACE",FACE,{"disambiguationData":[OSD([subQ1])]}),makeQuery(id+"F2.opExtrude","SWEPT_FACE",FACE,{"disambiguationData":[OSD([subQ0])]}),makeQuery(id+"F2.opExtrude","SWEPT_FACE",FACE,{"disambiguationData":[OSD([subQ3])]}),makeQuery(id+"F3.opExtrude","SWEPT_FACE",FACE,{"disambiguationData":[OSD([subQ4])]})])],"derivedFrom":makeQuery(id+"F3.opExtrude","CAP_EDGE",EDGE,{"disambiguationData":[OSD([subQ4])],"isStart":true})});}
            var Q18;
            {var subQ0=sQuery(id+"F1.wireOp",EDGE,"E146.MirrorCS");var subQ1=sQuery(id+"F0.wireOp",EDGE,"E0");var subQ2=sQuery(id+"F1.wireOp",EDGE,"E142.MirrorCS");var subQ3=sQuery(id+"F1.wireOp",EDGE,"E132.MirrorCS");var subQ4=sQuery(id+"F1.wireOp",EDGE,"E147.MirrorCS");Q18=makeQuery(id+"F3.boolean.opBoolean","SPLIT",EDGE,{"disambiguationData":[TD([makeQuery(id+"F2.opExtrude","CAP_FACE",FACE,{"disambiguationData":[OSD([sQuery(id+"F1.wireOp",EDGE,"E86"),sQuery(id+"F1.wireOp",EDGE,"E87"),sQuery(id+"F1.wireOp",EDGE,"E88"),sQuery(id+"F1.wireOp",EDGE,"E89"),sQuery(id+"F1.wireOp",EDGE,"E90"),sQuery(id+"F1.wireOp",EDGE,"E91"),sQuery(id+"F1.wireOp",EDGE,"E92"),sQuery(id+"F1.wireOp",EDGE,"E93"),sQuery(id+"F1.wireOp",EDGE,"E94"),sQuery(id+"F1.wireOp",EDGE,"E95"),sQuery(id+"F1.wireOp",EDGE,"E96"),sQuery(id+"F1.wireOp",EDGE,"E97"),sQuery(id+"F1.wireOp",EDGE,"E98"),sQuery(id+"F1.wireOp",EDGE,"E99"),sQuery(id+"F1.wireOp",EDGE,"E100.MirrorCS"),sQuery(id+"F1.wireOp",EDGE,"E101.MirrorCS"),sQuery(id+"F1.wireOp",EDGE,"E102.MirrorCS"),sQuery(id+"F1.wireOp",EDGE,"E103.MirrorCS"),sQuery(id+"F1.wireOp",EDGE,"E104.MirrorCS"),sQuery(id+"F1.wireOp",EDGE,"E105.MirrorCS"),sQuery(id+"F1.wireOp",EDGE,"E106.MirrorCS"),sQuery(id+"F1.wireOp",EDGE,"E107.MirrorCS"),sQuery(id+"F1.wireOp",EDGE,"E108.MirrorCS"),sQuery(id+"F1.wireOp",EDGE,"E109.MirrorCS"),sQuery(id+"F1.wireOp",EDGE,"E110.MirrorCS"),sQuery(id+"F1.wireOp",EDGE,"E111.MirrorCS"),sQuery(id+"F1.wireOp",EDGE,"E112.MirrorCS"),sQuery(id+"F1.wireOp",EDGE,"E113.MirrorCS"),sQuery(id+"F1.wireOp",EDGE,"E128.MirrorCS"),sQuery(id+"F1.wireOp",EDGE,"E129.MirrorCS"),sQuery(id+"F1.wireOp",EDGE,"E130.MirrorCS"),sQuery(id+"F1.wireOp",EDGE,"E131.MirrorCS"),subQ3,sQuery(id+"F1.wireOp",EDGE,"E133.MirrorCS"),sQuery(id+"F1.wireOp",EDGE,"E134.MirrorCS"),sQuery(id+"F1.wireOp",EDGE,"E135.MirrorCS"),sQuery(id+"F1.wireOp",EDGE,"E136.MirrorCS"),sQuery(id+"F1.wireOp",EDGE,"E137.MirrorCS"),sQuery(id+"F1.wireOp",EDGE,"E138.MirrorCS"),sQuery(id+"F1.wireOp",EDGE,"E139.MirrorCS"),sQuery(id+"F1.wireOp",EDGE,"E140.MirrorCS"),sQuery(id+"F1.wireOp",EDGE,"E141.MirrorCS"),subQ2,sQuery(id+"F1.wireOp",EDGE,"E143.MirrorCS"),sQuery(id+"F1.wireOp",EDGE,"E144.MirrorCS"),sQuery(id+"F1.wireOp",EDGE,"E145.MirrorCS"),subQ0,subQ4,sQuery(id+"F1.wireOp",EDGE,"E148.MirrorCS"),sQuery(id+"F1.wireOp",EDGE,"E149.MirrorCS"),sQuery(id+"F1.wireOp",EDGE,"E150.MirrorCS"),sQuery(id+"F1.wireOp",EDGE,"E151.MirrorCS"),sQuery(id+"F1.wireOp",EDGE,"E152.MirrorCS"),sQuery(id+"F1.wireOp",EDGE,"E153.MirrorCS"),sQuery(id+"F1.wireOp",EDGE,"E154.MirrorCS"),sQuery(id+"F1.wireOp",EDGE,"E156.MirrorCS")])],"isStart":true}),makeQuery(id+"F2.opExtrude","SWEPT_FACE",FACE,{"disambiguationData":[OSD([subQ3])]}),makeQuery(id+"F2.opExtrude","SWEPT_FACE",FACE,{"disambiguationData":[OSD([subQ2])]}),makeQuery(id+"F2.opExtrude","SWEPT_FACE",FACE,{"disambiguationData":[OSD([subQ0])]}),makeQuery(id+"F2.opExtrude","SWEPT_FACE",FACE,{"disambiguationData":[OSD([subQ4])]}),makeQuery(id+"F3.opExtrude","SWEPT_FACE",FACE,{"disambiguationData":[OSD([subQ1])]})])],"derivedFrom":makeQuery(id+"F3.opExtrude","CAP_EDGE",EDGE,{"disambiguationData":[OSD([subQ1])],"isStart":true})});}
            var Q19;
            {var subQ0=sQuery(id+"F1.wireOp",EDGE,"E142.MirrorCS");var subQ1=sQuery(id+"F1.wireOp",EDGE,"E141.MirrorCS");var subQ2=sQuery(id+"F1.wireOp",EDGE,"E140.MirrorCS");var subQ3=sQuery(id+"F1.wireOp",EDGE,"E146.MirrorCS");var subQ4=sQuery(id+"F0.wireOp",EDGE,"E0");Q19=makeQuery(id+"F3.boolean.opBoolean","SPLIT",EDGE,{"disambiguationData":[TD([makeQuery(id+"F2.opExtrude","CAP_FACE",FACE,{"disambiguationData":[OSD([sQuery(id+"F1.wireOp",EDGE,"E86"),sQuery(id+"F1.wireOp",EDGE,"E87"),sQuery(id+"F1.wireOp",EDGE,"E88"),sQuery(id+"F1.wireOp",EDGE,"E89"),sQuery(id+"F1.wireOp",EDGE,"E90"),sQuery(id+"F1.wireOp",EDGE,"E91"),sQuery(id+"F1.wireOp",EDGE,"E92"),sQuery(id+"F1.wireOp",EDGE,"E93"),sQuery(id+"F1.wireOp",EDGE,"E94"),sQuery(id+"F1.wireOp",EDGE,"E95"),sQuery(id+"F1.wireOp",EDGE,"E96"),sQuery(id+"F1.wireOp",EDGE,"E97"),sQuery(id+"F1.wireOp",EDGE,"E98"),sQuery(id+"F1.wireOp",EDGE,"E99"),sQuery(id+"F1.wireOp",EDGE,"E100.MirrorCS"),sQuery(id+"F1.wireOp",EDGE,"E101.MirrorCS"),sQuery(id+"F1.wireOp",EDGE,"E102.MirrorCS"),sQuery(id+"F1.wireOp",EDGE,"E103.MirrorCS"),sQuery(id+"F1.wireOp",EDGE,"E104.MirrorCS"),sQuery(id+"F1.wireOp",EDGE,"E105.MirrorCS"),sQuery(id+"F1.wireOp",EDGE,"E106.MirrorCS"),sQuery(id+"F1.wireOp",EDGE,"E107.MirrorCS"),sQuery(id+"F1.wireOp",EDGE,"E108.MirrorCS"),sQuery(id+"F1.wireOp",EDGE,"E109.MirrorCS"),sQuery(id+"F1.wireOp",EDGE,"E110.MirrorCS"),sQuery(id+"F1.wireOp",EDGE,"E111.MirrorCS"),sQuery(id+"F1.wireOp",EDGE,"E112.MirrorCS"),sQuery(id+"F1.wireOp",EDGE,"E113.MirrorCS"),sQuery(id+"F1.wireOp",EDGE,"E128.MirrorCS"),sQuery(id+"F1.wireOp",EDGE,"E129.MirrorCS"),sQuery(id+"F1.wireOp",EDGE,"E130.MirrorCS"),sQuery(id+"F1.wireOp",EDGE,"E131.MirrorCS"),sQuery(id+"F1.wireOp",EDGE,"E132.MirrorCS"),sQuery(id+"F1.wireOp",EDGE,"E133.MirrorCS"),sQuery(id+"F1.wireOp",EDGE,"E134.MirrorCS"),sQuery(id+"F1.wireOp",EDGE,"E135.MirrorCS"),sQuery(id+"F1.wireOp",EDGE,"E136.MirrorCS"),sQuery(id+"F1.wireOp",EDGE,"E137.MirrorCS"),sQuery(id+"F1.wireOp",EDGE,"E138.MirrorCS"),sQuery(id+"F1.wireOp",EDGE,"E139.MirrorCS"),subQ2,subQ1,subQ0,sQuery(id+"F1.wireOp",EDGE,"E143.MirrorCS"),sQuery(id+"F1.wireOp",EDGE,"E144.MirrorCS"),sQuery(id+"F1.wireOp",EDGE,"E145.MirrorCS"),subQ3,sQuery(id+"F1.wireOp",EDGE,"E147.MirrorCS"),sQuery(id+"F1.wireOp",EDGE,"E148.MirrorCS"),sQuery(id+"F1.wireOp",EDGE,"E149.MirrorCS"),sQuery(id+"F1.wireOp",EDGE,"E150.MirrorCS"),sQuery(id+"F1.wireOp",EDGE,"E151.MirrorCS"),sQuery(id+"F1.wireOp",EDGE,"E152.MirrorCS"),sQuery(id+"F1.wireOp",EDGE,"E153.MirrorCS"),sQuery(id+"F1.wireOp",EDGE,"E154.MirrorCS"),sQuery(id+"F1.wireOp",EDGE,"E156.MirrorCS")])],"isStart":true}),makeQuery(id+"F2.opExtrude","SWEPT_FACE",FACE,{"disambiguationData":[OSD([subQ2])]}),makeQuery(id+"F2.opExtrude","SWEPT_FACE",FACE,{"disambiguationData":[OSD([subQ1])]}),makeQuery(id+"F2.opExtrude","SWEPT_FACE",FACE,{"disambiguationData":[OSD([subQ0])]}),makeQuery(id+"F2.opExtrude","SWEPT_FACE",FACE,{"disambiguationData":[OSD([subQ3])]}),makeQuery(id+"F3.opExtrude","SWEPT_FACE",FACE,{"disambiguationData":[OSD([subQ4])]})])],"derivedFrom":makeQuery(id+"F3.opExtrude","CAP_EDGE",EDGE,{"disambiguationData":[OSD([subQ4])],"isStart":true})});}
            var Q20;
            {var subQ0=sQuery(id+"F1.wireOp",EDGE,"E140.MirrorCS");var subQ1=sQuery(id+"F1.wireOp",EDGE,"E138.MirrorCS");var subQ2=sQuery(id+"F1.wireOp",EDGE,"E139.MirrorCS");var subQ3=sQuery(id+"F1.wireOp",EDGE,"E141.MirrorCS");var subQ4=sQuery(id+"F0.wireOp",EDGE,"E0");Q20=makeQuery(id+"F3.boolean.opBoolean","SPLIT",EDGE,{"disambiguationData":[TD([makeQuery(id+"F2.opExtrude","CAP_FACE",FACE,{"disambiguationData":[OSD([sQuery(id+"F1.wireOp",EDGE,"E86"),sQuery(id+"F1.wireOp",EDGE,"E87"),sQuery(id+"F1.wireOp",EDGE,"E88"),sQuery(id+"F1.wireOp",EDGE,"E89"),sQuery(id+"F1.wireOp",EDGE,"E90"),sQuery(id+"F1.wireOp",EDGE,"E91"),sQuery(id+"F1.wireOp",EDGE,"E92"),sQuery(id+"F1.wireOp",EDGE,"E93"),sQuery(id+"F1.wireOp",EDGE,"E94"),sQuery(id+"F1.wireOp",EDGE,"E95"),sQuery(id+"F1.wireOp",EDGE,"E96"),sQuery(id+"F1.wireOp",EDGE,"E97"),sQuery(id+"F1.wireOp",EDGE,"E98"),sQuery(id+"F1.wireOp",EDGE,"E99"),sQuery(id+"F1.wireOp",EDGE,"E100.MirrorCS"),sQuery(id+"F1.wireOp",EDGE,"E101.MirrorCS"),sQuery(id+"F1.wireOp",EDGE,"E102.MirrorCS"),sQuery(id+"F1.wireOp",EDGE,"E103.MirrorCS"),sQuery(id+"F1.wireOp",EDGE,"E104.MirrorCS"),sQuery(id+"F1.wireOp",EDGE,"E105.MirrorCS"),sQuery(id+"F1.wireOp",EDGE,"E106.MirrorCS"),sQuery(id+"F1.wireOp",EDGE,"E107.MirrorCS"),sQuery(id+"F1.wireOp",EDGE,"E108.MirrorCS"),sQuery(id+"F1.wireOp",EDGE,"E109.MirrorCS"),sQuery(id+"F1.wireOp",EDGE,"E110.MirrorCS"),sQuery(id+"F1.wireOp",EDGE,"E111.MirrorCS"),sQuery(id+"F1.wireOp",EDGE,"E112.MirrorCS"),sQuery(id+"F1.wireOp",EDGE,"E113.MirrorCS"),sQuery(id+"F1.wireOp",EDGE,"E128.MirrorCS"),sQuery(id+"F1.wireOp",EDGE,"E129.MirrorCS"),sQuery(id+"F1.wireOp",EDGE,"E130.MirrorCS"),sQuery(id+"F1.wireOp",EDGE,"E131.MirrorCS"),sQuery(id+"F1.wireOp",EDGE,"E132.MirrorCS"),sQuery(id+"F1.wireOp",EDGE,"E133.MirrorCS"),sQuery(id+"F1.wireOp",EDGE,"E134.MirrorCS"),sQuery(id+"F1.wireOp",EDGE,"E135.MirrorCS"),sQuery(id+"F1.wireOp",EDGE,"E136.MirrorCS"),sQuery(id+"F1.wireOp",EDGE,"E137.MirrorCS"),subQ1,subQ2,subQ0,subQ3,sQuery(id+"F1.wireOp",EDGE,"E142.MirrorCS"),sQuery(id+"F1.wireOp",EDGE,"E143.MirrorCS"),sQuery(id+"F1.wireOp",EDGE,"E144.MirrorCS"),sQuery(id+"F1.wireOp",EDGE,"E145.MirrorCS"),sQuery(id+"F1.wireOp",EDGE,"E146.MirrorCS"),sQuery(id+"F1.wireOp",EDGE,"E147.MirrorCS"),sQuery(id+"F1.wireOp",EDGE,"E148.MirrorCS"),sQuery(id+"F1.wireOp",EDGE,"E149.MirrorCS"),sQuery(id+"F1.wireOp",EDGE,"E150.MirrorCS"),sQuery(id+"F1.wireOp",EDGE,"E151.MirrorCS"),sQuery(id+"F1.wireOp",EDGE,"E152.MirrorCS"),sQuery(id+"F1.wireOp",EDGE,"E153.MirrorCS"),sQuery(id+"F1.wireOp",EDGE,"E154.MirrorCS"),sQuery(id+"F1.wireOp",EDGE,"E156.MirrorCS")])],"isStart":true}),makeQuery(id+"F2.opExtrude","SWEPT_FACE",FACE,{"disambiguationData":[OSD([subQ1])]}),makeQuery(id+"F2.opExtrude","SWEPT_FACE",FACE,{"disambiguationData":[OSD([subQ2])]}),makeQuery(id+"F2.opExtrude","SWEPT_FACE",FACE,{"disambiguationData":[OSD([subQ0])]}),makeQuery(id+"F2.opExtrude","SWEPT_FACE",FACE,{"disambiguationData":[OSD([subQ3])]}),makeQuery(id+"F3.opExtrude","SWEPT_FACE",FACE,{"disambiguationData":[OSD([subQ4])]})])],"derivedFrom":makeQuery(id+"F3.opExtrude","CAP_EDGE",EDGE,{"disambiguationData":[OSD([subQ4])],"isStart":true})});}
            var Q21;
            {var subQ0=sQuery(id+"F1.wireOp",EDGE,"E138.MirrorCS");var subQ1=sQuery(id+"F1.wireOp",EDGE,"E136.MirrorCS");var subQ2=sQuery(id+"F1.wireOp",EDGE,"E139.MirrorCS");var subQ3=sQuery(id+"F1.wireOp",EDGE,"E152.MirrorCS");var subQ4=sQuery(id+"F0.wireOp",EDGE,"E0");Q21=makeQuery(id+"F3.boolean.opBoolean","SPLIT",EDGE,{"disambiguationData":[TD([makeQuery(id+"F2.opExtrude","CAP_FACE",FACE,{"disambiguationData":[OSD([sQuery(id+"F1.wireOp",EDGE,"E86"),sQuery(id+"F1.wireOp",EDGE,"E87"),sQuery(id+"F1.wireOp",EDGE,"E88"),sQuery(id+"F1.wireOp",EDGE,"E89"),sQuery(id+"F1.wireOp",EDGE,"E90"),sQuery(id+"F1.wireOp",EDGE,"E91"),sQuery(id+"F1.wireOp",EDGE,"E92"),sQuery(id+"F1.wireOp",EDGE,"E93"),sQuery(id+"F1.wireOp",EDGE,"E94"),sQuery(id+"F1.wireOp",EDGE,"E95"),sQuery(id+"F1.wireOp",EDGE,"E96"),sQuery(id+"F1.wireOp",EDGE,"E97"),sQuery(id+"F1.wireOp",EDGE,"E98"),sQuery(id+"F1.wireOp",EDGE,"E99"),sQuery(id+"F1.wireOp",EDGE,"E100.MirrorCS"),sQuery(id+"F1.wireOp",EDGE,"E101.MirrorCS"),sQuery(id+"F1.wireOp",EDGE,"E102.MirrorCS"),sQuery(id+"F1.wireOp",EDGE,"E103.MirrorCS"),sQuery(id+"F1.wireOp",EDGE,"E104.MirrorCS"),sQuery(id+"F1.wireOp",EDGE,"E105.MirrorCS"),sQuery(id+"F1.wireOp",EDGE,"E106.MirrorCS"),sQuery(id+"F1.wireOp",EDGE,"E107.MirrorCS"),sQuery(id+"F1.wireOp",EDGE,"E108.MirrorCS"),sQuery(id+"F1.wireOp",EDGE,"E109.MirrorCS"),sQuery(id+"F1.wireOp",EDGE,"E110.MirrorCS"),sQuery(id+"F1.wireOp",EDGE,"E111.MirrorCS"),sQuery(id+"F1.wireOp",EDGE,"E112.MirrorCS"),sQuery(id+"F1.wireOp",EDGE,"E113.MirrorCS"),sQuery(id+"F1.wireOp",EDGE,"E128.MirrorCS"),sQuery(id+"F1.wireOp",EDGE,"E129.MirrorCS"),sQuery(id+"F1.wireOp",EDGE,"E130.MirrorCS"),sQuery(id+"F1.wireOp",EDGE,"E131.MirrorCS"),sQuery(id+"F1.wireOp",EDGE,"E132.MirrorCS"),sQuery(id+"F1.wireOp",EDGE,"E133.MirrorCS"),sQuery(id+"F1.wireOp",EDGE,"E134.MirrorCS"),sQuery(id+"F1.wireOp",EDGE,"E135.MirrorCS"),subQ1,sQuery(id+"F1.wireOp",EDGE,"E137.MirrorCS"),subQ0,subQ2,sQuery(id+"F1.wireOp",EDGE,"E140.MirrorCS"),sQuery(id+"F1.wireOp",EDGE,"E141.MirrorCS"),sQuery(id+"F1.wireOp",EDGE,"E142.MirrorCS"),sQuery(id+"F1.wireOp",EDGE,"E143.MirrorCS"),sQuery(id+"F1.wireOp",EDGE,"E144.MirrorCS"),sQuery(id+"F1.wireOp",EDGE,"E145.MirrorCS"),sQuery(id+"F1.wireOp",EDGE,"E146.MirrorCS"),sQuery(id+"F1.wireOp",EDGE,"E147.MirrorCS"),sQuery(id+"F1.wireOp",EDGE,"E148.MirrorCS"),sQuery(id+"F1.wireOp",EDGE,"E149.MirrorCS"),sQuery(id+"F1.wireOp",EDGE,"E150.MirrorCS"),sQuery(id+"F1.wireOp",EDGE,"E151.MirrorCS"),subQ3,sQuery(id+"F1.wireOp",EDGE,"E153.MirrorCS"),sQuery(id+"F1.wireOp",EDGE,"E154.MirrorCS"),sQuery(id+"F1.wireOp",EDGE,"E156.MirrorCS")])],"isStart":true}),makeQuery(id+"F2.opExtrude","SWEPT_FACE",FACE,{"disambiguationData":[OSD([subQ1])]}),makeQuery(id+"F2.opExtrude","SWEPT_FACE",FACE,{"disambiguationData":[OSD([subQ0])]}),makeQuery(id+"F2.opExtrude","SWEPT_FACE",FACE,{"disambiguationData":[OSD([subQ2])]}),makeQuery(id+"F2.opExtrude","SWEPT_FACE",FACE,{"disambiguationData":[OSD([subQ3])]}),makeQuery(id+"F3.opExtrude","SWEPT_FACE",FACE,{"disambiguationData":[OSD([subQ4])]})])],"derivedFrom":makeQuery(id+"F3.opExtrude","CAP_EDGE",EDGE,{"disambiguationData":[OSD([subQ4])],"isStart":true})});}
            var Q22;
            {var subQ0=sQuery(id+"F1.wireOp",EDGE,"E150.MirrorCS");var subQ1=sQuery(id+"F1.wireOp",EDGE,"E151.MirrorCS");var subQ2=sQuery(id+"F1.wireOp",EDGE,"E136.MirrorCS");var subQ3=sQuery(id+"F1.wireOp",EDGE,"E152.MirrorCS");var subQ4=sQuery(id+"F0.wireOp",EDGE,"E0");Q22=makeQuery(id+"F3.boolean.opBoolean","SPLIT",EDGE,{"disambiguationData":[TD([makeQuery(id+"F2.opExtrude","CAP_FACE",FACE,{"disambiguationData":[OSD([sQuery(id+"F1.wireOp",EDGE,"E86"),sQuery(id+"F1.wireOp",EDGE,"E87"),sQuery(id+"F1.wireOp",EDGE,"E88"),sQuery(id+"F1.wireOp",EDGE,"E89"),sQuery(id+"F1.wireOp",EDGE,"E90"),sQuery(id+"F1.wireOp",EDGE,"E91"),sQuery(id+"F1.wireOp",EDGE,"E92"),sQuery(id+"F1.wireOp",EDGE,"E93"),sQuery(id+"F1.wireOp",EDGE,"E94"),sQuery(id+"F1.wireOp",EDGE,"E95"),sQuery(id+"F1.wireOp",EDGE,"E96"),sQuery(id+"F1.wireOp",EDGE,"E97"),sQuery(id+"F1.wireOp",EDGE,"E98"),sQuery(id+"F1.wireOp",EDGE,"E99"),sQuery(id+"F1.wireOp",EDGE,"E100.MirrorCS"),sQuery(id+"F1.wireOp",EDGE,"E101.MirrorCS"),sQuery(id+"F1.wireOp",EDGE,"E102.MirrorCS"),sQuery(id+"F1.wireOp",EDGE,"E103.MirrorCS"),sQuery(id+"F1.wireOp",EDGE,"E104.MirrorCS"),sQuery(id+"F1.wireOp",EDGE,"E105.MirrorCS"),sQuery(id+"F1.wireOp",EDGE,"E106.MirrorCS"),sQuery(id+"F1.wireOp",EDGE,"E107.MirrorCS"),sQuery(id+"F1.wireOp",EDGE,"E108.MirrorCS"),sQuery(id+"F1.wireOp",EDGE,"E109.MirrorCS"),sQuery(id+"F1.wireOp",EDGE,"E110.MirrorCS"),sQuery(id+"F1.wireOp",EDGE,"E111.MirrorCS"),sQuery(id+"F1.wireOp",EDGE,"E112.MirrorCS"),sQuery(id+"F1.wireOp",EDGE,"E113.MirrorCS"),sQuery(id+"F1.wireOp",EDGE,"E128.MirrorCS"),sQuery(id+"F1.wireOp",EDGE,"E129.MirrorCS"),sQuery(id+"F1.wireOp",EDGE,"E130.MirrorCS"),sQuery(id+"F1.wireOp",EDGE,"E131.MirrorCS"),sQuery(id+"F1.wireOp",EDGE,"E132.MirrorCS"),sQuery(id+"F1.wireOp",EDGE,"E133.MirrorCS"),sQuery(id+"F1.wireOp",EDGE,"E134.MirrorCS"),sQuery(id+"F1.wireOp",EDGE,"E135.MirrorCS"),subQ2,sQuery(id+"F1.wireOp",EDGE,"E137.MirrorCS"),sQuery(id+"F1.wireOp",EDGE,"E138.MirrorCS"),sQuery(id+"F1.wireOp",EDGE,"E139.MirrorCS"),sQuery(id+"F1.wireOp",EDGE,"E140.MirrorCS"),sQuery(id+"F1.wireOp",EDGE,"E141.MirrorCS"),sQuery(id+"F1.wireOp",EDGE,"E142.MirrorCS"),sQuery(id+"F1.wireOp",EDGE,"E143.MirrorCS"),sQuery(id+"F1.wireOp",EDGE,"E144.MirrorCS"),sQuery(id+"F1.wireOp",EDGE,"E145.MirrorCS"),sQuery(id+"F1.wireOp",EDGE,"E146.MirrorCS"),sQuery(id+"F1.wireOp",EDGE,"E147.MirrorCS"),sQuery(id+"F1.wireOp",EDGE,"E148.MirrorCS"),sQuery(id+"F1.wireOp",EDGE,"E149.MirrorCS"),subQ0,subQ1,subQ3,sQuery(id+"F1.wireOp",EDGE,"E153.MirrorCS"),sQuery(id+"F1.wireOp",EDGE,"E154.MirrorCS"),sQuery(id+"F1.wireOp",EDGE,"E156.MirrorCS")])],"isStart":true}),makeQuery(id+"F2.opExtrude","SWEPT_FACE",FACE,{"disambiguationData":[OSD([subQ2])]}),makeQuery(id+"F2.opExtrude","SWEPT_FACE",FACE,{"disambiguationData":[OSD([subQ0])]}),makeQuery(id+"F2.opExtrude","SWEPT_FACE",FACE,{"disambiguationData":[OSD([subQ1])]}),makeQuery(id+"F2.opExtrude","SWEPT_FACE",FACE,{"disambiguationData":[OSD([subQ3])]}),makeQuery(id+"F3.opExtrude","SWEPT_FACE",FACE,{"disambiguationData":[OSD([subQ4])]})])],"derivedFrom":makeQuery(id+"F3.opExtrude","CAP_EDGE",EDGE,{"disambiguationData":[OSD([subQ4])],"isStart":true})});}
            var Q23;
            {var subQ0=sQuery(id+"F1.wireOp",EDGE,"E150.MirrorCS");var subQ1=sQuery(id+"F1.wireOp",EDGE,"E133.MirrorCS");var subQ2=sQuery(id+"F1.wireOp",EDGE,"E134.MirrorCS");var subQ3=sQuery(id+"F1.wireOp",EDGE,"E151.MirrorCS");var subQ4=sQuery(id+"F0.wireOp",EDGE,"E0");Q23=makeQuery(id+"F3.boolean.opBoolean","SPLIT",EDGE,{"disambiguationData":[TD([makeQuery(id+"F2.opExtrude","CAP_FACE",FACE,{"disambiguationData":[OSD([sQuery(id+"F1.wireOp",EDGE,"E86"),sQuery(id+"F1.wireOp",EDGE,"E87"),sQuery(id+"F1.wireOp",EDGE,"E88"),sQuery(id+"F1.wireOp",EDGE,"E89"),sQuery(id+"F1.wireOp",EDGE,"E90"),sQuery(id+"F1.wireOp",EDGE,"E91"),sQuery(id+"F1.wireOp",EDGE,"E92"),sQuery(id+"F1.wireOp",EDGE,"E93"),sQuery(id+"F1.wireOp",EDGE,"E94"),sQuery(id+"F1.wireOp",EDGE,"E95"),sQuery(id+"F1.wireOp",EDGE,"E96"),sQuery(id+"F1.wireOp",EDGE,"E97"),sQuery(id+"F1.wireOp",EDGE,"E98"),sQuery(id+"F1.wireOp",EDGE,"E99"),sQuery(id+"F1.wireOp",EDGE,"E100.MirrorCS"),sQuery(id+"F1.wireOp",EDGE,"E101.MirrorCS"),sQuery(id+"F1.wireOp",EDGE,"E102.MirrorCS"),sQuery(id+"F1.wireOp",EDGE,"E103.MirrorCS"),sQuery(id+"F1.wireOp",EDGE,"E104.MirrorCS"),sQuery(id+"F1.wireOp",EDGE,"E105.MirrorCS"),sQuery(id+"F1.wireOp",EDGE,"E106.MirrorCS"),sQuery(id+"F1.wireOp",EDGE,"E107.MirrorCS"),sQuery(id+"F1.wireOp",EDGE,"E108.MirrorCS"),sQuery(id+"F1.wireOp",EDGE,"E109.MirrorCS"),sQuery(id+"F1.wireOp",EDGE,"E110.MirrorCS"),sQuery(id+"F1.wireOp",EDGE,"E111.MirrorCS"),sQuery(id+"F1.wireOp",EDGE,"E112.MirrorCS"),sQuery(id+"F1.wireOp",EDGE,"E113.MirrorCS"),sQuery(id+"F1.wireOp",EDGE,"E128.MirrorCS"),sQuery(id+"F1.wireOp",EDGE,"E129.MirrorCS"),sQuery(id+"F1.wireOp",EDGE,"E130.MirrorCS"),sQuery(id+"F1.wireOp",EDGE,"E131.MirrorCS"),sQuery(id+"F1.wireOp",EDGE,"E132.MirrorCS"),subQ1,subQ2,sQuery(id+"F1.wireOp",EDGE,"E135.MirrorCS"),sQuery(id+"F1.wireOp",EDGE,"E136.MirrorCS"),sQuery(id+"F1.wireOp",EDGE,"E137.MirrorCS"),sQuery(id+"F1.wireOp",EDGE,"E138.MirrorCS"),sQuery(id+"F1.wireOp",EDGE,"E139.MirrorCS"),sQuery(id+"F1.wireOp",EDGE,"E140.MirrorCS"),sQuery(id+"F1.wireOp",EDGE,"E141.MirrorCS"),sQuery(id+"F1.wireOp",EDGE,"E142.MirrorCS"),sQuery(id+"F1.wireOp",EDGE,"E143.MirrorCS"),sQuery(id+"F1.wireOp",EDGE,"E144.MirrorCS"),sQuery(id+"F1.wireOp",EDGE,"E145.MirrorCS"),sQuery(id+"F1.wireOp",EDGE,"E146.MirrorCS"),sQuery(id+"F1.wireOp",EDGE,"E147.MirrorCS"),sQuery(id+"F1.wireOp",EDGE,"E148.MirrorCS"),sQuery(id+"F1.wireOp",EDGE,"E149.MirrorCS"),subQ0,subQ3,sQuery(id+"F1.wireOp",EDGE,"E152.MirrorCS"),sQuery(id+"F1.wireOp",EDGE,"E153.MirrorCS"),sQuery(id+"F1.wireOp",EDGE,"E154.MirrorCS"),sQuery(id+"F1.wireOp",EDGE,"E156.MirrorCS")])],"isStart":true}),makeQuery(id+"F2.opExtrude","SWEPT_FACE",FACE,{"disambiguationData":[OSD([subQ1])]}),makeQuery(id+"F2.opExtrude","SWEPT_FACE",FACE,{"disambiguationData":[OSD([subQ2])]}),makeQuery(id+"F2.opExtrude","SWEPT_FACE",FACE,{"disambiguationData":[OSD([subQ0])]}),makeQuery(id+"F2.opExtrude","SWEPT_FACE",FACE,{"disambiguationData":[OSD([subQ3])]}),makeQuery(id+"F3.opExtrude","SWEPT_FACE",FACE,{"disambiguationData":[OSD([subQ4])]})])],"derivedFrom":makeQuery(id+"F3.opExtrude","CAP_EDGE",EDGE,{"disambiguationData":[OSD([subQ4])],"isStart":true})});}
            var Q24;
            {var subQ0=sQuery(id+"F1.wireOp",EDGE,"E133.MirrorCS");var subQ1=sQuery(id+"F1.wireOp",EDGE,"E131.MirrorCS");var subQ2=sQuery(id+"F1.wireOp",EDGE,"E130.MirrorCS");var subQ3=sQuery(id+"F1.wireOp",EDGE,"E134.MirrorCS");var subQ4=sQuery(id+"F0.wireOp",EDGE,"E0");Q24=makeQuery(id+"F3.boolean.opBoolean","SPLIT",EDGE,{"disambiguationData":[TD([makeQuery(id+"F2.opExtrude","CAP_FACE",FACE,{"disambiguationData":[OSD([sQuery(id+"F1.wireOp",EDGE,"E86"),sQuery(id+"F1.wireOp",EDGE,"E87"),sQuery(id+"F1.wireOp",EDGE,"E88"),sQuery(id+"F1.wireOp",EDGE,"E89"),sQuery(id+"F1.wireOp",EDGE,"E90"),sQuery(id+"F1.wireOp",EDGE,"E91"),sQuery(id+"F1.wireOp",EDGE,"E92"),sQuery(id+"F1.wireOp",EDGE,"E93"),sQuery(id+"F1.wireOp",EDGE,"E94"),sQuery(id+"F1.wireOp",EDGE,"E95"),sQuery(id+"F1.wireOp",EDGE,"E96"),sQuery(id+"F1.wireOp",EDGE,"E97"),sQuery(id+"F1.wireOp",EDGE,"E98"),sQuery(id+"F1.wireOp",EDGE,"E99"),sQuery(id+"F1.wireOp",EDGE,"E100.MirrorCS"),sQuery(id+"F1.wireOp",EDGE,"E101.MirrorCS"),sQuery(id+"F1.wireOp",EDGE,"E102.MirrorCS"),sQuery(id+"F1.wireOp",EDGE,"E103.MirrorCS"),sQuery(id+"F1.wireOp",EDGE,"E104.MirrorCS"),sQuery(id+"F1.wireOp",EDGE,"E105.MirrorCS"),sQuery(id+"F1.wireOp",EDGE,"E106.MirrorCS"),sQuery(id+"F1.wireOp",EDGE,"E107.MirrorCS"),sQuery(id+"F1.wireOp",EDGE,"E108.MirrorCS"),sQuery(id+"F1.wireOp",EDGE,"E109.MirrorCS"),sQuery(id+"F1.wireOp",EDGE,"E110.MirrorCS"),sQuery(id+"F1.wireOp",EDGE,"E111.MirrorCS"),sQuery(id+"F1.wireOp",EDGE,"E112.MirrorCS"),sQuery(id+"F1.wireOp",EDGE,"E113.MirrorCS"),sQuery(id+"F1.wireOp",EDGE,"E128.MirrorCS"),sQuery(id+"F1.wireOp",EDGE,"E129.MirrorCS"),subQ2,subQ1,sQuery(id+"F1.wireOp",EDGE,"E132.MirrorCS"),subQ0,subQ3,sQuery(id+"F1.wireOp",EDGE,"E135.MirrorCS"),sQuery(id+"F1.wireOp",EDGE,"E136.MirrorCS"),sQuery(id+"F1.wireOp",EDGE,"E137.MirrorCS"),sQuery(id+"F1.wireOp",EDGE,"E138.MirrorCS"),sQuery(id+"F1.wireOp",EDGE,"E139.MirrorCS"),sQuery(id+"F1.wireOp",EDGE,"E140.MirrorCS"),sQuery(id+"F1.wireOp",EDGE,"E141.MirrorCS"),sQuery(id+"F1.wireOp",EDGE,"E142.MirrorCS"),sQuery(id+"F1.wireOp",EDGE,"E143.MirrorCS"),sQuery(id+"F1.wireOp",EDGE,"E144.MirrorCS"),sQuery(id+"F1.wireOp",EDGE,"E145.MirrorCS"),sQuery(id+"F1.wireOp",EDGE,"E146.MirrorCS"),sQuery(id+"F1.wireOp",EDGE,"E147.MirrorCS"),sQuery(id+"F1.wireOp",EDGE,"E148.MirrorCS"),sQuery(id+"F1.wireOp",EDGE,"E149.MirrorCS"),sQuery(id+"F1.wireOp",EDGE,"E150.MirrorCS"),sQuery(id+"F1.wireOp",EDGE,"E151.MirrorCS"),sQuery(id+"F1.wireOp",EDGE,"E152.MirrorCS"),sQuery(id+"F1.wireOp",EDGE,"E153.MirrorCS"),sQuery(id+"F1.wireOp",EDGE,"E154.MirrorCS"),sQuery(id+"F1.wireOp",EDGE,"E156.MirrorCS")])],"isStart":true}),makeQuery(id+"F2.opExtrude","SWEPT_FACE",FACE,{"disambiguationData":[OSD([subQ2])]}),makeQuery(id+"F2.opExtrude","SWEPT_FACE",FACE,{"disambiguationData":[OSD([subQ1])]}),makeQuery(id+"F2.opExtrude","SWEPT_FACE",FACE,{"disambiguationData":[OSD([subQ0])]}),makeQuery(id+"F2.opExtrude","SWEPT_FACE",FACE,{"disambiguationData":[OSD([subQ3])]}),makeQuery(id+"F3.opExtrude","SWEPT_FACE",FACE,{"disambiguationData":[OSD([subQ4])]})])],"derivedFrom":makeQuery(id+"F3.opExtrude","CAP_EDGE",EDGE,{"disambiguationData":[OSD([subQ4])],"isStart":true})});}
            var Q25;
            {var subQ0=sQuery(id+"F1.wireOp",EDGE,"E131.MirrorCS");var subQ1=sQuery(id+"F1.wireOp",EDGE,"E130.MirrorCS");var subQ2=sQuery(id+"F1.wireOp",EDGE,"E128.MirrorCS");var subQ3=sQuery(id+"F1.wireOp",EDGE,"E148.MirrorCS");var subQ4=sQuery(id+"F0.wireOp",EDGE,"E0");Q25=makeQuery(id+"F3.boolean.opBoolean","SPLIT",EDGE,{"disambiguationData":[TD([makeQuery(id+"F2.opExtrude","CAP_FACE",FACE,{"disambiguationData":[OSD([sQuery(id+"F1.wireOp",EDGE,"E86"),sQuery(id+"F1.wireOp",EDGE,"E87"),sQuery(id+"F1.wireOp",EDGE,"E88"),sQuery(id+"F1.wireOp",EDGE,"E89"),sQuery(id+"F1.wireOp",EDGE,"E90"),sQuery(id+"F1.wireOp",EDGE,"E91"),sQuery(id+"F1.wireOp",EDGE,"E92"),sQuery(id+"F1.wireOp",EDGE,"E93"),sQuery(id+"F1.wireOp",EDGE,"E94"),sQuery(id+"F1.wireOp",EDGE,"E95"),sQuery(id+"F1.wireOp",EDGE,"E96"),sQuery(id+"F1.wireOp",EDGE,"E97"),sQuery(id+"F1.wireOp",EDGE,"E98"),sQuery(id+"F1.wireOp",EDGE,"E99"),sQuery(id+"F1.wireOp",EDGE,"E100.MirrorCS"),sQuery(id+"F1.wireOp",EDGE,"E101.MirrorCS"),sQuery(id+"F1.wireOp",EDGE,"E102.MirrorCS"),sQuery(id+"F1.wireOp",EDGE,"E103.MirrorCS"),sQuery(id+"F1.wireOp",EDGE,"E104.MirrorCS"),sQuery(id+"F1.wireOp",EDGE,"E105.MirrorCS"),sQuery(id+"F1.wireOp",EDGE,"E106.MirrorCS"),sQuery(id+"F1.wireOp",EDGE,"E107.MirrorCS"),sQuery(id+"F1.wireOp",EDGE,"E108.MirrorCS"),sQuery(id+"F1.wireOp",EDGE,"E109.MirrorCS"),sQuery(id+"F1.wireOp",EDGE,"E110.MirrorCS"),sQuery(id+"F1.wireOp",EDGE,"E111.MirrorCS"),sQuery(id+"F1.wireOp",EDGE,"E112.MirrorCS"),sQuery(id+"F1.wireOp",EDGE,"E113.MirrorCS"),subQ2,sQuery(id+"F1.wireOp",EDGE,"E129.MirrorCS"),subQ1,subQ0,sQuery(id+"F1.wireOp",EDGE,"E132.MirrorCS"),sQuery(id+"F1.wireOp",EDGE,"E133.MirrorCS"),sQuery(id+"F1.wireOp",EDGE,"E134.MirrorCS"),sQuery(id+"F1.wireOp",EDGE,"E135.MirrorCS"),sQuery(id+"F1.wireOp",EDGE,"E136.MirrorCS"),sQuery(id+"F1.wireOp",EDGE,"E137.MirrorCS"),sQuery(id+"F1.wireOp",EDGE,"E138.MirrorCS"),sQuery(id+"F1.wireOp",EDGE,"E139.MirrorCS"),sQuery(id+"F1.wireOp",EDGE,"E140.MirrorCS"),sQuery(id+"F1.wireOp",EDGE,"E141.MirrorCS"),sQuery(id+"F1.wireOp",EDGE,"E142.MirrorCS"),sQuery(id+"F1.wireOp",EDGE,"E143.MirrorCS"),sQuery(id+"F1.wireOp",EDGE,"E144.MirrorCS"),sQuery(id+"F1.wireOp",EDGE,"E145.MirrorCS"),sQuery(id+"F1.wireOp",EDGE,"E146.MirrorCS"),sQuery(id+"F1.wireOp",EDGE,"E147.MirrorCS"),subQ3,sQuery(id+"F1.wireOp",EDGE,"E149.MirrorCS"),sQuery(id+"F1.wireOp",EDGE,"E150.MirrorCS"),sQuery(id+"F1.wireOp",EDGE,"E151.MirrorCS"),sQuery(id+"F1.wireOp",EDGE,"E152.MirrorCS"),sQuery(id+"F1.wireOp",EDGE,"E153.MirrorCS"),sQuery(id+"F1.wireOp",EDGE,"E154.MirrorCS"),sQuery(id+"F1.wireOp",EDGE,"E156.MirrorCS")])],"isStart":true}),makeQuery(id+"F2.opExtrude","SWEPT_FACE",FACE,{"disambiguationData":[OSD([subQ2])]}),makeQuery(id+"F2.opExtrude","SWEPT_FACE",FACE,{"disambiguationData":[OSD([subQ1])]}),makeQuery(id+"F2.opExtrude","SWEPT_FACE",FACE,{"disambiguationData":[OSD([subQ0])]}),makeQuery(id+"F2.opExtrude","SWEPT_FACE",FACE,{"disambiguationData":[OSD([subQ3])]}),makeQuery(id+"F3.opExtrude","SWEPT_FACE",FACE,{"disambiguationData":[OSD([subQ4])]})])],"derivedFrom":makeQuery(id+"F3.opExtrude","CAP_EDGE",EDGE,{"disambiguationData":[OSD([subQ4])],"isStart":true})});}
            var Q26;
            {var subQ0=sQuery(id+"F1.wireOp",EDGE,"E128.MirrorCS");var subQ1=sQuery(id+"F1.wireOp",EDGE,"E99");var subQ2=sQuery(id+"F0.wireOp",EDGE,"E0");var subQ3=sQuery(id+"F1.wireOp",EDGE,"E98");var subQ4=sQuery(id+"F1.wireOp",EDGE,"E148.MirrorCS");Q26=makeQuery(id+"F3.boolean.opBoolean","SPLIT",EDGE,{"disambiguationData":[TD([makeQuery(id+"F2.opExtrude","CAP_FACE",FACE,{"disambiguationData":[OSD([sQuery(id+"F1.wireOp",EDGE,"E86"),sQuery(id+"F1.wireOp",EDGE,"E87"),sQuery(id+"F1.wireOp",EDGE,"E88"),sQuery(id+"F1.wireOp",EDGE,"E89"),sQuery(id+"F1.wireOp",EDGE,"E90"),sQuery(id+"F1.wireOp",EDGE,"E91"),sQuery(id+"F1.wireOp",EDGE,"E92"),sQuery(id+"F1.wireOp",EDGE,"E93"),sQuery(id+"F1.wireOp",EDGE,"E94"),sQuery(id+"F1.wireOp",EDGE,"E95"),sQuery(id+"F1.wireOp",EDGE,"E96"),sQuery(id+"F1.wireOp",EDGE,"E97"),subQ3,subQ1,sQuery(id+"F1.wireOp",EDGE,"E100.MirrorCS"),sQuery(id+"F1.wireOp",EDGE,"E101.MirrorCS"),sQuery(id+"F1.wireOp",EDGE,"E102.MirrorCS"),sQuery(id+"F1.wireOp",EDGE,"E103.MirrorCS"),sQuery(id+"F1.wireOp",EDGE,"E104.MirrorCS"),sQuery(id+"F1.wireOp",EDGE,"E105.MirrorCS"),sQuery(id+"F1.wireOp",EDGE,"E106.MirrorCS"),sQuery(id+"F1.wireOp",EDGE,"E107.MirrorCS"),sQuery(id+"F1.wireOp",EDGE,"E108.MirrorCS"),sQuery(id+"F1.wireOp",EDGE,"E109.MirrorCS"),sQuery(id+"F1.wireOp",EDGE,"E110.MirrorCS"),sQuery(id+"F1.wireOp",EDGE,"E111.MirrorCS"),sQuery(id+"F1.wireOp",EDGE,"E112.MirrorCS"),sQuery(id+"F1.wireOp",EDGE,"E113.MirrorCS"),subQ0,sQuery(id+"F1.wireOp",EDGE,"E129.MirrorCS"),sQuery(id+"F1.wireOp",EDGE,"E130.MirrorCS"),sQuery(id+"F1.wireOp",EDGE,"E131.MirrorCS"),sQuery(id+"F1.wireOp",EDGE,"E132.MirrorCS"),sQuery(id+"F1.wireOp",EDGE,"E133.MirrorCS"),sQuery(id+"F1.wireOp",EDGE,"E134.MirrorCS"),sQuery(id+"F1.wireOp",EDGE,"E135.MirrorCS"),sQuery(id+"F1.wireOp",EDGE,"E136.MirrorCS"),sQuery(id+"F1.wireOp",EDGE,"E137.MirrorCS"),sQuery(id+"F1.wireOp",EDGE,"E138.MirrorCS"),sQuery(id+"F1.wireOp",EDGE,"E139.MirrorCS"),sQuery(id+"F1.wireOp",EDGE,"E140.MirrorCS"),sQuery(id+"F1.wireOp",EDGE,"E141.MirrorCS"),sQuery(id+"F1.wireOp",EDGE,"E142.MirrorCS"),sQuery(id+"F1.wireOp",EDGE,"E143.MirrorCS"),sQuery(id+"F1.wireOp",EDGE,"E144.MirrorCS"),sQuery(id+"F1.wireOp",EDGE,"E145.MirrorCS"),sQuery(id+"F1.wireOp",EDGE,"E146.MirrorCS"),sQuery(id+"F1.wireOp",EDGE,"E147.MirrorCS"),subQ4,sQuery(id+"F1.wireOp",EDGE,"E149.MirrorCS"),sQuery(id+"F1.wireOp",EDGE,"E150.MirrorCS"),sQuery(id+"F1.wireOp",EDGE,"E151.MirrorCS"),sQuery(id+"F1.wireOp",EDGE,"E152.MirrorCS"),sQuery(id+"F1.wireOp",EDGE,"E153.MirrorCS"),sQuery(id+"F1.wireOp",EDGE,"E154.MirrorCS"),sQuery(id+"F1.wireOp",EDGE,"E156.MirrorCS")])],"isStart":true}),makeQuery(id+"F2.opExtrude","SWEPT_FACE",FACE,{"disambiguationData":[OSD([subQ3])]}),makeQuery(id+"F2.opExtrude","SWEPT_FACE",FACE,{"disambiguationData":[OSD([subQ1])]}),makeQuery(id+"F2.opExtrude","SWEPT_FACE",FACE,{"disambiguationData":[OSD([subQ0])]}),makeQuery(id+"F2.opExtrude","SWEPT_FACE",FACE,{"disambiguationData":[OSD([subQ4])]}),makeQuery(id+"F3.opExtrude","SWEPT_FACE",FACE,{"disambiguationData":[OSD([subQ2])]})])],"derivedFrom":makeQuery(id+"F3.opExtrude","CAP_EDGE",EDGE,{"disambiguationData":[OSD([subQ2])],"isStart":true})});}
            var Q27;
            {var subQ0=sQuery(id+"F1.wireOp",EDGE,"E98");var subQ1=sQuery(id+"F1.wireOp",EDGE,"E97");var subQ2=sQuery(id+"F1.wireOp",EDGE,"E96");var subQ3=sQuery(id+"F1.wireOp",EDGE,"E99");var subQ4=sQuery(id+"F0.wireOp",EDGE,"E0");Q27=makeQuery(id+"F3.boolean.opBoolean","SPLIT",EDGE,{"disambiguationData":[TD([makeQuery(id+"F2.opExtrude","CAP_FACE",FACE,{"disambiguationData":[OSD([sQuery(id+"F1.wireOp",EDGE,"E86"),sQuery(id+"F1.wireOp",EDGE,"E87"),sQuery(id+"F1.wireOp",EDGE,"E88"),sQuery(id+"F1.wireOp",EDGE,"E89"),sQuery(id+"F1.wireOp",EDGE,"E90"),sQuery(id+"F1.wireOp",EDGE,"E91"),sQuery(id+"F1.wireOp",EDGE,"E92"),sQuery(id+"F1.wireOp",EDGE,"E93"),sQuery(id+"F1.wireOp",EDGE,"E94"),sQuery(id+"F1.wireOp",EDGE,"E95"),subQ2,subQ1,subQ0,subQ3,sQuery(id+"F1.wireOp",EDGE,"E100.MirrorCS"),sQuery(id+"F1.wireOp",EDGE,"E101.MirrorCS"),sQuery(id+"F1.wireOp",EDGE,"E102.MirrorCS"),sQuery(id+"F1.wireOp",EDGE,"E103.MirrorCS"),sQuery(id+"F1.wireOp",EDGE,"E104.MirrorCS"),sQuery(id+"F1.wireOp",EDGE,"E105.MirrorCS"),sQuery(id+"F1.wireOp",EDGE,"E106.MirrorCS"),sQuery(id+"F1.wireOp",EDGE,"E107.MirrorCS"),sQuery(id+"F1.wireOp",EDGE,"E108.MirrorCS"),sQuery(id+"F1.wireOp",EDGE,"E109.MirrorCS"),sQuery(id+"F1.wireOp",EDGE,"E110.MirrorCS"),sQuery(id+"F1.wireOp",EDGE,"E111.MirrorCS"),sQuery(id+"F1.wireOp",EDGE,"E112.MirrorCS"),sQuery(id+"F1.wireOp",EDGE,"E113.MirrorCS"),sQuery(id+"F1.wireOp",EDGE,"E128.MirrorCS"),sQuery(id+"F1.wireOp",EDGE,"E129.MirrorCS"),sQuery(id+"F1.wireOp",EDGE,"E130.MirrorCS"),sQuery(id+"F1.wireOp",EDGE,"E131.MirrorCS"),sQuery(id+"F1.wireOp",EDGE,"E132.MirrorCS"),sQuery(id+"F1.wireOp",EDGE,"E133.MirrorCS"),sQuery(id+"F1.wireOp",EDGE,"E134.MirrorCS"),sQuery(id+"F1.wireOp",EDGE,"E135.MirrorCS"),sQuery(id+"F1.wireOp",EDGE,"E136.MirrorCS"),sQuery(id+"F1.wireOp",EDGE,"E137.MirrorCS"),sQuery(id+"F1.wireOp",EDGE,"E138.MirrorCS"),sQuery(id+"F1.wireOp",EDGE,"E139.MirrorCS"),sQuery(id+"F1.wireOp",EDGE,"E140.MirrorCS"),sQuery(id+"F1.wireOp",EDGE,"E141.MirrorCS"),sQuery(id+"F1.wireOp",EDGE,"E142.MirrorCS"),sQuery(id+"F1.wireOp",EDGE,"E143.MirrorCS"),sQuery(id+"F1.wireOp",EDGE,"E144.MirrorCS"),sQuery(id+"F1.wireOp",EDGE,"E145.MirrorCS"),sQuery(id+"F1.wireOp",EDGE,"E146.MirrorCS"),sQuery(id+"F1.wireOp",EDGE,"E147.MirrorCS"),sQuery(id+"F1.wireOp",EDGE,"E148.MirrorCS"),sQuery(id+"F1.wireOp",EDGE,"E149.MirrorCS"),sQuery(id+"F1.wireOp",EDGE,"E150.MirrorCS"),sQuery(id+"F1.wireOp",EDGE,"E151.MirrorCS"),sQuery(id+"F1.wireOp",EDGE,"E152.MirrorCS"),sQuery(id+"F1.wireOp",EDGE,"E153.MirrorCS"),sQuery(id+"F1.wireOp",EDGE,"E154.MirrorCS"),sQuery(id+"F1.wireOp",EDGE,"E156.MirrorCS")])],"isStart":true}),makeQuery(id+"F2.opExtrude","SWEPT_FACE",FACE,{"disambiguationData":[OSD([subQ2])]}),makeQuery(id+"F2.opExtrude","SWEPT_FACE",FACE,{"disambiguationData":[OSD([subQ1])]}),makeQuery(id+"F2.opExtrude","SWEPT_FACE",FACE,{"disambiguationData":[OSD([subQ0])]}),makeQuery(id+"F2.opExtrude","SWEPT_FACE",FACE,{"disambiguationData":[OSD([subQ3])]}),makeQuery(id+"F3.opExtrude","SWEPT_FACE",FACE,{"disambiguationData":[OSD([subQ4])]})])],"derivedFrom":makeQuery(id+"F3.opExtrude","CAP_EDGE",EDGE,{"disambiguationData":[OSD([subQ4])],"isStart":true})});}
            var Q28;
            Q28=makeQuery(id+"F14.opExtrude","CAP_EDGE",EDGE,{"disambiguationData":[OSD([sQuery(id+"F1.wireOp",EDGE,"E98")])],"isStart":false});
            var Q29;
            Q29=makeQuery(id+"F14.opExtrude","CAP_EDGE",EDGE,{"disambiguationData":[OSD([sQuery(id+"F1.wireOp",EDGE,"E97")])],"isStart":false});
            var Q30;
            Q30=makeQuery(id+"F14.opExtrude","CAP_EDGE",EDGE,{"disambiguationData":[OSD([sQuery(id+"F1.wireOp",EDGE,"E96")])],"isStart":false});
            var Q31;
            Q31=makeQuery(id+"F14.opExtrude","CAP_EDGE",EDGE,{"disambiguationData":[OSD([sQuery(id+"F1.wireOp",EDGE,"E95")])],"isStart":false});
            var Q32;
            Q32=makeQuery(id+"F14.opExtrude","CAP_EDGE",EDGE,{"disambiguationData":[OSD([sQuery(id+"F1.wireOp",EDGE,"E94")])],"isStart":false});
            var Q33;
            Q33=makeQuery(id+"F14.opExtrude","CAP_EDGE",EDGE,{"disambiguationData":[OSD([sQuery(id+"F1.wireOp",EDGE,"E93")])],"isStart":false});
            var Q34;
            Q34=makeQuery(id+"F14.opExtrude","CAP_EDGE",EDGE,{"disambiguationData":[OSD([sQuery(id+"F1.wireOp",EDGE,"E92")])],"isStart":false});
            var Q35;
            Q35=makeQuery(id+"F14.opExtrude","CAP_EDGE",EDGE,{"disambiguationData":[OSD([sQuery(id+"F1.wireOp",EDGE,"E91")])],"isStart":false});
            var Q36;
            Q36=makeQuery(id+"F14.opExtrude","CAP_EDGE",EDGE,{"disambiguationData":[OSD([sQuery(id+"F1.wireOp",EDGE,"E90")])],"isStart":false});
            var Q37;
            Q37=makeQuery(id+"F14.opExtrude","CAP_EDGE",EDGE,{"disambiguationData":[OSD([sQuery(id+"F1.wireOp",EDGE,"E89")])],"isStart":false});
            var Q38;
            Q38=makeQuery(id+"F14.opExtrude","CAP_EDGE",EDGE,{"disambiguationData":[OSD([sQuery(id+"F1.wireOp",EDGE,"E88")])],"isStart":false});
            var Q39;
            Q39=makeQuery(id+"F14.opExtrude","CAP_EDGE",EDGE,{"disambiguationData":[OSD([sQuery(id+"F1.wireOp",EDGE,"E87")])],"isStart":false});
            var Q40;
            Q40=makeQuery(id+"F14.opExtrude","CAP_EDGE",EDGE,{"disambiguationData":[OSD([sQuery(id+"F1.wireOp",EDGE,"E86")])],"isStart":false});
            var Q41;
            Q41=makeQuery(id+"F14.opExtrude","CAP_EDGE",EDGE,{"disambiguationData":[OSD([sQuery(id+"F1.wireOp",EDGE,"E108.MirrorCS")])],"isStart":false});
            var Q42;
            Q42=makeQuery(id+"F14.opExtrude","CAP_EDGE",EDGE,{"disambiguationData":[OSD([sQuery(id+"F1.wireOp",EDGE,"E100.MirrorCS")])],"isStart":false});
            var Q43;
            Q43=makeQuery(id+"F14.opExtrude","CAP_EDGE",EDGE,{"disambiguationData":[OSD([sQuery(id+"F1.wireOp",EDGE,"E102.MirrorCS")])],"isStart":false});
            var Q44;
            Q44=makeQuery(id+"F14.opExtrude","CAP_EDGE",EDGE,{"disambiguationData":[OSD([sQuery(id+"F1.wireOp",EDGE,"E105.MirrorCS")])],"isStart":false});
            var Q45;
            Q45=makeQuery(id+"F14.opExtrude","CAP_EDGE",EDGE,{"disambiguationData":[OSD([sQuery(id+"F1.wireOp",EDGE,"E106.MirrorCS")])],"isStart":false});
            var Q46;
            Q46=makeQuery(id+"F14.opExtrude","CAP_EDGE",EDGE,{"disambiguationData":[OSD([sQuery(id+"F1.wireOp",EDGE,"E112.MirrorCS")])],"isStart":false});
            var Q47;
            Q47=makeQuery(id+"F14.opExtrude","CAP_EDGE",EDGE,{"disambiguationData":[OSD([sQuery(id+"F1.wireOp",EDGE,"E101.MirrorCS")])],"isStart":false});
            var Q48;
            Q48=makeQuery(id+"F14.opExtrude","CAP_EDGE",EDGE,{"disambiguationData":[OSD([sQuery(id+"F1.wireOp",EDGE,"E111.MirrorCS")])],"isStart":false});
            var Q49;
            Q49=makeQuery(id+"F14.opExtrude","CAP_EDGE",EDGE,{"disambiguationData":[OSD([sQuery(id+"F1.wireOp",EDGE,"E110.MirrorCS")])],"isStart":false});
            var Q50;
            Q50=makeQuery(id+"F14.opExtrude","CAP_EDGE",EDGE,{"disambiguationData":[OSD([sQuery(id+"F1.wireOp",EDGE,"E104.MirrorCS")])],"isStart":false});
            var Q51;
            Q51=makeQuery(id+"F14.opExtrude","CAP_EDGE",EDGE,{"disambiguationData":[OSD([sQuery(id+"F1.wireOp",EDGE,"E113.MirrorCS")])],"isStart":false});
            var Q52;
            Q52=makeQuery(id+"F14.opExtrude","CAP_FACE",FACE,{"disambiguationData":[OSD([sQuery(id+"F1.wireOp",EDGE,"E86"),sQuery(id+"F1.wireOp",EDGE,"E87"),sQuery(id+"F1.wireOp",EDGE,"E88"),sQuery(id+"F1.wireOp",EDGE,"E89"),sQuery(id+"F1.wireOp",EDGE,"E90"),sQuery(id+"F1.wireOp",EDGE,"E91"),sQuery(id+"F1.wireOp",EDGE,"E92"),sQuery(id+"F1.wireOp",EDGE,"E93"),sQuery(id+"F1.wireOp",EDGE,"E94"),sQuery(id+"F1.wireOp",EDGE,"E95"),sQuery(id+"F1.wireOp",EDGE,"E96"),sQuery(id+"F1.wireOp",EDGE,"E97"),sQuery(id+"F1.wireOp",EDGE,"E98"),sQuery(id+"F1.wireOp",EDGE,"E99"),sQuery(id+"F1.wireOp",EDGE,"E100.MirrorCS"),sQuery(id+"F1.wireOp",EDGE,"E101.MirrorCS"),sQuery(id+"F1.wireOp",EDGE,"E102.MirrorCS"),sQuery(id+"F1.wireOp",EDGE,"E103.MirrorCS"),sQuery(id+"F1.wireOp",EDGE,"E104.MirrorCS"),sQuery(id+"F1.wireOp",EDGE,"E105.MirrorCS"),sQuery(id+"F1.wireOp",EDGE,"E106.MirrorCS"),sQuery(id+"F1.wireOp",EDGE,"E107.MirrorCS"),sQuery(id+"F1.wireOp",EDGE,"E108.MirrorCS"),sQuery(id+"F1.wireOp",EDGE,"E109.MirrorCS"),sQuery(id+"F1.wireOp",EDGE,"E110.MirrorCS"),sQuery(id+"F1.wireOp",EDGE,"E111.MirrorCS"),sQuery(id+"F1.wireOp",EDGE,"E112.MirrorCS"),sQuery(id+"F1.wireOp",EDGE,"E113.MirrorCS"),sQuery(id+"F1.wireOp",EDGE,"E128.MirrorCS"),sQuery(id+"F1.wireOp",EDGE,"E129.MirrorCS"),sQuery(id+"F1.wireOp",EDGE,"E130.MirrorCS"),sQuery(id+"F1.wireOp",EDGE,"E131.MirrorCS"),sQuery(id+"F1.wireOp",EDGE,"E132.MirrorCS"),sQuery(id+"F1.wireOp",EDGE,"E133.MirrorCS"),sQuery(id+"F1.wireOp",EDGE,"E134.MirrorCS"),sQuery(id+"F1.wireOp",EDGE,"E135.MirrorCS"),sQuery(id+"F1.wireOp",EDGE,"E136.MirrorCS"),sQuery(id+"F1.wireOp",EDGE,"E137.MirrorCS"),sQuery(id+"F1.wireOp",EDGE,"E138.MirrorCS"),sQuery(id+"F1.wireOp",EDGE,"E139.MirrorCS"),sQuery(id+"F1.wireOp",EDGE,"E140.MirrorCS"),sQuery(id+"F1.wireOp",EDGE,"E141.MirrorCS"),sQuery(id+"F1.wireOp",EDGE,"E142.MirrorCS"),sQuery(id+"F1.wireOp",EDGE,"E143.MirrorCS"),sQuery(id+"F1.wireOp",EDGE,"E144.MirrorCS"),sQuery(id+"F1.wireOp",EDGE,"E145.MirrorCS"),sQuery(id+"F1.wireOp",EDGE,"E146.MirrorCS"),sQuery(id+"F1.wireOp",EDGE,"E147.MirrorCS"),sQuery(id+"F1.wireOp",EDGE,"E148.MirrorCS"),sQuery(id+"F1.wireOp",EDGE,"E149.MirrorCS"),sQuery(id+"F1.wireOp",EDGE,"E150.MirrorCS"),sQuery(id+"F1.wireOp",EDGE,"E151.MirrorCS"),sQuery(id+"F1.wireOp",EDGE,"E152.MirrorCS"),sQuery(id+"F1.wireOp",EDGE,"E153.MirrorCS"),sQuery(id+"F1.wireOp",EDGE,"E154.MirrorCS"),sQuery(id+"F1.wireOp",EDGE,"E156.MirrorCS"),sQuery(id+"F6.wireOp",EDGE,"E184")])],"isStart":false});
            var Q53;
            Q53=makeQuery(id+"F14.opExtrude","CAP_EDGE",EDGE,{"disambiguationData":[OSD([sQuery(id+"F1.wireOp",EDGE,"E103.MirrorCS")])],"isStart":false});
            fillet(context, id + "F15", {"entities" : qUnion([Q0, Q1, Q2, Q3, Q4, Q5, Q6, Q7, Q8, Q9, Q10, Q11, Q12, Q13, Q14, Q15, Q16, Q17, Q18, Q19, Q20, Q21, Q22, Q23, Q24, Q25, Q26, Q27, Q28, Q29, Q30, Q31, Q32, Q33, Q34, Q35, Q36, Q37, Q38, Q39, Q40, Q41, Q42, Q43, Q44, Q45, Q46, Q47, Q48, Q49, Q50, Q51, Q52, Q53]), "radius" : 5 * mm, "tangentPropagation" : true, "allowEdgeOverflow" : false});
        }
        {
            var Q0;
            {var subQ1=sQuery(id+"F12.wireOp",EDGE,"E205");var subQ3=sQuery(id+"F12.wireOp",EDGE,"E221");var subQ4=makeQuery(id+"F12.imprint","INTERSECT",VERTEX,{"derivedFrom":[subQ1,sQuery(id+"F12.wireOp",EDGE,"E219"),subQ3]});Q0=makeQuery(id+"F12.imprint","IMPRINT",FACE,{"disambiguationData":[TD([[makeQuery(id+"F12.imprint","IMPRINT",EDGE,{"disambiguationData":[TD([[subQ4,1.0]])],"derivedFrom":subQ3}),1.0]])]});}
            var Q1;
            {var subQ0=sQuery(id+"F12.wireOp",EDGE,"E205");var subQ3=sQuery(id+"F12.wireOp",EDGE,"E221");var subQ5=makeQuery(id+"F12.imprint","INTERSECT",VERTEX,{"derivedFrom":[subQ0,sQuery(id+"F12.wireOp",EDGE,"E219"),subQ3]});Q1=makeQuery(id+"F12.imprint","IMPRINT",FACE,{"disambiguationData":[TD([[makeQuery(id+"F12.imprint","IMPRINT",EDGE,{"disambiguationData":[TD([[subQ5,1.0]])],"derivedFrom":subQ0}),1.0]])]});}
            var Q2;
            {var subQ0=sQuery(id+"F12.wireOp",EDGE,"E204");var subQ3=sQuery(id+"F12.wireOp",EDGE,"E221");var subQ5=makeQuery(id+"F12.imprint","INTERSECT",VERTEX,{"derivedFrom":[subQ0,sQuery(id+"F12.wireOp",EDGE,"E217"),subQ3]});Q2=makeQuery(id+"F12.imprint","IMPRINT",FACE,{"disambiguationData":[TD([[makeQuery(id+"F12.imprint","IMPRINT",EDGE,{"disambiguationData":[TD([[subQ5,1.0]])],"derivedFrom":subQ0}),-1.0]])]});}
            var Q3;
            {var subQ1=sQuery(id+"F12.wireOp",EDGE,"E204");var subQ3=sQuery(id+"F12.wireOp",EDGE,"E221");var subQ4=makeQuery(id+"F12.imprint","INTERSECT",VERTEX,{"derivedFrom":[subQ1,sQuery(id+"F12.wireOp",EDGE,"E217"),subQ3]});Q3=makeQuery(id+"F12.imprint","IMPRINT",FACE,{"disambiguationData":[TD([[makeQuery(id+"F12.imprint","IMPRINT",EDGE,{"disambiguationData":[TD([[subQ4,-1.0]])],"derivedFrom":subQ3}),1.0]])]});}
            var Q4;
            Q4=sQuery(id+"F12.wireOp",EDGE,"E221");
            extrude(context, id + "F16", {"entities" : qUnion([Q0, Q1, Q2, Q3]), "operationType" : NewBodyOperationType.REMOVE, "surfaceEntities" : qUnion([Q4]), "oppositeDirection" : true, "depth" : 26.6 * mm, "offsetDistance" : 25 * mm});
        }
        {
            var Q0;
            Q0=qCreatedBy(makeId("Front.planeOp"),FACE);
            var sketch = newSketch(context, id + "F17", { "sketchPlane" : qUnion([Q0])});
            skCircle(sketch, "E228", {"center": v(0, 0) * mm, "radius": 7.5 * mm});
            skPoint(sketch, "E229.0", {"position": v(-53.62, 12.24) * mm});
            skPoint(sketch, "E230.0", {"position": v(-53.62, -12.24) * mm});
            skPoint(sketch, "E231.0", {"position": v(53.62, 12.24) * mm});
            skPoint(sketch, "E232.0", {"position": v(53.62, -12.24) * mm});
            skLineSegment(sketch, "E233", {"start": v(0, 0) * mm, "end": v(-53.62, 12.24) * mm});
            skLineSegment(sketch, "E234", {"start": v(-53.62, 12.24) * mm, "end": v(-53.62, -12.24) * mm});
            skLineSegment(sketch, "E235", {"start": v(-53.62, -12.24) * mm, "end": v(0, 0) * mm});
            skLineSegment(sketch, "E236", {"start": v(0, 0) * mm, "end": v(53.62, -12.24) * mm});
            skLineSegment(sketch, "E237", {"start": v(0, 0) * mm, "end": v(53.62, 12.24) * mm});
            skLineSegment(sketch, "E238", {"start": v(53.62, 12.24) * mm, "end": v(53.62, -12.24) * mm});
            skCircle(sketch, "E239", {"center": v(0, 0) * mm, "radius": 10 * mm});
            skSolve(sketch);
        }
        {
            var Q0;
            Q0=qSketchRegion(id+"F17",true);
            extrude(context, id + "F18", {"entities" : qUnion([Q0]), "depth" : 36.5 * mm, "offsetDistance" : 25 * mm, "hasSecondDirection" : true, "secondDirectionOppositeDirection" : true, "secondDirectionDepth" : 6 * mm});
        }
        {
            var Q0;
            Q0=makeQuery(id+"F18.opExtrude","CAP_FACE",FACE,{"disambiguationData":[OSD([sQuery(id+"F17.wireOp",EDGE,"E228"),sQuery(id+"F17.wireOp",EDGE,"E233"),sQuery(id+"F17.wireOp",EDGE,"E234"),sQuery(id+"F17.wireOp",EDGE,"E235"),sQuery(id+"F17.wireOp",EDGE,"E236"),sQuery(id+"F17.wireOp",EDGE,"E237"),sQuery(id+"F17.wireOp",EDGE,"E238"),sQuery(id+"F17.wireOp",EDGE,"E239")])],"isStart":true});
            var sketch = newSketch(context, id + "F19", { "sketchPlane" : qUnion([Q0])});
            skCircle(sketch, "E240", {"center": v(0, 0) * mm, "radius": 50 * mm});
            skFitSpline(sketch, "E241.0", {"points": [v(55, 0) * mm, v(54.42, -0.61) * mm, v(53.7, -1.36) * mm, v(52.88, -2.24) * mm, v(52.46, -2.67) * mm, v(52.06, -3.1) * mm, v(51.67, -3.5) * mm, v(51.3, -3.9) * mm, v(50.82, -4.4) * mm, v(50.4, -4.85) * mm, v(50.05, -5.21) * mm, v(49.85, -5.43) * mm, v(49.72, -5.57) * mm, v(49.69, -5.6) * mm, v(49.69, -5.6) * mm]});
            skFitSpline(sketch, "E242.0", {"points": [v(53.62, 12.24) * mm, v(53.2, 11.51) * mm, v(52.66, 10.63) * mm, v(52.05, 9.59) * mm, v(51.74, 9.07) * mm, v(51.45, 8.57) * mm, v(51.16, 8.08) * mm, v(50.88, 7.62) * mm, v(50.53, 7.02) * mm, v(50.21, 6.5) * mm, v(49.96, 6.06) * mm, v(49.8, 5.8) * mm, v(49.7, 5.64) * mm, v(49.69, 5.6) * mm, v(49.69, 5.6) * mm]});
            skFitSpline(sketch, "E243.0", {"points": [v(-53.62, -12.24) * mm, v(-53.2, -11.51) * mm, v(-52.66, -10.63) * mm, v(-52.05, -9.59) * mm, v(-51.74, -9.07) * mm, v(-51.45, -8.57) * mm, v(-51.16, -8.08) * mm, v(-50.88, -7.62) * mm, v(-50.53, -7.02) * mm, v(-50.21, -6.5) * mm, v(-49.96, -6.06) * mm, v(-49.8, -5.8) * mm, v(-49.7, -5.64) * mm, v(-49.69, -5.6) * mm, v(-49.69, -5.6) * mm]});
            skFitSpline(sketch, "E244.0", {"points": [v(-55, 0) * mm, v(-54.42, 0.61) * mm, v(-53.7, 1.36) * mm, v(-52.88, 2.24) * mm, v(-52.46, 2.67) * mm, v(-52.06, 3.1) * mm, v(-51.67, 3.5) * mm, v(-51.3, 3.9) * mm, v(-50.82, 4.4) * mm, v(-50.4, 4.85) * mm, v(-50.05, 5.21) * mm, v(-49.85, 5.43) * mm, v(-49.72, 5.57) * mm, v(-49.69, 5.6) * mm, v(-49.69, 5.6) * mm]});
            skLineSegment(sketch, "E245", {"start": v(53.62, -12.24) * mm, "end": v(49.69, -5.6) * mm});
            skLineSegment(sketch, "E246", {"start": v(55, 0) * mm, "end": v(49.69, 5.6) * mm});
            skLineSegment(sketch, "E247", {"start": v(-49.69, -5.6) * mm, "end": v(-55, 0) * mm});
            skLineSegment(sketch, "E248", {"start": v(-49.69, 5.6) * mm, "end": v(-53.62, 12.24) * mm});
            skLineSegment(sketch, "E249", {"start": v(-53.62, 12.24) * mm, "end": v(-47.4, 15.93) * mm});
            skLineSegment(sketch, "E250", {"start": v(-53.62, 12.24) * mm, "end": v(0, 0) * mm});
            skLineSegment(sketch, "E251", {"start": v(-53.62, -12.24) * mm, "end": v(0, 0) * mm});
            skLineSegment(sketch, "E252", {"start": v(0, 0) * mm, "end": v(53.62, -12.24) * mm});
            skLineSegment(sketch, "E253", {"start": v(0, 0) * mm, "end": v(53.62, 12.24) * mm});
            skCircle(sketch, "E254", {"center": v(0, 0) * mm, "radius": 25 * mm});
            skLineSegment(sketch, "E255", {"start": v(0, 0) * mm, "end": v(-11.13, 48.75) * mm});
            skLineSegment(sketch, "E256", {"start": v(0, 0) * mm, "end": v(11.13, 48.75) * mm});
            skLineSegment(sketch, "E257", {"start": v(0, 0) * mm, "end": v(11.13, -48.75) * mm});
            skLineSegment(sketch, "E258", {"start": v(0, 0) * mm, "end": v(-11.13, -48.75) * mm});
            skSolve(sketch);
        }
        {
            var Q0;
            {var subQ0=sQuery(id+"F19.wireOp",EDGE,"E240");var subQ5=sQuery(id+"F19.wireOp",EDGE,"E250");var subQ6=makeQuery(id+"F19.imprint","INTERSECT",VERTEX,{"derivedFrom":[subQ0,subQ5]});Q0=makeQuery(id+"F19.imprint","IMPRINT",FACE,{"disambiguationData":[TD([[makeQuery(id+"F19.imprint","IMPRINT",EDGE,{"disambiguationData":[TD([[subQ6,1.0]])],"derivedFrom":subQ5}),1.0]])]});}
            var Q1;
            {var subQ5=sQuery(id+"F19.wireOp",EDGE,"E250");var subQ8=sQuery(id+"F19.wireOp",EDGE,"E254");var subQ10=makeQuery(id+"F19.imprint","INTERSECT",VERTEX,{"derivedFrom":[subQ5,subQ8]});Q1=makeQuery(id+"F19.imprint","IMPRINT",FACE,{"disambiguationData":[TD([[makeQuery(id+"F19.imprint","IMPRINT",EDGE,{"disambiguationData":[TD([[subQ10,-1.0]])],"derivedFrom":subQ8}),1.0]])]});}
            var Q2;
            {var subQ0=sQuery(id+"F19.wireOp",EDGE,"E252");var subQ1=sQuery(id+"F19.wireOp",EDGE,"E240");var subQ2=makeQuery(id+"F19.imprint","INTERSECT",VERTEX,{"derivedFrom":[subQ1,subQ0]});Q2=makeQuery(id+"F19.imprint","IMPRINT",FACE,{"disambiguationData":[TD([[makeQuery(id+"F19.imprint","IMPRINT",EDGE,{"disambiguationData":[TD([[subQ2,-1.0]])],"derivedFrom":subQ0}),-1.0]])]});}
            var Q3;
            {var subQ0=sQuery(id+"F19.wireOp",EDGE,"E248");Q3=makeQuery(id+"F19.imprint","IMPRINT",FACE,{"disambiguationData":[TD([[makeQuery(id+"F19.imprint","IMPRINT",EDGE,{"derivedFrom":subQ0}),-1.0]])]});}
            var Q4;
            {var subQ3=sQuery(id+"F19.wireOp",EDGE,"E244.0");var subQ5=makeQuery(id+"F18.opExtrude","CAP_EDGE",EDGE,{"disambiguationData":[OSD([sQuery(id+"F17.wireOp",EDGE,"E238")])],"isStart":true});var subQ6=makeQuery(id+"F19.imprint","INTERSECT",VERTEX,{"derivedFrom":[subQ5,subQ3]});Q4=makeQuery(id+"F19.imprint","IMPRINT",FACE,{"disambiguationData":[TD([[makeQuery(id+"F19.imprint","IMPRINT",EDGE,{"disambiguationData":[TD([[subQ6,-1.0]])],"derivedFrom":subQ5}),1.0]])]});}
            var Q5;
            {var subQ0=sQuery(id+"F19.wireOp",EDGE,"E243.0");Q5=makeQuery(id+"F19.imprint","IMPRINT",FACE,{"disambiguationData":[TD([[makeQuery(id+"F19.imprint","IMPRINT",EDGE,{"derivedFrom":subQ0}),-1.0]])]});}
            var Q6;
            {var subQ0=sQuery(id+"F19.wireOp",EDGE,"E242.0");Q6=makeQuery(id+"F19.imprint","IMPRINT",FACE,{"disambiguationData":[TD([[makeQuery(id+"F19.imprint","IMPRINT",EDGE,{"derivedFrom":subQ0}),-1.0]])]});}
            var Q7;
            {var subQ0=sQuery(id+"F19.wireOp",EDGE,"E241.0");var subQ5=makeQuery(id+"F18.opExtrude","CAP_EDGE",EDGE,{"disambiguationData":[OSD([sQuery(id+"F17.wireOp",EDGE,"E234")])],"isStart":true});var subQ6=makeQuery(id+"F19.imprint","INTERSECT",VERTEX,{"derivedFrom":[subQ5,subQ0]});Q7=makeQuery(id+"F19.imprint","IMPRINT",FACE,{"disambiguationData":[TD([[makeQuery(id+"F19.imprint","IMPRINT",EDGE,{"disambiguationData":[TD([[subQ6,1.0]])],"derivedFrom":subQ5}),-1.0]])]});}
            var Q8;
            {var subQ0=sQuery(id+"F19.wireOp",EDGE,"E245");Q8=makeQuery(id+"F19.imprint","IMPRINT",FACE,{"disambiguationData":[TD([[makeQuery(id+"F19.imprint","IMPRINT",EDGE,{"derivedFrom":subQ0}),1.0]])]});}
            var Q9;
            {var subQ3=sQuery(id+"F19.wireOp",EDGE,"E254");var subQ7=sQuery(id+"F19.wireOp",EDGE,"E252");var subQ9=makeQuery(id+"F19.imprint","INTERSECT",VERTEX,{"derivedFrom":[subQ7,subQ3]});Q9=makeQuery(id+"F19.imprint","IMPRINT",FACE,{"disambiguationData":[TD([[makeQuery(id+"F19.imprint","IMPRINT",EDGE,{"disambiguationData":[TD([[subQ9,-1.0]])],"derivedFrom":subQ3}),1.0]])]});}
            var Q10;
            {var subQ0=sQuery(id+"F19.wireOp",EDGE,"E257");var subQ1=makeQuery(id+"F18.opExtrude","CAP_EDGE",EDGE,{"disambiguationData":[OSD([sQuery(id+"F17.wireOp",EDGE,"E228")])],"isStart":true});var subQ2=makeQuery(id+"F19.imprint","INTERSECT",VERTEX,{"derivedFrom":[subQ1,subQ0]});Q10=makeQuery(id+"F19.imprint","IMPRINT",FACE,{"disambiguationData":[TD([[makeQuery(id+"F19.imprint","IMPRINT",EDGE,{"disambiguationData":[TD([[subQ2,-1.0]])],"derivedFrom":subQ1}),1.0]])]});}
            var Q11;
            {var subQ0=sQuery(id+"F19.wireOp",EDGE,"E255");var subQ1=makeQuery(id+"F18.opExtrude","CAP_EDGE",EDGE,{"disambiguationData":[OSD([sQuery(id+"F17.wireOp",EDGE,"E228")])],"isStart":true});var subQ2=makeQuery(id+"F19.imprint","INTERSECT",VERTEX,{"derivedFrom":[subQ1,subQ0]});Q11=makeQuery(id+"F19.imprint","IMPRINT",FACE,{"disambiguationData":[TD([[makeQuery(id+"F19.imprint","IMPRINT",EDGE,{"disambiguationData":[TD([[subQ2,-1.0]])],"derivedFrom":subQ1}),1.0]])]});}
            extrude(context, id + "F20", {"entities" : qUnion([Q0, Q1, Q2, Q3, Q4, Q5, Q6, Q7, Q8, Q9, Q10, Q11]), "operationType" : NewBodyOperationType.REMOVE, "oppositeDirection" : true, "depth" : 42 * mm, "offsetDistance" : 25 * mm});
        }
        {
            var Q0;
            {var subQ0=sQuery(id+"F17.wireOp",EDGE,"E228");var subQ1=sQuery(id+"F17.wireOp",EDGE,"E239");var subQ2=sQuery(id+"F17.wireOp",EDGE,"E233");var subQ3=sQuery(id+"F17.wireOp",EDGE,"E237");Q0=makeQuery(id+"F20.boolean.opBoolean","SPLIT",FACE,{"disambiguationData":[TD([makeQuery(id+"F20.opExtrude","SWEPT_FACE",FACE,{"disambiguationData":[OSD([sQuery(id+"F19.wireOp",EDGE,"E250")])]})])],"derivedFrom":makeQuery(id+"F18.opExtrude","CAP_FACE",FACE,{"disambiguationData":[OSD([subQ0,subQ2,sQuery(id+"F17.wireOp",EDGE,"E234"),sQuery(id+"F17.wireOp",EDGE,"E235"),sQuery(id+"F17.wireOp",EDGE,"E236"),subQ3,sQuery(id+"F17.wireOp",EDGE,"E238"),subQ1])],"isStart":true})});}
            var Q1;
            {var subQ0=sQuery(id+"F17.wireOp",EDGE,"E228");var subQ1=sQuery(id+"F17.wireOp",EDGE,"E239");var subQ2=sQuery(id+"F17.wireOp",EDGE,"E235");var subQ3=sQuery(id+"F17.wireOp",EDGE,"E236");Q1=makeQuery(id+"F20.boolean.opBoolean","SPLIT",FACE,{"disambiguationData":[TD([makeQuery(id+"F20.opExtrude","SWEPT_FACE",FACE,{"disambiguationData":[OSD([sQuery(id+"F19.wireOp",EDGE,"E251")])]})])],"derivedFrom":makeQuery(id+"F18.opExtrude","CAP_FACE",FACE,{"disambiguationData":[OSD([subQ0,sQuery(id+"F17.wireOp",EDGE,"E233"),sQuery(id+"F17.wireOp",EDGE,"E234"),subQ2,subQ3,sQuery(id+"F17.wireOp",EDGE,"E237"),sQuery(id+"F17.wireOp",EDGE,"E238"),subQ1])],"isStart":true})});}
            var Q2;
            {var subQ0=sQuery(id+"F17.wireOp",EDGE,"E228");var subQ1=sQuery(id+"F17.wireOp",EDGE,"E239");var subQ2=sQuery(id+"F17.wireOp",EDGE,"E235");var subQ3=sQuery(id+"F17.wireOp",EDGE,"E236");Q2=makeQuery(id+"F20.boolean.opBoolean","SPLIT",FACE,{"disambiguationData":[TD([makeQuery(id+"F20.opExtrude","SWEPT_FACE",FACE,{"disambiguationData":[OSD([sQuery(id+"F19.wireOp",EDGE,"E252")])]})])],"derivedFrom":makeQuery(id+"F18.opExtrude","CAP_FACE",FACE,{"disambiguationData":[OSD([subQ0,sQuery(id+"F17.wireOp",EDGE,"E233"),sQuery(id+"F17.wireOp",EDGE,"E234"),subQ2,subQ3,sQuery(id+"F17.wireOp",EDGE,"E237"),sQuery(id+"F17.wireOp",EDGE,"E238"),subQ1])],"isStart":true})});}
            var Q3;
            {var subQ0=sQuery(id+"F17.wireOp",EDGE,"E228");var subQ1=sQuery(id+"F17.wireOp",EDGE,"E239");var subQ2=sQuery(id+"F17.wireOp",EDGE,"E233");var subQ3=sQuery(id+"F17.wireOp",EDGE,"E237");Q3=makeQuery(id+"F20.boolean.opBoolean","SPLIT",FACE,{"disambiguationData":[TD([makeQuery(id+"F20.opExtrude","SWEPT_FACE",FACE,{"disambiguationData":[OSD([sQuery(id+"F19.wireOp",EDGE,"E253")])]})])],"derivedFrom":makeQuery(id+"F18.opExtrude","CAP_FACE",FACE,{"disambiguationData":[OSD([subQ0,subQ2,sQuery(id+"F17.wireOp",EDGE,"E234"),sQuery(id+"F17.wireOp",EDGE,"E235"),sQuery(id+"F17.wireOp",EDGE,"E236"),subQ3,sQuery(id+"F17.wireOp",EDGE,"E238"),subQ1])],"isStart":true})});}
            extrude(context, id + "F21", {"entities" : qUnion([Q0, Q1, Q2, Q3]), "operationType" : NewBodyOperationType.REMOVE, "oppositeDirection" : true, "depth" : 31 * mm, "offsetDistance" : 25 * mm});
        }
        {
            var Q0;
            Q0=makeQuery(id+"F18.opExtrude","CAP_FACE",FACE,{"disambiguationData":[OSD([sQuery(id+"F17.wireOp",EDGE,"E228"),sQuery(id+"F17.wireOp",EDGE,"E233"),sQuery(id+"F17.wireOp",EDGE,"E234"),sQuery(id+"F17.wireOp",EDGE,"E235"),sQuery(id+"F17.wireOp",EDGE,"E236"),sQuery(id+"F17.wireOp",EDGE,"E237"),sQuery(id+"F17.wireOp",EDGE,"E238"),sQuery(id+"F17.wireOp",EDGE,"E239")])],"isStart":false});
            extrude(context, id + "F22", {"entities" : qUnion([Q0]), "operationType" : NewBodyOperationType.ADD, "depth" : 2 * mm, "offsetDistance" : 25 * mm});
        }
        {
            var Q0;
            {var subQ0=sQuery(id+"F17.wireOp",EDGE,"E238");Q0=makeQuery(id+"F20.boolean.opBoolean","SPLIT",FACE,{"disambiguationData":[TD([makeQuery(id+"F20.opExtrude","SWEPT_FACE",FACE,{"disambiguationData":[OSD([sQuery(id+"F19.wireOp",EDGE,"E244.0")])]})])],"derivedFrom":makeQuery(id+"F18.opExtrude","CAP_FACE",FACE,{"disambiguationData":[OSD([sQuery(id+"F17.wireOp",EDGE,"E228"),sQuery(id+"F17.wireOp",EDGE,"E233"),sQuery(id+"F17.wireOp",EDGE,"E234"),sQuery(id+"F17.wireOp",EDGE,"E235"),sQuery(id+"F17.wireOp",EDGE,"E236"),sQuery(id+"F17.wireOp",EDGE,"E237"),subQ0,sQuery(id+"F17.wireOp",EDGE,"E239")])],"isStart":true})});}
            var sketch = newSketch(context, id + "F23", { "sketchPlane" : qUnion([Q0])});
            skFitSpline(sketch, "E259.0.0", {"points": [v(-49.69, -5.6) * mm, v(-49.69, -5.6) * mm, v(-49.7, -5.64) * mm, v(-49.8, -5.8) * mm, v(-49.96, -6.06) * mm, v(-50.21, -6.5) * mm, v(-50.53, -7.02) * mm, v(-50.88, -7.62) * mm, v(-51.16, -8.08) * mm, v(-51.45, -8.57) * mm, v(-51.74, -9.07) * mm, v(-52.05, -9.59) * mm, v(-52.66, -10.63) * mm, v(-53.2, -11.51) * mm, v(-53.62, -12.24) * mm]});
            skLineSegment(sketch, "E259.0.1", {"start": v(-53.62, -12.24) * mm, "end": v(-9.75, -2.23) * mm});
            skLineSegment(sketch, "E259.0.2", {"start": v(-9.75, -2.23) * mm, "end": v(-7.31, -1.67) * mm});
            skArc(sketch, "E259.0.3", {"start": v(-7.31, -1.67) * mm, "mid": v(-7.5, 0) * mm, "end": v(-7.31, 1.67) * mm});
            skLineSegment(sketch, "E259.0.4", {"start": v(-7.31, 1.67) * mm, "end": v(-9.75, 2.23) * mm});
            skLineSegment(sketch, "E259.0.5", {"start": v(-9.75, 2.23) * mm, "end": v(-53.62, 12.24) * mm});
            skLineSegment(sketch, "E259.0.6", {"start": v(-53.62, 12.24) * mm, "end": v(-49.69, 5.6) * mm});
            skFitSpline(sketch, "E259.0.7", {"points": [v(-49.69, 5.6) * mm, v(-49.69, 5.6) * mm, v(-49.72, 5.57) * mm, v(-49.85, 5.43) * mm, v(-50.05, 5.21) * mm, v(-50.4, 4.85) * mm, v(-50.82, 4.4) * mm, v(-51.3, 3.9) * mm, v(-51.67, 3.5) * mm, v(-52.06, 3.1) * mm, v(-52.46, 2.67) * mm, v(-52.88, 2.24) * mm, v(-53.7, 1.36) * mm, v(-54.42, 0.61) * mm, v(-55, 0) * mm]});
            skLineSegment(sketch, "E259.0.8", {"start": v(-53.62, 1.45) * mm, "end": v(-53.62, -1.45) * mm});
            skLineSegment(sketch, "E259.0.9", {"start": v(-53.62, -1.45) * mm, "end": v(-49.69, -5.6) * mm});
            skLineSegment(sketch, "E260.0.0", {"start": v(9.75, 2.23) * mm, "end": v(7.31, 1.67) * mm});
            skArc(sketch, "E260.0.1", {"start": v(7.31, 1.67) * mm, "mid": v(7.5, 0) * mm, "end": v(7.31, -1.67) * mm});
            skLineSegment(sketch, "E260.0.2", {"start": v(7.31, -1.67) * mm, "end": v(9.75, -2.23) * mm});
            skLineSegment(sketch, "E260.0.3", {"start": v(9.75, -2.23) * mm, "end": v(53.62, -12.24) * mm});
            skLineSegment(sketch, "E260.0.4", {"start": v(53.62, -12.24) * mm, "end": v(49.69, -5.6) * mm});
            skFitSpline(sketch, "E260.0.5", {"points": [v(49.69, -5.6) * mm, v(49.69, -5.6) * mm, v(49.72, -5.57) * mm, v(49.85, -5.43) * mm, v(50.05, -5.21) * mm, v(50.4, -4.85) * mm, v(50.82, -4.4) * mm, v(51.3, -3.9) * mm, v(51.67, -3.5) * mm, v(52.06, -3.1) * mm, v(52.46, -2.67) * mm, v(52.88, -2.24) * mm, v(53.7, -1.36) * mm, v(54.42, -0.61) * mm, v(55, 0) * mm]});
            skLineSegment(sketch, "E260.0.6", {"start": v(53.62, -1.45) * mm, "end": v(53.62, 1.45) * mm});
            skLineSegment(sketch, "E260.0.7", {"start": v(53.62, 1.45) * mm, "end": v(49.69, 5.6) * mm});
            skFitSpline(sketch, "E260.0.8", {"points": [v(49.69, 5.6) * mm, v(49.69, 5.6) * mm, v(49.7, 5.64) * mm, v(49.8, 5.8) * mm, v(49.96, 6.06) * mm, v(50.21, 6.5) * mm, v(50.53, 7.02) * mm, v(50.88, 7.62) * mm, v(51.16, 8.08) * mm, v(51.45, 8.57) * mm, v(51.74, 9.07) * mm, v(52.05, 9.59) * mm, v(52.66, 10.63) * mm, v(53.2, 11.51) * mm, v(53.62, 12.24) * mm]});
            skLineSegment(sketch, "E260.0.9", {"start": v(53.62, 12.24) * mm, "end": v(9.75, 2.23) * mm});
            skPoint(sketch, "E261", {"position": v(31.69, 7.23) * mm});
            skPoint(sketch, "E262", {"position": v(31.69, -7.23) * mm});
            skArc(sketch, "E263", {"start": v(31.69, -7.23) * mm, "mid": v(37.2, 0) * mm, "end": v(31.69, 7.23) * mm});
            skArc(sketch, "E264.MirrorCS", {"start": v(-31.69, -7.23) * mm, "mid": v(-37.2, 0) * mm, "end": v(-31.69, 7.23) * mm});
            skSolve(sketch);
        }
        {
            var Q0;
            {var subQ0=sQuery(id+"F23.wireOp",EDGE,"E260.0.4");Q0=makeQuery(id+"F23.imprint","IMPRINT",FACE,{"disambiguationData":[TD([[makeQuery(id+"F23.imprint","IMPRINT",EDGE,{"derivedFrom":subQ0}),1.0]])]});}
            var Q1;
            {var subQ5=sQuery(id+"F23.wireOp",EDGE,"E259.0.0");Q1=makeQuery(id+"F23.imprint","IMPRINT",FACE,{"disambiguationData":[TD([[makeQuery(id+"F23.imprint","IMPRINT",EDGE,{"derivedFrom":subQ5}),1.0]])]});}
            extrude(context, id + "F24", {"entities" : qUnion([Q0, Q1]), "operationType" : NewBodyOperationType.ADD, "oppositeDirection" : true, "depth" : 1 * mm, "offsetDistance" : 25 * mm});
        }
    });
